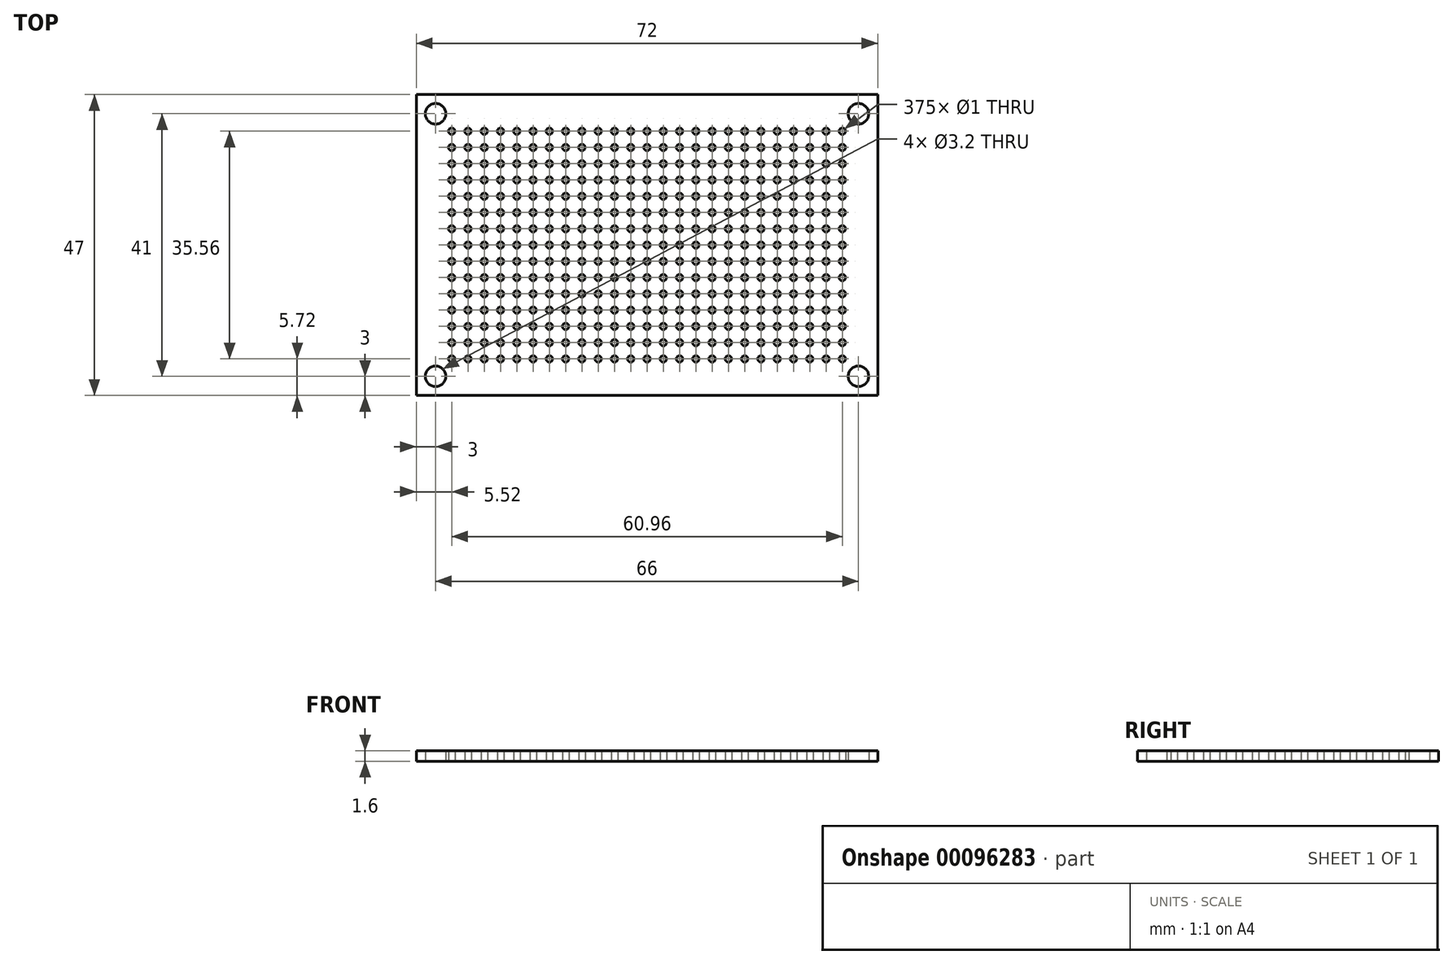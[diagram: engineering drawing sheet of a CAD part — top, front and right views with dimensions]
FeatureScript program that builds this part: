
annotation { "Feature Type Name" : "Feature", "Feature Type Description" : "" }
export const myFeature = defineFeature(function(context is Context, id is Id, definition is map)
    precondition{}
    {
        {
            var Q0;
            Q0=qCreatedBy(makeId("Top.planeOp"),FACE);
            var sketch = newSketch(context, id + "F0", { "sketchPlane" : qUnion([Q0])});
            skCircle(sketch, "E0", {"center": v(-33.1, -21.77) * mm, "radius": 1.6 * mm});
            skCircle(sketch, "E1", {"center": v(32.9, -21.77) * mm, "radius": 1.6 * mm});
            skCircle(sketch, "E2", {"center": v(32.9, 19.23) * mm, "radius": 1.6 * mm});
            skCircle(sketch, "E3", {"center": v(-33.1, 19.23) * mm, "radius": 1.6 * mm});
            skCircle(sketch, "E4", {"center": v(-30.57, -19.05) * mm, "radius": 0.5 * mm});
            skCircle(sketch, "E5.1.0.0", {"center": v(-28.03, -19.05) * mm, "radius": 0.5 * mm});
            skCircle(sketch, "E5.2.0.0", {"center": v(-25.5, -19.05) * mm, "radius": 0.5 * mm});
            skCircle(sketch, "E5.3.0.0", {"center": v(-22.95, -19.05) * mm, "radius": 0.5 * mm});
            skCircle(sketch, "E5.4.0.0", {"center": v(-20.41, -19.05) * mm, "radius": 0.5 * mm});
            skCircle(sketch, "E5.5.0.0", {"center": v(-17.87, -19.05) * mm, "radius": 0.5 * mm});
            skCircle(sketch, "E5.6.0.0", {"center": v(-15.33, -19.05) * mm, "radius": 0.5 * mm});
            skCircle(sketch, "E5.7.0.0", {"center": v(-12.8, -19.05) * mm, "radius": 0.5 * mm});
            skCircle(sketch, "E5.8.0.0", {"center": v(-10.25, -19.05) * mm, "radius": 0.5 * mm});
            skCircle(sketch, "E5.9.0.0", {"center": v(-7.71, -19.05) * mm, "radius": 0.5 * mm});
            skCircle(sketch, "E5.10.0.0", {"center": v(-5.17, -19.05) * mm, "radius": 0.5 * mm});
            skCircle(sketch, "E5.11.0.0", {"center": v(-2.63, -19.05) * mm, "radius": 0.5 * mm});
            skCircle(sketch, "E5.12.0.0", {"center": v(-0.1, -19.05) * mm, "radius": 0.5 * mm});
            skCircle(sketch, "E5.13.0.0", {"center": v(2.45, -19.05) * mm, "radius": 0.5 * mm});
            skCircle(sketch, "E5.14.0.0", {"center": v(4.99, -19.05) * mm, "radius": 0.5 * mm});
            skCircle(sketch, "E5.15.0.0", {"center": v(7.53, -19.05) * mm, "radius": 0.5 * mm});
            skCircle(sketch, "E5.16.0.0", {"center": v(10.07, -19.05) * mm, "radius": 0.5 * mm});
            skCircle(sketch, "E5.17.0.0", {"center": v(12.6, -19.05) * mm, "radius": 0.5 * mm});
            skCircle(sketch, "E5.18.0.0", {"center": v(15.15, -19.05) * mm, "radius": 0.5 * mm});
            skCircle(sketch, "E5.19.0.0", {"center": v(17.69, -19.05) * mm, "radius": 0.5 * mm});
            skCircle(sketch, "E5.20.0.0", {"center": v(20.23, -19.05) * mm, "radius": 0.5 * mm});
            skCircle(sketch, "E5.21.0.0", {"center": v(22.77, -19.05) * mm, "radius": 0.5 * mm});
            skCircle(sketch, "E5.22.0.0", {"center": v(25.3, -19.05) * mm, "radius": 0.5 * mm});
            skCircle(sketch, "E5.23.0.0", {"center": v(27.85, -19.05) * mm, "radius": 0.5 * mm});
            skCircle(sketch, "E5.24.0.0", {"center": v(30.39, -19.05) * mm, "radius": 0.5 * mm});
            skLineSegment(sketch, "E5.direction1", {"start": v(-30.57, -19.05) * mm, "end": v(-28.03, -19.05) * mm, "construction": true});
            skLineSegment(sketch, "E6", {"start": v(-33.1, -21.77) * mm, "end": v(-33.1, -19.23) * mm});
            skCircle(sketch, "E7.1.0.0", {"center": v(-30.57, -16.51) * mm, "radius": 0.5 * mm});
            skCircle(sketch, "E7.2.0.0", {"center": v(-30.57, -13.97) * mm, "radius": 0.5 * mm});
            skLineSegment(sketch, "E7.direction1", {"start": v(-30.57, -19.05) * mm, "end": v(-30.57, -16.51) * mm, "construction": true});
            skCircle(sketch, "E8.0.3.0", {"center": v(-30.57, -11.43) * mm, "radius": 0.5 * mm});
            skCircle(sketch, "E8.0.4.0", {"center": v(-30.57, -8.9) * mm, "radius": 0.5 * mm});
            skCircle(sketch, "E8.0.5.0", {"center": v(-30.57, -6.35) * mm, "radius": 0.5 * mm});
            skCircle(sketch, "E8.0.6.0", {"center": v(-30.57, -3.81) * mm, "radius": 0.5 * mm});
            skCircle(sketch, "E8.0.7.0", {"center": v(-30.57, -1.27) * mm, "radius": 0.5 * mm});
            skCircle(sketch, "E8.0.8.0", {"center": v(-30.57, 1.27) * mm, "radius": 0.5 * mm});
            skCircle(sketch, "E8.0.9.0", {"center": v(-30.57, 3.8) * mm, "radius": 0.5 * mm});
            skCircle(sketch, "E8.0.10.0", {"center": v(-30.57, 6.35) * mm, "radius": 0.5 * mm});
            skCircle(sketch, "E8.0.11.0", {"center": v(-30.57, 8.89) * mm, "radius": 0.5 * mm});
            skCircle(sketch, "E8.0.12.0", {"center": v(-30.57, 11.43) * mm, "radius": 0.5 * mm});
            skCircle(sketch, "E8.0.13.0", {"center": v(-30.57, 13.97) * mm, "radius": 0.5 * mm});
            skCircle(sketch, "E8.0.14.0", {"center": v(-30.57, 16.5) * mm, "radius": 0.5 * mm});
            skCircle(sketch, "E9.1.0.0", {"center": v(25.3, -16.51) * mm, "radius": 0.5 * mm});
            skCircle(sketch, "E9.1.0.1", {"center": v(30.39, -16.51) * mm, "radius": 0.5 * mm});
            skCircle(sketch, "E9.1.0.2", {"center": v(20.23, -16.51) * mm, "radius": 0.5 * mm});
            skCircle(sketch, "E9.1.0.3", {"center": v(22.77, -16.51) * mm, "radius": 0.5 * mm});
            skCircle(sketch, "E9.1.0.4", {"center": v(-7.71, -16.51) * mm, "radius": 0.5 * mm});
            skCircle(sketch, "E9.1.0.5", {"center": v(-15.33, -16.51) * mm, "radius": 0.5 * mm});
            skCircle(sketch, "E9.1.0.6", {"center": v(-5.17, -16.51) * mm, "radius": 0.5 * mm});
            skCircle(sketch, "E9.1.0.7", {"center": v(27.85, -16.51) * mm, "radius": 0.5 * mm});
            skCircle(sketch, "E9.1.0.8", {"center": v(12.6, -16.51) * mm, "radius": 0.5 * mm});
            skCircle(sketch, "E9.1.0.9", {"center": v(4.99, -16.51) * mm, "radius": 0.5 * mm});
            skCircle(sketch, "E9.1.0.10", {"center": v(-10.25, -16.51) * mm, "radius": 0.5 * mm});
            skCircle(sketch, "E9.1.0.11", {"center": v(-0.1, -16.51) * mm, "radius": 0.5 * mm});
            skCircle(sketch, "E9.1.0.12", {"center": v(10.07, -16.51) * mm, "radius": 0.5 * mm});
            skCircle(sketch, "E9.1.0.13", {"center": v(7.53, -16.51) * mm, "radius": 0.5 * mm});
            skCircle(sketch, "E9.1.0.14", {"center": v(17.69, -16.51) * mm, "radius": 0.5 * mm});
            skCircle(sketch, "E9.1.0.15", {"center": v(-2.63, -16.51) * mm, "radius": 0.5 * mm});
            skCircle(sketch, "E9.1.0.16", {"center": v(15.15, -16.51) * mm, "radius": 0.5 * mm});
            skCircle(sketch, "E9.1.0.17", {"center": v(-12.8, -16.51) * mm, "radius": 0.5 * mm});
            skCircle(sketch, "E9.1.0.18", {"center": v(2.45, -16.51) * mm, "radius": 0.5 * mm});
            skCircle(sketch, "E9.1.0.19", {"center": v(-22.95, -16.51) * mm, "radius": 0.5 * mm});
            skCircle(sketch, "E9.1.0.20", {"center": v(-20.41, -16.51) * mm, "radius": 0.5 * mm});
            skCircle(sketch, "E9.1.0.21", {"center": v(-28.03, -16.51) * mm, "radius": 0.5 * mm});
            skCircle(sketch, "E9.1.0.22", {"center": v(-25.5, -16.51) * mm, "radius": 0.5 * mm});
            skCircle(sketch, "E9.1.0.23", {"center": v(-17.87, -16.51) * mm, "radius": 0.5 * mm});
            skCircle(sketch, "E9.2.0.0", {"center": v(25.3, -13.97) * mm, "radius": 0.5 * mm});
            skCircle(sketch, "E9.2.0.1", {"center": v(30.39, -13.97) * mm, "radius": 0.5 * mm});
            skCircle(sketch, "E9.2.0.2", {"center": v(20.23, -13.97) * mm, "radius": 0.5 * mm});
            skCircle(sketch, "E9.2.0.3", {"center": v(22.77, -13.97) * mm, "radius": 0.5 * mm});
            skCircle(sketch, "E9.2.0.4", {"center": v(-7.71, -13.97) * mm, "radius": 0.5 * mm});
            skCircle(sketch, "E9.2.0.5", {"center": v(-15.33, -13.97) * mm, "radius": 0.5 * mm});
            skCircle(sketch, "E9.2.0.6", {"center": v(-5.17, -13.97) * mm, "radius": 0.5 * mm});
            skCircle(sketch, "E9.2.0.7", {"center": v(27.85, -13.97) * mm, "radius": 0.5 * mm});
            skCircle(sketch, "E9.2.0.8", {"center": v(12.6, -13.97) * mm, "radius": 0.5 * mm});
            skCircle(sketch, "E9.2.0.9", {"center": v(4.99, -13.97) * mm, "radius": 0.5 * mm});
            skCircle(sketch, "E9.2.0.10", {"center": v(-10.25, -13.97) * mm, "radius": 0.5 * mm});
            skCircle(sketch, "E9.2.0.11", {"center": v(-0.1, -13.97) * mm, "radius": 0.5 * mm});
            skCircle(sketch, "E9.2.0.12", {"center": v(10.07, -13.97) * mm, "radius": 0.5 * mm});
            skCircle(sketch, "E9.2.0.13", {"center": v(7.53, -13.97) * mm, "radius": 0.5 * mm});
            skCircle(sketch, "E9.2.0.14", {"center": v(17.69, -13.97) * mm, "radius": 0.5 * mm});
            skCircle(sketch, "E9.2.0.15", {"center": v(-2.63, -13.97) * mm, "radius": 0.5 * mm});
            skCircle(sketch, "E9.2.0.16", {"center": v(15.15, -13.97) * mm, "radius": 0.5 * mm});
            skCircle(sketch, "E9.2.0.17", {"center": v(-12.8, -13.97) * mm, "radius": 0.5 * mm});
            skCircle(sketch, "E9.2.0.18", {"center": v(2.45, -13.97) * mm, "radius": 0.5 * mm});
            skCircle(sketch, "E9.2.0.19", {"center": v(-22.95, -13.97) * mm, "radius": 0.5 * mm});
            skCircle(sketch, "E9.2.0.20", {"center": v(-20.41, -13.97) * mm, "radius": 0.5 * mm});
            skCircle(sketch, "E9.2.0.21", {"center": v(-28.03, -13.97) * mm, "radius": 0.5 * mm});
            skCircle(sketch, "E9.2.0.22", {"center": v(-25.5, -13.97) * mm, "radius": 0.5 * mm});
            skCircle(sketch, "E9.2.0.23", {"center": v(-17.87, -13.97) * mm, "radius": 0.5 * mm});
            skCircle(sketch, "E9.3.0.0", {"center": v(25.3, -11.43) * mm, "radius": 0.5 * mm});
            skCircle(sketch, "E9.3.0.1", {"center": v(30.39, -11.43) * mm, "radius": 0.5 * mm});
            skCircle(sketch, "E9.3.0.2", {"center": v(20.23, -11.43) * mm, "radius": 0.5 * mm});
            skCircle(sketch, "E9.3.0.3", {"center": v(22.77, -11.43) * mm, "radius": 0.5 * mm});
            skCircle(sketch, "E9.3.0.4", {"center": v(-7.71, -11.43) * mm, "radius": 0.5 * mm});
            skCircle(sketch, "E9.3.0.5", {"center": v(-15.33, -11.43) * mm, "radius": 0.5 * mm});
            skCircle(sketch, "E9.3.0.6", {"center": v(-5.17, -11.43) * mm, "radius": 0.5 * mm});
            skCircle(sketch, "E9.3.0.7", {"center": v(27.85, -11.43) * mm, "radius": 0.5 * mm});
            skCircle(sketch, "E9.3.0.8", {"center": v(12.6, -11.43) * mm, "radius": 0.5 * mm});
            skCircle(sketch, "E9.3.0.9", {"center": v(4.99, -11.43) * mm, "radius": 0.5 * mm});
            skCircle(sketch, "E9.3.0.10", {"center": v(-10.25, -11.43) * mm, "radius": 0.5 * mm});
            skCircle(sketch, "E9.3.0.11", {"center": v(-0.1, -11.43) * mm, "radius": 0.5 * mm});
            skCircle(sketch, "E9.3.0.12", {"center": v(10.07, -11.43) * mm, "radius": 0.5 * mm});
            skCircle(sketch, "E9.3.0.13", {"center": v(7.53, -11.43) * mm, "radius": 0.5 * mm});
            skCircle(sketch, "E9.3.0.14", {"center": v(17.69, -11.43) * mm, "radius": 0.5 * mm});
            skCircle(sketch, "E9.3.0.15", {"center": v(-2.63, -11.43) * mm, "radius": 0.5 * mm});
            skCircle(sketch, "E9.3.0.16", {"center": v(15.15, -11.43) * mm, "radius": 0.5 * mm});
            skCircle(sketch, "E9.3.0.17", {"center": v(-12.8, -11.43) * mm, "radius": 0.5 * mm});
            skCircle(sketch, "E9.3.0.18", {"center": v(2.45, -11.43) * mm, "radius": 0.5 * mm});
            skCircle(sketch, "E9.3.0.19", {"center": v(-22.95, -11.43) * mm, "radius": 0.5 * mm});
            skCircle(sketch, "E9.3.0.20", {"center": v(-20.41, -11.43) * mm, "radius": 0.5 * mm});
            skCircle(sketch, "E9.3.0.21", {"center": v(-28.03, -11.43) * mm, "radius": 0.5 * mm});
            skCircle(sketch, "E9.3.0.22", {"center": v(-25.5, -11.43) * mm, "radius": 0.5 * mm});
            skCircle(sketch, "E9.3.0.23", {"center": v(-17.87, -11.43) * mm, "radius": 0.5 * mm});
            skCircle(sketch, "E9.4.0.0", {"center": v(25.3, -8.9) * mm, "radius": 0.5 * mm});
            skCircle(sketch, "E9.4.0.1", {"center": v(30.39, -8.9) * mm, "radius": 0.5 * mm});
            skCircle(sketch, "E9.4.0.2", {"center": v(20.23, -8.9) * mm, "radius": 0.5 * mm});
            skCircle(sketch, "E9.4.0.3", {"center": v(22.77, -8.9) * mm, "radius": 0.5 * mm});
            skCircle(sketch, "E9.4.0.4", {"center": v(-7.71, -8.9) * mm, "radius": 0.5 * mm});
            skCircle(sketch, "E9.4.0.5", {"center": v(-15.33, -8.9) * mm, "radius": 0.5 * mm});
            skCircle(sketch, "E9.4.0.6", {"center": v(-5.17, -8.9) * mm, "radius": 0.5 * mm});
            skCircle(sketch, "E9.4.0.7", {"center": v(27.85, -8.9) * mm, "radius": 0.5 * mm});
            skCircle(sketch, "E9.4.0.8", {"center": v(12.6, -8.9) * mm, "radius": 0.5 * mm});
            skCircle(sketch, "E9.4.0.9", {"center": v(4.99, -8.9) * mm, "radius": 0.5 * mm});
            skCircle(sketch, "E9.4.0.10", {"center": v(-10.25, -8.9) * mm, "radius": 0.5 * mm});
            skCircle(sketch, "E9.4.0.11", {"center": v(-0.1, -8.9) * mm, "radius": 0.5 * mm});
            skCircle(sketch, "E9.4.0.12", {"center": v(10.07, -8.9) * mm, "radius": 0.5 * mm});
            skCircle(sketch, "E9.4.0.13", {"center": v(7.53, -8.9) * mm, "radius": 0.5 * mm});
            skCircle(sketch, "E9.4.0.14", {"center": v(17.69, -8.9) * mm, "radius": 0.5 * mm});
            skCircle(sketch, "E9.4.0.15", {"center": v(-2.63, -8.9) * mm, "radius": 0.5 * mm});
            skCircle(sketch, "E9.4.0.16", {"center": v(15.15, -8.9) * mm, "radius": 0.5 * mm});
            skCircle(sketch, "E9.4.0.17", {"center": v(-12.8, -8.9) * mm, "radius": 0.5 * mm});
            skCircle(sketch, "E9.4.0.18", {"center": v(2.45, -8.9) * mm, "radius": 0.5 * mm});
            skCircle(sketch, "E9.4.0.19", {"center": v(-22.95, -8.9) * mm, "radius": 0.5 * mm});
            skCircle(sketch, "E9.4.0.20", {"center": v(-20.41, -8.9) * mm, "radius": 0.5 * mm});
            skCircle(sketch, "E9.4.0.21", {"center": v(-28.03, -8.9) * mm, "radius": 0.5 * mm});
            skCircle(sketch, "E9.4.0.22", {"center": v(-25.5, -8.9) * mm, "radius": 0.5 * mm});
            skCircle(sketch, "E9.4.0.23", {"center": v(-17.87, -8.9) * mm, "radius": 0.5 * mm});
            skCircle(sketch, "E9.5.0.0", {"center": v(25.3, -6.35) * mm, "radius": 0.5 * mm});
            skCircle(sketch, "E9.5.0.1", {"center": v(30.39, -6.35) * mm, "radius": 0.5 * mm});
            skCircle(sketch, "E9.5.0.2", {"center": v(20.23, -6.35) * mm, "radius": 0.5 * mm});
            skCircle(sketch, "E9.5.0.3", {"center": v(22.77, -6.35) * mm, "radius": 0.5 * mm});
            skCircle(sketch, "E9.5.0.4", {"center": v(-7.71, -6.35) * mm, "radius": 0.5 * mm});
            skCircle(sketch, "E9.5.0.5", {"center": v(-15.33, -6.35) * mm, "radius": 0.5 * mm});
            skCircle(sketch, "E9.5.0.6", {"center": v(-5.17, -6.35) * mm, "radius": 0.5 * mm});
            skCircle(sketch, "E9.5.0.7", {"center": v(27.85, -6.35) * mm, "radius": 0.5 * mm});
            skCircle(sketch, "E9.5.0.8", {"center": v(12.6, -6.35) * mm, "radius": 0.5 * mm});
            skCircle(sketch, "E9.5.0.9", {"center": v(4.99, -6.35) * mm, "radius": 0.5 * mm});
            skCircle(sketch, "E9.5.0.10", {"center": v(-10.25, -6.35) * mm, "radius": 0.5 * mm});
            skCircle(sketch, "E9.5.0.11", {"center": v(-0.1, -6.35) * mm, "radius": 0.5 * mm});
            skCircle(sketch, "E9.5.0.12", {"center": v(10.07, -6.35) * mm, "radius": 0.5 * mm});
            skCircle(sketch, "E9.5.0.13", {"center": v(7.53, -6.35) * mm, "radius": 0.5 * mm});
            skCircle(sketch, "E9.5.0.14", {"center": v(17.69, -6.35) * mm, "radius": 0.5 * mm});
            skCircle(sketch, "E9.5.0.15", {"center": v(-2.63, -6.35) * mm, "radius": 0.5 * mm});
            skCircle(sketch, "E9.5.0.16", {"center": v(15.15, -6.35) * mm, "radius": 0.5 * mm});
            skCircle(sketch, "E9.5.0.17", {"center": v(-12.8, -6.35) * mm, "radius": 0.5 * mm});
            skCircle(sketch, "E9.5.0.18", {"center": v(2.45, -6.35) * mm, "radius": 0.5 * mm});
            skCircle(sketch, "E9.5.0.19", {"center": v(-22.95, -6.35) * mm, "radius": 0.5 * mm});
            skCircle(sketch, "E9.5.0.20", {"center": v(-20.41, -6.35) * mm, "radius": 0.5 * mm});
            skCircle(sketch, "E9.5.0.21", {"center": v(-28.03, -6.35) * mm, "radius": 0.5 * mm});
            skCircle(sketch, "E9.5.0.22", {"center": v(-25.5, -6.35) * mm, "radius": 0.5 * mm});
            skCircle(sketch, "E9.5.0.23", {"center": v(-17.87, -6.35) * mm, "radius": 0.5 * mm});
            skCircle(sketch, "E9.6.0.0", {"center": v(25.3, -3.81) * mm, "radius": 0.5 * mm});
            skCircle(sketch, "E9.6.0.1", {"center": v(30.39, -3.81) * mm, "radius": 0.5 * mm});
            skCircle(sketch, "E9.6.0.2", {"center": v(20.23, -3.81) * mm, "radius": 0.5 * mm});
            skCircle(sketch, "E9.6.0.3", {"center": v(22.77, -3.81) * mm, "radius": 0.5 * mm});
            skCircle(sketch, "E9.6.0.4", {"center": v(-7.71, -3.81) * mm, "radius": 0.5 * mm});
            skCircle(sketch, "E9.6.0.5", {"center": v(-15.33, -3.81) * mm, "radius": 0.5 * mm});
            skCircle(sketch, "E9.6.0.6", {"center": v(-5.17, -3.81) * mm, "radius": 0.5 * mm});
            skCircle(sketch, "E9.6.0.7", {"center": v(27.85, -3.81) * mm, "radius": 0.5 * mm});
            skCircle(sketch, "E9.6.0.8", {"center": v(12.6, -3.81) * mm, "radius": 0.5 * mm});
            skCircle(sketch, "E9.6.0.9", {"center": v(4.99, -3.81) * mm, "radius": 0.5 * mm});
            skCircle(sketch, "E9.6.0.10", {"center": v(-10.25, -3.81) * mm, "radius": 0.5 * mm});
            skCircle(sketch, "E9.6.0.11", {"center": v(-0.1, -3.81) * mm, "radius": 0.5 * mm});
            skCircle(sketch, "E9.6.0.12", {"center": v(10.07, -3.81) * mm, "radius": 0.5 * mm});
            skCircle(sketch, "E9.6.0.13", {"center": v(7.53, -3.81) * mm, "radius": 0.5 * mm});
            skCircle(sketch, "E9.6.0.14", {"center": v(17.69, -3.81) * mm, "radius": 0.5 * mm});
            skCircle(sketch, "E9.6.0.15", {"center": v(-2.63, -3.81) * mm, "radius": 0.5 * mm});
            skCircle(sketch, "E9.6.0.16", {"center": v(15.15, -3.81) * mm, "radius": 0.5 * mm});
            skCircle(sketch, "E9.6.0.17", {"center": v(-12.8, -3.81) * mm, "radius": 0.5 * mm});
            skCircle(sketch, "E9.6.0.18", {"center": v(2.45, -3.81) * mm, "radius": 0.5 * mm});
            skCircle(sketch, "E9.6.0.19", {"center": v(-22.95, -3.81) * mm, "radius": 0.5 * mm});
            skCircle(sketch, "E9.6.0.20", {"center": v(-20.41, -3.81) * mm, "radius": 0.5 * mm});
            skCircle(sketch, "E9.6.0.21", {"center": v(-28.03, -3.81) * mm, "radius": 0.5 * mm});
            skCircle(sketch, "E9.6.0.22", {"center": v(-25.5, -3.81) * mm, "radius": 0.5 * mm});
            skCircle(sketch, "E9.6.0.23", {"center": v(-17.87, -3.81) * mm, "radius": 0.5 * mm});
            skCircle(sketch, "E9.7.0.0", {"center": v(25.3, -1.27) * mm, "radius": 0.5 * mm});
            skCircle(sketch, "E9.7.0.1", {"center": v(30.39, -1.27) * mm, "radius": 0.5 * mm});
            skCircle(sketch, "E9.7.0.2", {"center": v(20.23, -1.27) * mm, "radius": 0.5 * mm});
            skCircle(sketch, "E9.7.0.3", {"center": v(22.77, -1.27) * mm, "radius": 0.5 * mm});
            skCircle(sketch, "E9.7.0.4", {"center": v(-7.71, -1.27) * mm, "radius": 0.5 * mm});
            skCircle(sketch, "E9.7.0.5", {"center": v(-15.33, -1.27) * mm, "radius": 0.5 * mm});
            skCircle(sketch, "E9.7.0.6", {"center": v(-5.17, -1.27) * mm, "radius": 0.5 * mm});
            skCircle(sketch, "E9.7.0.7", {"center": v(27.85, -1.27) * mm, "radius": 0.5 * mm});
            skCircle(sketch, "E9.7.0.8", {"center": v(12.6, -1.27) * mm, "radius": 0.5 * mm});
            skCircle(sketch, "E9.7.0.9", {"center": v(4.99, -1.27) * mm, "radius": 0.5 * mm});
            skCircle(sketch, "E9.7.0.10", {"center": v(-10.25, -1.27) * mm, "radius": 0.5 * mm});
            skCircle(sketch, "E9.7.0.11", {"center": v(-0.1, -1.27) * mm, "radius": 0.5 * mm});
            skCircle(sketch, "E9.7.0.12", {"center": v(10.07, -1.27) * mm, "radius": 0.5 * mm});
            skCircle(sketch, "E9.7.0.13", {"center": v(7.53, -1.27) * mm, "radius": 0.5 * mm});
            skCircle(sketch, "E9.7.0.14", {"center": v(17.69, -1.27) * mm, "radius": 0.5 * mm});
            skCircle(sketch, "E9.7.0.15", {"center": v(-2.63, -1.27) * mm, "radius": 0.5 * mm});
            skCircle(sketch, "E9.7.0.16", {"center": v(15.15, -1.27) * mm, "radius": 0.5 * mm});
            skCircle(sketch, "E9.7.0.17", {"center": v(-12.8, -1.27) * mm, "radius": 0.5 * mm});
            skCircle(sketch, "E9.7.0.18", {"center": v(2.45, -1.27) * mm, "radius": 0.5 * mm});
            skCircle(sketch, "E9.7.0.19", {"center": v(-22.95, -1.27) * mm, "radius": 0.5 * mm});
            skCircle(sketch, "E9.7.0.20", {"center": v(-20.41, -1.27) * mm, "radius": 0.5 * mm});
            skCircle(sketch, "E9.7.0.21", {"center": v(-28.03, -1.27) * mm, "radius": 0.5 * mm});
            skCircle(sketch, "E9.7.0.22", {"center": v(-25.5, -1.27) * mm, "radius": 0.5 * mm});
            skCircle(sketch, "E9.7.0.23", {"center": v(-17.87, -1.27) * mm, "radius": 0.5 * mm});
            skCircle(sketch, "E9.8.0.0", {"center": v(25.3, 1.27) * mm, "radius": 0.5 * mm});
            skCircle(sketch, "E9.8.0.1", {"center": v(30.39, 1.27) * mm, "radius": 0.5 * mm});
            skCircle(sketch, "E9.8.0.2", {"center": v(20.23, 1.27) * mm, "radius": 0.5 * mm});
            skCircle(sketch, "E9.8.0.3", {"center": v(22.77, 1.27) * mm, "radius": 0.5 * mm});
            skCircle(sketch, "E9.8.0.4", {"center": v(-7.71, 1.27) * mm, "radius": 0.5 * mm});
            skCircle(sketch, "E9.8.0.5", {"center": v(-15.33, 1.27) * mm, "radius": 0.5 * mm});
            skCircle(sketch, "E9.8.0.6", {"center": v(-5.17, 1.27) * mm, "radius": 0.5 * mm});
            skCircle(sketch, "E9.8.0.7", {"center": v(27.85, 1.27) * mm, "radius": 0.5 * mm});
            skCircle(sketch, "E9.8.0.8", {"center": v(12.6, 1.27) * mm, "radius": 0.5 * mm});
            skCircle(sketch, "E9.8.0.9", {"center": v(4.99, 1.27) * mm, "radius": 0.5 * mm});
            skCircle(sketch, "E9.8.0.10", {"center": v(-10.25, 1.27) * mm, "radius": 0.5 * mm});
            skCircle(sketch, "E9.8.0.11", {"center": v(-0.1, 1.27) * mm, "radius": 0.5 * mm});
            skCircle(sketch, "E9.8.0.12", {"center": v(10.07, 1.27) * mm, "radius": 0.5 * mm});
            skCircle(sketch, "E9.8.0.13", {"center": v(7.53, 1.27) * mm, "radius": 0.5 * mm});
            skCircle(sketch, "E9.8.0.14", {"center": v(17.69, 1.27) * mm, "radius": 0.5 * mm});
            skCircle(sketch, "E9.8.0.15", {"center": v(-2.63, 1.27) * mm, "radius": 0.5 * mm});
            skCircle(sketch, "E9.8.0.16", {"center": v(15.15, 1.27) * mm, "radius": 0.5 * mm});
            skCircle(sketch, "E9.8.0.17", {"center": v(-12.8, 1.27) * mm, "radius": 0.5 * mm});
            skCircle(sketch, "E9.8.0.18", {"center": v(2.45, 1.27) * mm, "radius": 0.5 * mm});
            skCircle(sketch, "E9.8.0.19", {"center": v(-22.95, 1.27) * mm, "radius": 0.5 * mm});
            skCircle(sketch, "E9.8.0.20", {"center": v(-20.41, 1.27) * mm, "radius": 0.5 * mm});
            skCircle(sketch, "E9.8.0.21", {"center": v(-28.03, 1.27) * mm, "radius": 0.5 * mm});
            skCircle(sketch, "E9.8.0.22", {"center": v(-25.5, 1.27) * mm, "radius": 0.5 * mm});
            skCircle(sketch, "E9.8.0.23", {"center": v(-17.87, 1.27) * mm, "radius": 0.5 * mm});
            skCircle(sketch, "E9.9.0.0", {"center": v(25.3, 3.8) * mm, "radius": 0.5 * mm});
            skCircle(sketch, "E9.9.0.1", {"center": v(30.39, 3.8) * mm, "radius": 0.5 * mm});
            skCircle(sketch, "E9.9.0.2", {"center": v(20.23, 3.8) * mm, "radius": 0.5 * mm});
            skCircle(sketch, "E9.9.0.3", {"center": v(22.77, 3.8) * mm, "radius": 0.5 * mm});
            skCircle(sketch, "E9.9.0.4", {"center": v(-7.71, 3.8) * mm, "radius": 0.5 * mm});
            skCircle(sketch, "E9.9.0.5", {"center": v(-15.33, 3.8) * mm, "radius": 0.5 * mm});
            skCircle(sketch, "E9.9.0.6", {"center": v(-5.17, 3.8) * mm, "radius": 0.5 * mm});
            skCircle(sketch, "E9.9.0.7", {"center": v(27.85, 3.8) * mm, "radius": 0.5 * mm});
            skCircle(sketch, "E9.9.0.8", {"center": v(12.6, 3.8) * mm, "radius": 0.5 * mm});
            skCircle(sketch, "E9.9.0.9", {"center": v(4.99, 3.8) * mm, "radius": 0.5 * mm});
            skCircle(sketch, "E9.9.0.10", {"center": v(-10.25, 3.8) * mm, "radius": 0.5 * mm});
            skCircle(sketch, "E9.9.0.11", {"center": v(-0.1, 3.8) * mm, "radius": 0.5 * mm});
            skCircle(sketch, "E9.9.0.12", {"center": v(10.07, 3.8) * mm, "radius": 0.5 * mm});
            skCircle(sketch, "E9.9.0.13", {"center": v(7.53, 3.8) * mm, "radius": 0.5 * mm});
            skCircle(sketch, "E9.9.0.14", {"center": v(17.69, 3.8) * mm, "radius": 0.5 * mm});
            skCircle(sketch, "E9.9.0.15", {"center": v(-2.63, 3.8) * mm, "radius": 0.5 * mm});
            skCircle(sketch, "E9.9.0.16", {"center": v(15.15, 3.8) * mm, "radius": 0.5 * mm});
            skCircle(sketch, "E9.9.0.17", {"center": v(-12.8, 3.8) * mm, "radius": 0.5 * mm});
            skCircle(sketch, "E9.9.0.18", {"center": v(2.45, 3.8) * mm, "radius": 0.5 * mm});
            skCircle(sketch, "E9.9.0.19", {"center": v(-22.95, 3.8) * mm, "radius": 0.5 * mm});
            skCircle(sketch, "E9.9.0.20", {"center": v(-20.41, 3.8) * mm, "radius": 0.5 * mm});
            skCircle(sketch, "E9.9.0.21", {"center": v(-28.03, 3.8) * mm, "radius": 0.5 * mm});
            skCircle(sketch, "E9.9.0.22", {"center": v(-25.5, 3.8) * mm, "radius": 0.5 * mm});
            skCircle(sketch, "E9.9.0.23", {"center": v(-17.87, 3.8) * mm, "radius": 0.5 * mm});
            skCircle(sketch, "E9.10.0.0", {"center": v(25.3, 6.35) * mm, "radius": 0.5 * mm});
            skCircle(sketch, "E9.10.0.1", {"center": v(30.39, 6.35) * mm, "radius": 0.5 * mm});
            skCircle(sketch, "E9.10.0.2", {"center": v(20.23, 6.35) * mm, "radius": 0.5 * mm});
            skCircle(sketch, "E9.10.0.3", {"center": v(22.77, 6.35) * mm, "radius": 0.5 * mm});
            skCircle(sketch, "E9.10.0.4", {"center": v(-7.71, 6.35) * mm, "radius": 0.5 * mm});
            skCircle(sketch, "E9.10.0.5", {"center": v(-15.33, 6.35) * mm, "radius": 0.5 * mm});
            skCircle(sketch, "E9.10.0.6", {"center": v(-5.17, 6.35) * mm, "radius": 0.5 * mm});
            skCircle(sketch, "E9.10.0.7", {"center": v(27.85, 6.35) * mm, "radius": 0.5 * mm});
            skCircle(sketch, "E9.10.0.8", {"center": v(12.6, 6.35) * mm, "radius": 0.5 * mm});
            skCircle(sketch, "E9.10.0.9", {"center": v(4.99, 6.35) * mm, "radius": 0.5 * mm});
            skCircle(sketch, "E9.10.0.10", {"center": v(-10.25, 6.35) * mm, "radius": 0.5 * mm});
            skCircle(sketch, "E9.10.0.11", {"center": v(-0.1, 6.35) * mm, "radius": 0.5 * mm});
            skCircle(sketch, "E9.10.0.12", {"center": v(10.07, 6.35) * mm, "radius": 0.5 * mm});
            skCircle(sketch, "E9.10.0.13", {"center": v(7.53, 6.35) * mm, "radius": 0.5 * mm});
            skCircle(sketch, "E9.10.0.14", {"center": v(17.69, 6.35) * mm, "radius": 0.5 * mm});
            skCircle(sketch, "E9.10.0.15", {"center": v(-2.63, 6.35) * mm, "radius": 0.5 * mm});
            skCircle(sketch, "E9.10.0.16", {"center": v(15.15, 6.35) * mm, "radius": 0.5 * mm});
            skCircle(sketch, "E9.10.0.17", {"center": v(-12.8, 6.35) * mm, "radius": 0.5 * mm});
            skCircle(sketch, "E9.10.0.18", {"center": v(2.45, 6.35) * mm, "radius": 0.5 * mm});
            skCircle(sketch, "E9.10.0.19", {"center": v(-22.95, 6.35) * mm, "radius": 0.5 * mm});
            skCircle(sketch, "E9.10.0.20", {"center": v(-20.41, 6.35) * mm, "radius": 0.5 * mm});
            skCircle(sketch, "E9.10.0.21", {"center": v(-28.03, 6.35) * mm, "radius": 0.5 * mm});
            skCircle(sketch, "E9.10.0.22", {"center": v(-25.5, 6.35) * mm, "radius": 0.5 * mm});
            skCircle(sketch, "E9.10.0.23", {"center": v(-17.87, 6.35) * mm, "radius": 0.5 * mm});
            skCircle(sketch, "E9.11.0.0", {"center": v(25.3, 8.89) * mm, "radius": 0.5 * mm});
            skCircle(sketch, "E9.11.0.1", {"center": v(30.39, 8.89) * mm, "radius": 0.5 * mm});
            skCircle(sketch, "E9.11.0.2", {"center": v(20.23, 8.89) * mm, "radius": 0.5 * mm});
            skCircle(sketch, "E9.11.0.3", {"center": v(22.77, 8.89) * mm, "radius": 0.5 * mm});
            skCircle(sketch, "E9.11.0.4", {"center": v(-7.71, 8.89) * mm, "radius": 0.5 * mm});
            skCircle(sketch, "E9.11.0.5", {"center": v(-15.33, 8.89) * mm, "radius": 0.5 * mm});
            skCircle(sketch, "E9.11.0.6", {"center": v(-5.17, 8.89) * mm, "radius": 0.5 * mm});
            skCircle(sketch, "E9.11.0.7", {"center": v(27.85, 8.89) * mm, "radius": 0.5 * mm});
            skCircle(sketch, "E9.11.0.8", {"center": v(12.6, 8.89) * mm, "radius": 0.5 * mm});
            skCircle(sketch, "E9.11.0.9", {"center": v(4.99, 8.89) * mm, "radius": 0.5 * mm});
            skCircle(sketch, "E9.11.0.10", {"center": v(-10.25, 8.89) * mm, "radius": 0.5 * mm});
            skCircle(sketch, "E9.11.0.11", {"center": v(-0.1, 8.89) * mm, "radius": 0.5 * mm});
            skCircle(sketch, "E9.11.0.12", {"center": v(10.07, 8.89) * mm, "radius": 0.5 * mm});
            skCircle(sketch, "E9.11.0.13", {"center": v(7.53, 8.89) * mm, "radius": 0.5 * mm});
            skCircle(sketch, "E9.11.0.14", {"center": v(17.69, 8.89) * mm, "radius": 0.5 * mm});
            skCircle(sketch, "E9.11.0.15", {"center": v(-2.63, 8.89) * mm, "radius": 0.5 * mm});
            skCircle(sketch, "E9.11.0.16", {"center": v(15.15, 8.89) * mm, "radius": 0.5 * mm});
            skCircle(sketch, "E9.11.0.17", {"center": v(-12.8, 8.89) * mm, "radius": 0.5 * mm});
            skCircle(sketch, "E9.11.0.18", {"center": v(2.45, 8.89) * mm, "radius": 0.5 * mm});
            skCircle(sketch, "E9.11.0.19", {"center": v(-22.95, 8.89) * mm, "radius": 0.5 * mm});
            skCircle(sketch, "E9.11.0.20", {"center": v(-20.41, 8.89) * mm, "radius": 0.5 * mm});
            skCircle(sketch, "E9.11.0.21", {"center": v(-28.03, 8.89) * mm, "radius": 0.5 * mm});
            skCircle(sketch, "E9.11.0.22", {"center": v(-25.5, 8.89) * mm, "radius": 0.5 * mm});
            skCircle(sketch, "E9.11.0.23", {"center": v(-17.87, 8.89) * mm, "radius": 0.5 * mm});
            skCircle(sketch, "E9.12.0.0", {"center": v(25.3, 11.43) * mm, "radius": 0.5 * mm});
            skCircle(sketch, "E9.12.0.1", {"center": v(30.39, 11.43) * mm, "radius": 0.5 * mm});
            skCircle(sketch, "E9.12.0.2", {"center": v(20.23, 11.43) * mm, "radius": 0.5 * mm});
            skCircle(sketch, "E9.12.0.3", {"center": v(22.77, 11.43) * mm, "radius": 0.5 * mm});
            skCircle(sketch, "E9.12.0.4", {"center": v(-7.71, 11.43) * mm, "radius": 0.5 * mm});
            skCircle(sketch, "E9.12.0.5", {"center": v(-15.33, 11.43) * mm, "radius": 0.5 * mm});
            skCircle(sketch, "E9.12.0.6", {"center": v(-5.17, 11.43) * mm, "radius": 0.5 * mm});
            skCircle(sketch, "E9.12.0.7", {"center": v(27.85, 11.43) * mm, "radius": 0.5 * mm});
            skCircle(sketch, "E9.12.0.8", {"center": v(12.6, 11.43) * mm, "radius": 0.5 * mm});
            skCircle(sketch, "E9.12.0.9", {"center": v(4.99, 11.43) * mm, "radius": 0.5 * mm});
            skCircle(sketch, "E9.12.0.10", {"center": v(-10.25, 11.43) * mm, "radius": 0.5 * mm});
            skCircle(sketch, "E9.12.0.11", {"center": v(-0.1, 11.43) * mm, "radius": 0.5 * mm});
            skCircle(sketch, "E9.12.0.12", {"center": v(10.07, 11.43) * mm, "radius": 0.5 * mm});
            skCircle(sketch, "E9.12.0.13", {"center": v(7.53, 11.43) * mm, "radius": 0.5 * mm});
            skCircle(sketch, "E9.12.0.14", {"center": v(17.69, 11.43) * mm, "radius": 0.5 * mm});
            skCircle(sketch, "E9.12.0.15", {"center": v(-2.63, 11.43) * mm, "radius": 0.5 * mm});
            skCircle(sketch, "E9.12.0.16", {"center": v(15.15, 11.43) * mm, "radius": 0.5 * mm});
            skCircle(sketch, "E9.12.0.17", {"center": v(-12.8, 11.43) * mm, "radius": 0.5 * mm});
            skCircle(sketch, "E9.12.0.18", {"center": v(2.45, 11.43) * mm, "radius": 0.5 * mm});
            skCircle(sketch, "E9.12.0.19", {"center": v(-22.95, 11.43) * mm, "radius": 0.5 * mm});
            skCircle(sketch, "E9.12.0.20", {"center": v(-20.41, 11.43) * mm, "radius": 0.5 * mm});
            skCircle(sketch, "E9.12.0.21", {"center": v(-28.03, 11.43) * mm, "radius": 0.5 * mm});
            skCircle(sketch, "E9.12.0.22", {"center": v(-25.5, 11.43) * mm, "radius": 0.5 * mm});
            skCircle(sketch, "E9.12.0.23", {"center": v(-17.87, 11.43) * mm, "radius": 0.5 * mm});
            skCircle(sketch, "E9.13.0.0", {"center": v(25.3, 13.97) * mm, "radius": 0.5 * mm});
            skCircle(sketch, "E9.13.0.1", {"center": v(30.39, 13.97) * mm, "radius": 0.5 * mm});
            skCircle(sketch, "E9.13.0.2", {"center": v(20.23, 13.97) * mm, "radius": 0.5 * mm});
            skCircle(sketch, "E9.13.0.3", {"center": v(22.77, 13.97) * mm, "radius": 0.5 * mm});
            skCircle(sketch, "E9.13.0.4", {"center": v(-7.71, 13.97) * mm, "radius": 0.5 * mm});
            skCircle(sketch, "E9.13.0.5", {"center": v(-15.33, 13.97) * mm, "radius": 0.5 * mm});
            skCircle(sketch, "E9.13.0.6", {"center": v(-5.17, 13.97) * mm, "radius": 0.5 * mm});
            skCircle(sketch, "E9.13.0.7", {"center": v(27.85, 13.97) * mm, "radius": 0.5 * mm});
            skCircle(sketch, "E9.13.0.8", {"center": v(12.6, 13.97) * mm, "radius": 0.5 * mm});
            skCircle(sketch, "E9.13.0.9", {"center": v(4.99, 13.97) * mm, "radius": 0.5 * mm});
            skCircle(sketch, "E9.13.0.10", {"center": v(-10.25, 13.97) * mm, "radius": 0.5 * mm});
            skCircle(sketch, "E9.13.0.11", {"center": v(-0.1, 13.97) * mm, "radius": 0.5 * mm});
            skCircle(sketch, "E9.13.0.12", {"center": v(10.07, 13.97) * mm, "radius": 0.5 * mm});
            skCircle(sketch, "E9.13.0.13", {"center": v(7.53, 13.97) * mm, "radius": 0.5 * mm});
            skCircle(sketch, "E9.13.0.14", {"center": v(17.69, 13.97) * mm, "radius": 0.5 * mm});
            skCircle(sketch, "E9.13.0.15", {"center": v(-2.63, 13.97) * mm, "radius": 0.5 * mm});
            skCircle(sketch, "E9.13.0.16", {"center": v(15.15, 13.97) * mm, "radius": 0.5 * mm});
            skCircle(sketch, "E9.13.0.17", {"center": v(-12.8, 13.97) * mm, "radius": 0.5 * mm});
            skCircle(sketch, "E9.13.0.18", {"center": v(2.45, 13.97) * mm, "radius": 0.5 * mm});
            skCircle(sketch, "E9.13.0.19", {"center": v(-22.95, 13.97) * mm, "radius": 0.5 * mm});
            skCircle(sketch, "E9.13.0.20", {"center": v(-20.41, 13.97) * mm, "radius": 0.5 * mm});
            skCircle(sketch, "E9.13.0.21", {"center": v(-28.03, 13.97) * mm, "radius": 0.5 * mm});
            skCircle(sketch, "E9.13.0.22", {"center": v(-25.5, 13.97) * mm, "radius": 0.5 * mm});
            skCircle(sketch, "E9.13.0.23", {"center": v(-17.87, 13.97) * mm, "radius": 0.5 * mm});
            skCircle(sketch, "E9.14.0.0", {"center": v(25.3, 16.5) * mm, "radius": 0.5 * mm});
            skCircle(sketch, "E9.14.0.1", {"center": v(30.39, 16.5) * mm, "radius": 0.5 * mm});
            skCircle(sketch, "E9.14.0.2", {"center": v(20.23, 16.5) * mm, "radius": 0.5 * mm});
            skCircle(sketch, "E9.14.0.3", {"center": v(22.77, 16.5) * mm, "radius": 0.5 * mm});
            skCircle(sketch, "E9.14.0.4", {"center": v(-7.71, 16.5) * mm, "radius": 0.5 * mm});
            skCircle(sketch, "E9.14.0.5", {"center": v(-15.33, 16.5) * mm, "radius": 0.5 * mm});
            skCircle(sketch, "E9.14.0.6", {"center": v(-5.17, 16.5) * mm, "radius": 0.5 * mm});
            skCircle(sketch, "E9.14.0.7", {"center": v(27.85, 16.5) * mm, "radius": 0.5 * mm});
            skCircle(sketch, "E9.14.0.8", {"center": v(12.6, 16.5) * mm, "radius": 0.5 * mm});
            skCircle(sketch, "E9.14.0.9", {"center": v(4.99, 16.5) * mm, "radius": 0.5 * mm});
            skCircle(sketch, "E9.14.0.10", {"center": v(-10.25, 16.5) * mm, "radius": 0.5 * mm});
            skCircle(sketch, "E9.14.0.11", {"center": v(-0.1, 16.5) * mm, "radius": 0.5 * mm});
            skCircle(sketch, "E9.14.0.12", {"center": v(10.07, 16.5) * mm, "radius": 0.5 * mm});
            skCircle(sketch, "E9.14.0.13", {"center": v(7.53, 16.5) * mm, "radius": 0.5 * mm});
            skCircle(sketch, "E9.14.0.14", {"center": v(17.69, 16.5) * mm, "radius": 0.5 * mm});
            skCircle(sketch, "E9.14.0.15", {"center": v(-2.63, 16.5) * mm, "radius": 0.5 * mm});
            skCircle(sketch, "E9.14.0.16", {"center": v(15.15, 16.5) * mm, "radius": 0.5 * mm});
            skCircle(sketch, "E9.14.0.17", {"center": v(-12.8, 16.5) * mm, "radius": 0.5 * mm});
            skCircle(sketch, "E9.14.0.18", {"center": v(2.45, 16.5) * mm, "radius": 0.5 * mm});
            skCircle(sketch, "E9.14.0.19", {"center": v(-22.95, 16.5) * mm, "radius": 0.5 * mm});
            skCircle(sketch, "E9.14.0.20", {"center": v(-20.41, 16.5) * mm, "radius": 0.5 * mm});
            skCircle(sketch, "E9.14.0.21", {"center": v(-28.03, 16.5) * mm, "radius": 0.5 * mm});
            skCircle(sketch, "E9.14.0.22", {"center": v(-25.5, 16.5) * mm, "radius": 0.5 * mm});
            skCircle(sketch, "E9.14.0.23", {"center": v(-17.87, 16.5) * mm, "radius": 0.5 * mm});
            skLineSegment(sketch, "E9.direction1", {"start": v(-28.03, -19.05) * mm, "end": v(-28.03, -16.51) * mm, "construction": true});
            skSolve(sketch);
        }
        {
            var Q0;
            Q0=qCreatedBy(makeId("Top.planeOp"),FACE);
            var sketch = newSketch(context, id + "F1", { "sketchPlane" : qUnion([Q0])});
            skLineSegment(sketch, "E10.bottom", {"start": v(35.9, -24.77) * mm, "end": v(-36.1, -24.77) * mm});
            skLineSegment(sketch, "E10.top", {"start": v(35.9, 22.23) * mm, "end": v(-36.1, 22.23) * mm});
            skLineSegment(sketch, "E10.left", {"start": v(35.9, -24.77) * mm, "end": v(35.9, 22.23) * mm});
            skLineSegment(sketch, "E10.right", {"start": v(-36.1, -24.77) * mm, "end": v(-36.1, 22.23) * mm});
            skSolve(sketch);
        }
        {
            var Q0;
            Q0=qSketchRegion(id+"F0",true);
            extrude(context, id + "F2", {"entities" : qUnion([Q0]), "depth" : 3 * mm});
        }
        {
            var Q0;
            Q0=makeQuery(id+"F2.opExtrude","SWEPT_BODY",BODY,{"disambiguationData":[OSD([sQuery(id+"F0.wireOp",EDGE,"E0")])]});
            var Q1;
            Q1=makeQuery(id+"F2.opExtrude","SWEPT_BODY",BODY,{"disambiguationData":[OSD([sQuery(id+"F0.wireOp",EDGE,"E1")])]});
            var Q2;
            Q2=makeQuery(id+"F2.opExtrude","SWEPT_BODY",BODY,{"disambiguationData":[OSD([sQuery(id+"F0.wireOp",EDGE,"E2")])]});
            var Q3;
            Q3=makeQuery(id+"F2.opExtrude","SWEPT_BODY",BODY,{"disambiguationData":[OSD([sQuery(id+"F0.wireOp",EDGE,"E3")])]});
            var Q4;
            Q4=makeQuery(id+"F2.opExtrude","SWEPT_BODY",BODY,{"disambiguationData":[OSD([sQuery(id+"F0.wireOp",EDGE,"E4")])]});
            var Q5;
            Q5=makeQuery(id+"F2.opExtrude","SWEPT_BODY",BODY,{"disambiguationData":[OSD([sQuery(id+"F0.wireOp",EDGE,"E5.1.0.0")])]});
            var Q6;
            Q6=makeQuery(id+"F2.opExtrude","SWEPT_BODY",BODY,{"disambiguationData":[OSD([sQuery(id+"F0.wireOp",EDGE,"E5.2.0.0")])]});
            var Q7;
            Q7=makeQuery(id+"F2.opExtrude","SWEPT_BODY",BODY,{"disambiguationData":[OSD([sQuery(id+"F0.wireOp",EDGE,"E5.3.0.0")])]});
            var Q8;
            Q8=makeQuery(id+"F2.opExtrude","SWEPT_BODY",BODY,{"disambiguationData":[OSD([sQuery(id+"F0.wireOp",EDGE,"E5.4.0.0")])]});
            var Q9;
            Q9=makeQuery(id+"F2.opExtrude","SWEPT_BODY",BODY,{"disambiguationData":[OSD([sQuery(id+"F0.wireOp",EDGE,"E5.5.0.0")])]});
            var Q10;
            Q10=makeQuery(id+"F2.opExtrude","SWEPT_BODY",BODY,{"disambiguationData":[OSD([sQuery(id+"F0.wireOp",EDGE,"E5.6.0.0")])]});
            var Q11;
            Q11=makeQuery(id+"F2.opExtrude","SWEPT_BODY",BODY,{"disambiguationData":[OSD([sQuery(id+"F0.wireOp",EDGE,"E5.7.0.0")])]});
            var Q12;
            Q12=makeQuery(id+"F2.opExtrude","SWEPT_BODY",BODY,{"disambiguationData":[OSD([sQuery(id+"F0.wireOp",EDGE,"E5.8.0.0")])]});
            var Q13;
            Q13=makeQuery(id+"F2.opExtrude","SWEPT_BODY",BODY,{"disambiguationData":[OSD([sQuery(id+"F0.wireOp",EDGE,"E5.9.0.0")])]});
            var Q14;
            Q14=makeQuery(id+"F2.opExtrude","SWEPT_BODY",BODY,{"disambiguationData":[OSD([sQuery(id+"F0.wireOp",EDGE,"E5.10.0.0")])]});
            var Q15;
            Q15=makeQuery(id+"F2.opExtrude","SWEPT_BODY",BODY,{"disambiguationData":[OSD([sQuery(id+"F0.wireOp",EDGE,"E5.11.0.0")])]});
            var Q16;
            Q16=makeQuery(id+"F2.opExtrude","SWEPT_BODY",BODY,{"disambiguationData":[OSD([sQuery(id+"F0.wireOp",EDGE,"E5.12.0.0")])]});
            var Q17;
            Q17=makeQuery(id+"F2.opExtrude","SWEPT_BODY",BODY,{"disambiguationData":[OSD([sQuery(id+"F0.wireOp",EDGE,"E5.13.0.0")])]});
            var Q18;
            Q18=makeQuery(id+"F2.opExtrude","SWEPT_BODY",BODY,{"disambiguationData":[OSD([sQuery(id+"F0.wireOp",EDGE,"E5.14.0.0")])]});
            var Q19;
            Q19=makeQuery(id+"F2.opExtrude","SWEPT_BODY",BODY,{"disambiguationData":[OSD([sQuery(id+"F0.wireOp",EDGE,"E5.15.0.0")])]});
            var Q20;
            Q20=makeQuery(id+"F2.opExtrude","SWEPT_BODY",BODY,{"disambiguationData":[OSD([sQuery(id+"F0.wireOp",EDGE,"E5.16.0.0")])]});
            var Q21;
            Q21=makeQuery(id+"F2.opExtrude","SWEPT_BODY",BODY,{"disambiguationData":[OSD([sQuery(id+"F0.wireOp",EDGE,"E5.17.0.0")])]});
            var Q22;
            Q22=makeQuery(id+"F2.opExtrude","SWEPT_BODY",BODY,{"disambiguationData":[OSD([sQuery(id+"F0.wireOp",EDGE,"E5.18.0.0")])]});
            var Q23;
            Q23=makeQuery(id+"F2.opExtrude","SWEPT_BODY",BODY,{"disambiguationData":[OSD([sQuery(id+"F0.wireOp",EDGE,"E5.19.0.0")])]});
            var Q24;
            Q24=makeQuery(id+"F2.opExtrude","SWEPT_BODY",BODY,{"disambiguationData":[OSD([sQuery(id+"F0.wireOp",EDGE,"E5.20.0.0")])]});
            var Q25;
            Q25=makeQuery(id+"F2.opExtrude","SWEPT_BODY",BODY,{"disambiguationData":[OSD([sQuery(id+"F0.wireOp",EDGE,"E5.21.0.0")])]});
            var Q26;
            Q26=makeQuery(id+"F2.opExtrude","SWEPT_BODY",BODY,{"disambiguationData":[OSD([sQuery(id+"F0.wireOp",EDGE,"E5.22.0.0")])]});
            var Q27;
            Q27=makeQuery(id+"F2.opExtrude","SWEPT_BODY",BODY,{"disambiguationData":[OSD([sQuery(id+"F0.wireOp",EDGE,"E5.23.0.0")])]});
            var Q28;
            Q28=makeQuery(id+"F2.opExtrude","SWEPT_BODY",BODY,{"disambiguationData":[OSD([sQuery(id+"F0.wireOp",EDGE,"E5.24.0.0")])]});
            var Q29;
            Q29=makeQuery(id+"F2.opExtrude","SWEPT_BODY",BODY,{"disambiguationData":[OSD([sQuery(id+"F0.wireOp",EDGE,"E7.1.0.0")])]});
            var Q30;
            Q30=makeQuery(id+"F2.opExtrude","SWEPT_BODY",BODY,{"disambiguationData":[OSD([sQuery(id+"F0.wireOp",EDGE,"E7.2.0.0")])]});
            var Q31;
            Q31=makeQuery(id+"F2.opExtrude","SWEPT_BODY",BODY,{"disambiguationData":[OSD([sQuery(id+"F0.wireOp",EDGE,"E8.0.3.0")])]});
            var Q32;
            Q32=makeQuery(id+"F2.opExtrude","SWEPT_BODY",BODY,{"disambiguationData":[OSD([sQuery(id+"F0.wireOp",EDGE,"E8.0.4.0")])]});
            var Q33;
            Q33=makeQuery(id+"F2.opExtrude","SWEPT_BODY",BODY,{"disambiguationData":[OSD([sQuery(id+"F0.wireOp",EDGE,"E8.0.5.0")])]});
            var Q34;
            Q34=makeQuery(id+"F2.opExtrude","SWEPT_BODY",BODY,{"disambiguationData":[OSD([sQuery(id+"F0.wireOp",EDGE,"E8.0.6.0")])]});
            var Q35;
            Q35=makeQuery(id+"F2.opExtrude","SWEPT_BODY",BODY,{"disambiguationData":[OSD([sQuery(id+"F0.wireOp",EDGE,"E8.0.7.0")])]});
            var Q36;
            Q36=makeQuery(id+"F2.opExtrude","SWEPT_BODY",BODY,{"disambiguationData":[OSD([sQuery(id+"F0.wireOp",EDGE,"E8.0.8.0")])]});
            var Q37;
            Q37=makeQuery(id+"F2.opExtrude","SWEPT_BODY",BODY,{"disambiguationData":[OSD([sQuery(id+"F0.wireOp",EDGE,"E8.0.9.0")])]});
            var Q38;
            Q38=makeQuery(id+"F2.opExtrude","SWEPT_BODY",BODY,{"disambiguationData":[OSD([sQuery(id+"F0.wireOp",EDGE,"E8.0.10.0")])]});
            var Q39;
            Q39=makeQuery(id+"F2.opExtrude","SWEPT_BODY",BODY,{"disambiguationData":[OSD([sQuery(id+"F0.wireOp",EDGE,"E8.0.11.0")])]});
            var Q40;
            Q40=makeQuery(id+"F2.opExtrude","SWEPT_BODY",BODY,{"disambiguationData":[OSD([sQuery(id+"F0.wireOp",EDGE,"E8.0.12.0")])]});
            var Q41;
            Q41=makeQuery(id+"F2.opExtrude","SWEPT_BODY",BODY,{"disambiguationData":[OSD([sQuery(id+"F0.wireOp",EDGE,"E8.0.13.0")])]});
            var Q42;
            Q42=makeQuery(id+"F2.opExtrude","SWEPT_BODY",BODY,{"disambiguationData":[OSD([sQuery(id+"F0.wireOp",EDGE,"E8.0.14.0")])]});
            var Q43;
            Q43=makeQuery(id+"F2.opExtrude","SWEPT_BODY",BODY,{"disambiguationData":[OSD([sQuery(id+"F0.wireOp",EDGE,"E9.1.0.0")])]});
            var Q44;
            Q44=makeQuery(id+"F2.opExtrude","SWEPT_BODY",BODY,{"disambiguationData":[OSD([sQuery(id+"F0.wireOp",EDGE,"E9.1.0.1")])]});
            var Q45;
            Q45=makeQuery(id+"F2.opExtrude","SWEPT_BODY",BODY,{"disambiguationData":[OSD([sQuery(id+"F0.wireOp",EDGE,"E9.1.0.2")])]});
            var Q46;
            Q46=makeQuery(id+"F2.opExtrude","SWEPT_BODY",BODY,{"disambiguationData":[OSD([sQuery(id+"F0.wireOp",EDGE,"E9.1.0.3")])]});
            var Q47;
            Q47=makeQuery(id+"F2.opExtrude","SWEPT_BODY",BODY,{"disambiguationData":[OSD([sQuery(id+"F0.wireOp",EDGE,"E9.1.0.4")])]});
            var Q48;
            Q48=makeQuery(id+"F2.opExtrude","SWEPT_BODY",BODY,{"disambiguationData":[OSD([sQuery(id+"F0.wireOp",EDGE,"E9.1.0.5")])]});
            var Q49;
            Q49=makeQuery(id+"F2.opExtrude","SWEPT_BODY",BODY,{"disambiguationData":[OSD([sQuery(id+"F0.wireOp",EDGE,"E9.1.0.6")])]});
            var Q50;
            Q50=makeQuery(id+"F2.opExtrude","SWEPT_BODY",BODY,{"disambiguationData":[OSD([sQuery(id+"F0.wireOp",EDGE,"E9.1.0.7")])]});
            var Q51;
            Q51=makeQuery(id+"F2.opExtrude","SWEPT_BODY",BODY,{"disambiguationData":[OSD([sQuery(id+"F0.wireOp",EDGE,"E9.1.0.8")])]});
            var Q52;
            Q52=makeQuery(id+"F2.opExtrude","SWEPT_BODY",BODY,{"disambiguationData":[OSD([sQuery(id+"F0.wireOp",EDGE,"E9.1.0.9")])]});
            var Q53;
            Q53=makeQuery(id+"F2.opExtrude","SWEPT_BODY",BODY,{"disambiguationData":[OSD([sQuery(id+"F0.wireOp",EDGE,"E9.1.0.10")])]});
            var Q54;
            Q54=makeQuery(id+"F2.opExtrude","SWEPT_BODY",BODY,{"disambiguationData":[OSD([sQuery(id+"F0.wireOp",EDGE,"E9.1.0.11")])]});
            var Q55;
            Q55=makeQuery(id+"F2.opExtrude","SWEPT_BODY",BODY,{"disambiguationData":[OSD([sQuery(id+"F0.wireOp",EDGE,"E9.1.0.12")])]});
            var Q56;
            Q56=makeQuery(id+"F2.opExtrude","SWEPT_BODY",BODY,{"disambiguationData":[OSD([sQuery(id+"F0.wireOp",EDGE,"E9.1.0.13")])]});
            var Q57;
            Q57=makeQuery(id+"F2.opExtrude","SWEPT_BODY",BODY,{"disambiguationData":[OSD([sQuery(id+"F0.wireOp",EDGE,"E9.1.0.14")])]});
            var Q58;
            Q58=makeQuery(id+"F2.opExtrude","SWEPT_BODY",BODY,{"disambiguationData":[OSD([sQuery(id+"F0.wireOp",EDGE,"E9.1.0.15")])]});
            var Q59;
            Q59=makeQuery(id+"F2.opExtrude","SWEPT_BODY",BODY,{"disambiguationData":[OSD([sQuery(id+"F0.wireOp",EDGE,"E9.1.0.16")])]});
            var Q60;
            Q60=makeQuery(id+"F2.opExtrude","SWEPT_BODY",BODY,{"disambiguationData":[OSD([sQuery(id+"F0.wireOp",EDGE,"E9.1.0.17")])]});
            var Q61;
            Q61=makeQuery(id+"F2.opExtrude","SWEPT_BODY",BODY,{"disambiguationData":[OSD([sQuery(id+"F0.wireOp",EDGE,"E9.1.0.18")])]});
            var Q62;
            Q62=makeQuery(id+"F2.opExtrude","SWEPT_BODY",BODY,{"disambiguationData":[OSD([sQuery(id+"F0.wireOp",EDGE,"E9.1.0.19")])]});
            var Q63;
            Q63=makeQuery(id+"F2.opExtrude","SWEPT_BODY",BODY,{"disambiguationData":[OSD([sQuery(id+"F0.wireOp",EDGE,"E9.1.0.20")])]});
            var Q64;
            Q64=makeQuery(id+"F2.opExtrude","SWEPT_BODY",BODY,{"disambiguationData":[OSD([sQuery(id+"F0.wireOp",EDGE,"E9.1.0.21")])]});
            var Q65;
            Q65=makeQuery(id+"F2.opExtrude","SWEPT_BODY",BODY,{"disambiguationData":[OSD([sQuery(id+"F0.wireOp",EDGE,"E9.1.0.22")])]});
            var Q66;
            Q66=makeQuery(id+"F2.opExtrude","SWEPT_BODY",BODY,{"disambiguationData":[OSD([sQuery(id+"F0.wireOp",EDGE,"E9.1.0.23")])]});
            var Q67;
            Q67=makeQuery(id+"F2.opExtrude","SWEPT_BODY",BODY,{"disambiguationData":[OSD([sQuery(id+"F0.wireOp",EDGE,"E9.2.0.0")])]});
            var Q68;
            Q68=makeQuery(id+"F2.opExtrude","SWEPT_BODY",BODY,{"disambiguationData":[OSD([sQuery(id+"F0.wireOp",EDGE,"E9.2.0.1")])]});
            var Q69;
            Q69=makeQuery(id+"F2.opExtrude","SWEPT_BODY",BODY,{"disambiguationData":[OSD([sQuery(id+"F0.wireOp",EDGE,"E9.2.0.2")])]});
            var Q70;
            Q70=makeQuery(id+"F2.opExtrude","SWEPT_BODY",BODY,{"disambiguationData":[OSD([sQuery(id+"F0.wireOp",EDGE,"E9.2.0.3")])]});
            var Q71;
            Q71=makeQuery(id+"F2.opExtrude","SWEPT_BODY",BODY,{"disambiguationData":[OSD([sQuery(id+"F0.wireOp",EDGE,"E9.2.0.4")])]});
            var Q72;
            Q72=makeQuery(id+"F2.opExtrude","SWEPT_BODY",BODY,{"disambiguationData":[OSD([sQuery(id+"F0.wireOp",EDGE,"E9.2.0.5")])]});
            var Q73;
            Q73=makeQuery(id+"F2.opExtrude","SWEPT_BODY",BODY,{"disambiguationData":[OSD([sQuery(id+"F0.wireOp",EDGE,"E9.2.0.6")])]});
            var Q74;
            Q74=makeQuery(id+"F2.opExtrude","SWEPT_BODY",BODY,{"disambiguationData":[OSD([sQuery(id+"F0.wireOp",EDGE,"E9.2.0.7")])]});
            var Q75;
            Q75=makeQuery(id+"F2.opExtrude","SWEPT_BODY",BODY,{"disambiguationData":[OSD([sQuery(id+"F0.wireOp",EDGE,"E9.2.0.8")])]});
            var Q76;
            Q76=makeQuery(id+"F2.opExtrude","SWEPT_BODY",BODY,{"disambiguationData":[OSD([sQuery(id+"F0.wireOp",EDGE,"E9.2.0.9")])]});
            var Q77;
            Q77=makeQuery(id+"F2.opExtrude","SWEPT_BODY",BODY,{"disambiguationData":[OSD([sQuery(id+"F0.wireOp",EDGE,"E9.2.0.10")])]});
            var Q78;
            Q78=makeQuery(id+"F2.opExtrude","SWEPT_BODY",BODY,{"disambiguationData":[OSD([sQuery(id+"F0.wireOp",EDGE,"E9.2.0.11")])]});
            var Q79;
            Q79=makeQuery(id+"F2.opExtrude","SWEPT_BODY",BODY,{"disambiguationData":[OSD([sQuery(id+"F0.wireOp",EDGE,"E9.2.0.12")])]});
            var Q80;
            Q80=makeQuery(id+"F2.opExtrude","SWEPT_BODY",BODY,{"disambiguationData":[OSD([sQuery(id+"F0.wireOp",EDGE,"E9.2.0.13")])]});
            var Q81;
            Q81=makeQuery(id+"F2.opExtrude","SWEPT_BODY",BODY,{"disambiguationData":[OSD([sQuery(id+"F0.wireOp",EDGE,"E9.2.0.14")])]});
            var Q82;
            Q82=makeQuery(id+"F2.opExtrude","SWEPT_BODY",BODY,{"disambiguationData":[OSD([sQuery(id+"F0.wireOp",EDGE,"E9.2.0.15")])]});
            var Q83;
            Q83=makeQuery(id+"F2.opExtrude","SWEPT_BODY",BODY,{"disambiguationData":[OSD([sQuery(id+"F0.wireOp",EDGE,"E9.2.0.16")])]});
            var Q84;
            Q84=makeQuery(id+"F2.opExtrude","SWEPT_BODY",BODY,{"disambiguationData":[OSD([sQuery(id+"F0.wireOp",EDGE,"E9.2.0.17")])]});
            var Q85;
            Q85=makeQuery(id+"F2.opExtrude","SWEPT_BODY",BODY,{"disambiguationData":[OSD([sQuery(id+"F0.wireOp",EDGE,"E9.2.0.18")])]});
            var Q86;
            Q86=makeQuery(id+"F2.opExtrude","SWEPT_BODY",BODY,{"disambiguationData":[OSD([sQuery(id+"F0.wireOp",EDGE,"E9.2.0.19")])]});
            var Q87;
            Q87=makeQuery(id+"F2.opExtrude","SWEPT_BODY",BODY,{"disambiguationData":[OSD([sQuery(id+"F0.wireOp",EDGE,"E9.2.0.20")])]});
            var Q88;
            Q88=makeQuery(id+"F2.opExtrude","SWEPT_BODY",BODY,{"disambiguationData":[OSD([sQuery(id+"F0.wireOp",EDGE,"E9.2.0.21")])]});
            var Q89;
            Q89=makeQuery(id+"F2.opExtrude","SWEPT_BODY",BODY,{"disambiguationData":[OSD([sQuery(id+"F0.wireOp",EDGE,"E9.2.0.22")])]});
            var Q90;
            Q90=makeQuery(id+"F2.opExtrude","SWEPT_BODY",BODY,{"disambiguationData":[OSD([sQuery(id+"F0.wireOp",EDGE,"E9.2.0.23")])]});
            var Q91;
            Q91=makeQuery(id+"F2.opExtrude","SWEPT_BODY",BODY,{"disambiguationData":[OSD([sQuery(id+"F0.wireOp",EDGE,"E9.3.0.0")])]});
            var Q92;
            Q92=makeQuery(id+"F2.opExtrude","SWEPT_BODY",BODY,{"disambiguationData":[OSD([sQuery(id+"F0.wireOp",EDGE,"E9.3.0.1")])]});
            var Q93;
            Q93=makeQuery(id+"F2.opExtrude","SWEPT_BODY",BODY,{"disambiguationData":[OSD([sQuery(id+"F0.wireOp",EDGE,"E9.3.0.2")])]});
            var Q94;
            Q94=makeQuery(id+"F2.opExtrude","SWEPT_BODY",BODY,{"disambiguationData":[OSD([sQuery(id+"F0.wireOp",EDGE,"E9.3.0.3")])]});
            var Q95;
            Q95=makeQuery(id+"F2.opExtrude","SWEPT_BODY",BODY,{"disambiguationData":[OSD([sQuery(id+"F0.wireOp",EDGE,"E9.3.0.4")])]});
            var Q96;
            Q96=makeQuery(id+"F2.opExtrude","SWEPT_BODY",BODY,{"disambiguationData":[OSD([sQuery(id+"F0.wireOp",EDGE,"E9.3.0.5")])]});
            var Q97;
            Q97=makeQuery(id+"F2.opExtrude","SWEPT_BODY",BODY,{"disambiguationData":[OSD([sQuery(id+"F0.wireOp",EDGE,"E9.3.0.6")])]});
            var Q98;
            Q98=makeQuery(id+"F2.opExtrude","SWEPT_BODY",BODY,{"disambiguationData":[OSD([sQuery(id+"F0.wireOp",EDGE,"E9.3.0.7")])]});
            var Q99;
            Q99=makeQuery(id+"F2.opExtrude","SWEPT_BODY",BODY,{"disambiguationData":[OSD([sQuery(id+"F0.wireOp",EDGE,"E9.3.0.8")])]});
            var Q100;
            Q100=makeQuery(id+"F2.opExtrude","SWEPT_BODY",BODY,{"disambiguationData":[OSD([sQuery(id+"F0.wireOp",EDGE,"E9.3.0.9")])]});
            var Q101;
            Q101=makeQuery(id+"F2.opExtrude","SWEPT_BODY",BODY,{"disambiguationData":[OSD([sQuery(id+"F0.wireOp",EDGE,"E9.3.0.10")])]});
            var Q102;
            Q102=makeQuery(id+"F2.opExtrude","SWEPT_BODY",BODY,{"disambiguationData":[OSD([sQuery(id+"F0.wireOp",EDGE,"E9.3.0.11")])]});
            var Q103;
            Q103=makeQuery(id+"F2.opExtrude","SWEPT_BODY",BODY,{"disambiguationData":[OSD([sQuery(id+"F0.wireOp",EDGE,"E9.3.0.12")])]});
            var Q104;
            Q104=makeQuery(id+"F2.opExtrude","SWEPT_BODY",BODY,{"disambiguationData":[OSD([sQuery(id+"F0.wireOp",EDGE,"E9.3.0.13")])]});
            var Q105;
            Q105=makeQuery(id+"F2.opExtrude","SWEPT_BODY",BODY,{"disambiguationData":[OSD([sQuery(id+"F0.wireOp",EDGE,"E9.3.0.14")])]});
            var Q106;
            Q106=makeQuery(id+"F2.opExtrude","SWEPT_BODY",BODY,{"disambiguationData":[OSD([sQuery(id+"F0.wireOp",EDGE,"E9.3.0.15")])]});
            var Q107;
            Q107=makeQuery(id+"F2.opExtrude","SWEPT_BODY",BODY,{"disambiguationData":[OSD([sQuery(id+"F0.wireOp",EDGE,"E9.3.0.16")])]});
            var Q108;
            Q108=makeQuery(id+"F2.opExtrude","SWEPT_BODY",BODY,{"disambiguationData":[OSD([sQuery(id+"F0.wireOp",EDGE,"E9.3.0.17")])]});
            var Q109;
            Q109=makeQuery(id+"F2.opExtrude","SWEPT_BODY",BODY,{"disambiguationData":[OSD([sQuery(id+"F0.wireOp",EDGE,"E9.3.0.18")])]});
            var Q110;
            Q110=makeQuery(id+"F2.opExtrude","SWEPT_BODY",BODY,{"disambiguationData":[OSD([sQuery(id+"F0.wireOp",EDGE,"E9.3.0.19")])]});
            var Q111;
            Q111=makeQuery(id+"F2.opExtrude","SWEPT_BODY",BODY,{"disambiguationData":[OSD([sQuery(id+"F0.wireOp",EDGE,"E9.3.0.20")])]});
            var Q112;
            Q112=makeQuery(id+"F2.opExtrude","SWEPT_BODY",BODY,{"disambiguationData":[OSD([sQuery(id+"F0.wireOp",EDGE,"E9.3.0.21")])]});
            var Q113;
            Q113=makeQuery(id+"F2.opExtrude","SWEPT_BODY",BODY,{"disambiguationData":[OSD([sQuery(id+"F0.wireOp",EDGE,"E9.3.0.22")])]});
            var Q114;
            Q114=makeQuery(id+"F2.opExtrude","SWEPT_BODY",BODY,{"disambiguationData":[OSD([sQuery(id+"F0.wireOp",EDGE,"E9.3.0.23")])]});
            var Q115;
            Q115=makeQuery(id+"F2.opExtrude","SWEPT_BODY",BODY,{"disambiguationData":[OSD([sQuery(id+"F0.wireOp",EDGE,"E9.4.0.0")])]});
            var Q116;
            Q116=makeQuery(id+"F2.opExtrude","SWEPT_BODY",BODY,{"disambiguationData":[OSD([sQuery(id+"F0.wireOp",EDGE,"E9.4.0.1")])]});
            var Q117;
            Q117=makeQuery(id+"F2.opExtrude","SWEPT_BODY",BODY,{"disambiguationData":[OSD([sQuery(id+"F0.wireOp",EDGE,"E9.4.0.2")])]});
            var Q118;
            Q118=makeQuery(id+"F2.opExtrude","SWEPT_BODY",BODY,{"disambiguationData":[OSD([sQuery(id+"F0.wireOp",EDGE,"E9.4.0.3")])]});
            var Q119;
            Q119=makeQuery(id+"F2.opExtrude","SWEPT_BODY",BODY,{"disambiguationData":[OSD([sQuery(id+"F0.wireOp",EDGE,"E9.4.0.4")])]});
            var Q120;
            Q120=makeQuery(id+"F2.opExtrude","SWEPT_BODY",BODY,{"disambiguationData":[OSD([sQuery(id+"F0.wireOp",EDGE,"E9.4.0.5")])]});
            var Q121;
            Q121=makeQuery(id+"F2.opExtrude","SWEPT_BODY",BODY,{"disambiguationData":[OSD([sQuery(id+"F0.wireOp",EDGE,"E9.4.0.6")])]});
            var Q122;
            Q122=makeQuery(id+"F2.opExtrude","SWEPT_BODY",BODY,{"disambiguationData":[OSD([sQuery(id+"F0.wireOp",EDGE,"E9.4.0.7")])]});
            var Q123;
            Q123=makeQuery(id+"F2.opExtrude","SWEPT_BODY",BODY,{"disambiguationData":[OSD([sQuery(id+"F0.wireOp",EDGE,"E9.4.0.8")])]});
            var Q124;
            Q124=makeQuery(id+"F2.opExtrude","SWEPT_BODY",BODY,{"disambiguationData":[OSD([sQuery(id+"F0.wireOp",EDGE,"E9.4.0.9")])]});
            var Q125;
            Q125=makeQuery(id+"F2.opExtrude","SWEPT_BODY",BODY,{"disambiguationData":[OSD([sQuery(id+"F0.wireOp",EDGE,"E9.4.0.10")])]});
            var Q126;
            Q126=makeQuery(id+"F2.opExtrude","SWEPT_BODY",BODY,{"disambiguationData":[OSD([sQuery(id+"F0.wireOp",EDGE,"E9.4.0.11")])]});
            var Q127;
            Q127=makeQuery(id+"F2.opExtrude","SWEPT_BODY",BODY,{"disambiguationData":[OSD([sQuery(id+"F0.wireOp",EDGE,"E9.4.0.12")])]});
            var Q128;
            Q128=makeQuery(id+"F2.opExtrude","SWEPT_BODY",BODY,{"disambiguationData":[OSD([sQuery(id+"F0.wireOp",EDGE,"E9.4.0.13")])]});
            var Q129;
            Q129=makeQuery(id+"F2.opExtrude","SWEPT_BODY",BODY,{"disambiguationData":[OSD([sQuery(id+"F0.wireOp",EDGE,"E9.4.0.14")])]});
            var Q130;
            Q130=makeQuery(id+"F2.opExtrude","SWEPT_BODY",BODY,{"disambiguationData":[OSD([sQuery(id+"F0.wireOp",EDGE,"E9.4.0.15")])]});
            var Q131;
            Q131=makeQuery(id+"F2.opExtrude","SWEPT_BODY",BODY,{"disambiguationData":[OSD([sQuery(id+"F0.wireOp",EDGE,"E9.4.0.16")])]});
            var Q132;
            Q132=makeQuery(id+"F2.opExtrude","SWEPT_BODY",BODY,{"disambiguationData":[OSD([sQuery(id+"F0.wireOp",EDGE,"E9.4.0.17")])]});
            var Q133;
            Q133=makeQuery(id+"F2.opExtrude","SWEPT_BODY",BODY,{"disambiguationData":[OSD([sQuery(id+"F0.wireOp",EDGE,"E9.4.0.18")])]});
            var Q134;
            Q134=makeQuery(id+"F2.opExtrude","SWEPT_BODY",BODY,{"disambiguationData":[OSD([sQuery(id+"F0.wireOp",EDGE,"E9.4.0.19")])]});
            var Q135;
            Q135=makeQuery(id+"F2.opExtrude","SWEPT_BODY",BODY,{"disambiguationData":[OSD([sQuery(id+"F0.wireOp",EDGE,"E9.4.0.20")])]});
            var Q136;
            Q136=makeQuery(id+"F2.opExtrude","SWEPT_BODY",BODY,{"disambiguationData":[OSD([sQuery(id+"F0.wireOp",EDGE,"E9.4.0.21")])]});
            var Q137;
            Q137=makeQuery(id+"F2.opExtrude","SWEPT_BODY",BODY,{"disambiguationData":[OSD([sQuery(id+"F0.wireOp",EDGE,"E9.4.0.22")])]});
            var Q138;
            Q138=makeQuery(id+"F2.opExtrude","SWEPT_BODY",BODY,{"disambiguationData":[OSD([sQuery(id+"F0.wireOp",EDGE,"E9.4.0.23")])]});
            var Q139;
            Q139=makeQuery(id+"F2.opExtrude","SWEPT_BODY",BODY,{"disambiguationData":[OSD([sQuery(id+"F0.wireOp",EDGE,"E9.5.0.0")])]});
            var Q140;
            Q140=makeQuery(id+"F2.opExtrude","SWEPT_BODY",BODY,{"disambiguationData":[OSD([sQuery(id+"F0.wireOp",EDGE,"E9.5.0.1")])]});
            var Q141;
            Q141=makeQuery(id+"F2.opExtrude","SWEPT_BODY",BODY,{"disambiguationData":[OSD([sQuery(id+"F0.wireOp",EDGE,"E9.5.0.2")])]});
            var Q142;
            Q142=makeQuery(id+"F2.opExtrude","SWEPT_BODY",BODY,{"disambiguationData":[OSD([sQuery(id+"F0.wireOp",EDGE,"E9.5.0.3")])]});
            var Q143;
            Q143=makeQuery(id+"F2.opExtrude","SWEPT_BODY",BODY,{"disambiguationData":[OSD([sQuery(id+"F0.wireOp",EDGE,"E9.5.0.4")])]});
            var Q144;
            Q144=makeQuery(id+"F2.opExtrude","SWEPT_BODY",BODY,{"disambiguationData":[OSD([sQuery(id+"F0.wireOp",EDGE,"E9.5.0.5")])]});
            var Q145;
            Q145=makeQuery(id+"F2.opExtrude","SWEPT_BODY",BODY,{"disambiguationData":[OSD([sQuery(id+"F0.wireOp",EDGE,"E9.5.0.6")])]});
            var Q146;
            Q146=makeQuery(id+"F2.opExtrude","SWEPT_BODY",BODY,{"disambiguationData":[OSD([sQuery(id+"F0.wireOp",EDGE,"E9.5.0.7")])]});
            var Q147;
            Q147=makeQuery(id+"F2.opExtrude","SWEPT_BODY",BODY,{"disambiguationData":[OSD([sQuery(id+"F0.wireOp",EDGE,"E9.5.0.8")])]});
            var Q148;
            Q148=makeQuery(id+"F2.opExtrude","SWEPT_BODY",BODY,{"disambiguationData":[OSD([sQuery(id+"F0.wireOp",EDGE,"E9.5.0.9")])]});
            var Q149;
            Q149=makeQuery(id+"F2.opExtrude","SWEPT_BODY",BODY,{"disambiguationData":[OSD([sQuery(id+"F0.wireOp",EDGE,"E9.5.0.10")])]});
            var Q150;
            Q150=makeQuery(id+"F2.opExtrude","SWEPT_BODY",BODY,{"disambiguationData":[OSD([sQuery(id+"F0.wireOp",EDGE,"E9.5.0.11")])]});
            var Q151;
            Q151=makeQuery(id+"F2.opExtrude","SWEPT_BODY",BODY,{"disambiguationData":[OSD([sQuery(id+"F0.wireOp",EDGE,"E9.5.0.12")])]});
            var Q152;
            Q152=makeQuery(id+"F2.opExtrude","SWEPT_BODY",BODY,{"disambiguationData":[OSD([sQuery(id+"F0.wireOp",EDGE,"E9.5.0.13")])]});
            var Q153;
            Q153=makeQuery(id+"F2.opExtrude","SWEPT_BODY",BODY,{"disambiguationData":[OSD([sQuery(id+"F0.wireOp",EDGE,"E9.5.0.14")])]});
            var Q154;
            Q154=makeQuery(id+"F2.opExtrude","SWEPT_BODY",BODY,{"disambiguationData":[OSD([sQuery(id+"F0.wireOp",EDGE,"E9.5.0.15")])]});
            var Q155;
            Q155=makeQuery(id+"F2.opExtrude","SWEPT_BODY",BODY,{"disambiguationData":[OSD([sQuery(id+"F0.wireOp",EDGE,"E9.5.0.16")])]});
            var Q156;
            Q156=makeQuery(id+"F2.opExtrude","SWEPT_BODY",BODY,{"disambiguationData":[OSD([sQuery(id+"F0.wireOp",EDGE,"E9.5.0.17")])]});
            var Q157;
            Q157=makeQuery(id+"F2.opExtrude","SWEPT_BODY",BODY,{"disambiguationData":[OSD([sQuery(id+"F0.wireOp",EDGE,"E9.5.0.18")])]});
            var Q158;
            Q158=makeQuery(id+"F2.opExtrude","SWEPT_BODY",BODY,{"disambiguationData":[OSD([sQuery(id+"F0.wireOp",EDGE,"E9.5.0.19")])]});
            var Q159;
            Q159=makeQuery(id+"F2.opExtrude","SWEPT_BODY",BODY,{"disambiguationData":[OSD([sQuery(id+"F0.wireOp",EDGE,"E9.5.0.20")])]});
            var Q160;
            Q160=makeQuery(id+"F2.opExtrude","SWEPT_BODY",BODY,{"disambiguationData":[OSD([sQuery(id+"F0.wireOp",EDGE,"E9.5.0.21")])]});
            var Q161;
            Q161=makeQuery(id+"F2.opExtrude","SWEPT_BODY",BODY,{"disambiguationData":[OSD([sQuery(id+"F0.wireOp",EDGE,"E9.5.0.22")])]});
            var Q162;
            Q162=makeQuery(id+"F2.opExtrude","SWEPT_BODY",BODY,{"disambiguationData":[OSD([sQuery(id+"F0.wireOp",EDGE,"E9.5.0.23")])]});
            var Q163;
            Q163=makeQuery(id+"F2.opExtrude","SWEPT_BODY",BODY,{"disambiguationData":[OSD([sQuery(id+"F0.wireOp",EDGE,"E9.6.0.0")])]});
            var Q164;
            Q164=makeQuery(id+"F2.opExtrude","SWEPT_BODY",BODY,{"disambiguationData":[OSD([sQuery(id+"F0.wireOp",EDGE,"E9.6.0.1")])]});
            var Q165;
            Q165=makeQuery(id+"F2.opExtrude","SWEPT_BODY",BODY,{"disambiguationData":[OSD([sQuery(id+"F0.wireOp",EDGE,"E9.6.0.2")])]});
            var Q166;
            Q166=makeQuery(id+"F2.opExtrude","SWEPT_BODY",BODY,{"disambiguationData":[OSD([sQuery(id+"F0.wireOp",EDGE,"E9.6.0.3")])]});
            var Q167;
            Q167=makeQuery(id+"F2.opExtrude","SWEPT_BODY",BODY,{"disambiguationData":[OSD([sQuery(id+"F0.wireOp",EDGE,"E9.6.0.4")])]});
            var Q168;
            Q168=makeQuery(id+"F2.opExtrude","SWEPT_BODY",BODY,{"disambiguationData":[OSD([sQuery(id+"F0.wireOp",EDGE,"E9.6.0.5")])]});
            var Q169;
            Q169=makeQuery(id+"F2.opExtrude","SWEPT_BODY",BODY,{"disambiguationData":[OSD([sQuery(id+"F0.wireOp",EDGE,"E9.6.0.6")])]});
            var Q170;
            Q170=makeQuery(id+"F2.opExtrude","SWEPT_BODY",BODY,{"disambiguationData":[OSD([sQuery(id+"F0.wireOp",EDGE,"E9.6.0.7")])]});
            var Q171;
            Q171=makeQuery(id+"F2.opExtrude","SWEPT_BODY",BODY,{"disambiguationData":[OSD([sQuery(id+"F0.wireOp",EDGE,"E9.6.0.8")])]});
            var Q172;
            Q172=makeQuery(id+"F2.opExtrude","SWEPT_BODY",BODY,{"disambiguationData":[OSD([sQuery(id+"F0.wireOp",EDGE,"E9.6.0.9")])]});
            var Q173;
            Q173=makeQuery(id+"F2.opExtrude","SWEPT_BODY",BODY,{"disambiguationData":[OSD([sQuery(id+"F0.wireOp",EDGE,"E9.6.0.10")])]});
            var Q174;
            Q174=makeQuery(id+"F2.opExtrude","SWEPT_BODY",BODY,{"disambiguationData":[OSD([sQuery(id+"F0.wireOp",EDGE,"E9.6.0.11")])]});
            var Q175;
            Q175=makeQuery(id+"F2.opExtrude","SWEPT_BODY",BODY,{"disambiguationData":[OSD([sQuery(id+"F0.wireOp",EDGE,"E9.6.0.12")])]});
            var Q176;
            Q176=makeQuery(id+"F2.opExtrude","SWEPT_BODY",BODY,{"disambiguationData":[OSD([sQuery(id+"F0.wireOp",EDGE,"E9.6.0.13")])]});
            var Q177;
            Q177=makeQuery(id+"F2.opExtrude","SWEPT_BODY",BODY,{"disambiguationData":[OSD([sQuery(id+"F0.wireOp",EDGE,"E9.6.0.14")])]});
            var Q178;
            Q178=makeQuery(id+"F2.opExtrude","SWEPT_BODY",BODY,{"disambiguationData":[OSD([sQuery(id+"F0.wireOp",EDGE,"E9.6.0.15")])]});
            var Q179;
            Q179=makeQuery(id+"F2.opExtrude","SWEPT_BODY",BODY,{"disambiguationData":[OSD([sQuery(id+"F0.wireOp",EDGE,"E9.6.0.16")])]});
            var Q180;
            Q180=makeQuery(id+"F2.opExtrude","SWEPT_BODY",BODY,{"disambiguationData":[OSD([sQuery(id+"F0.wireOp",EDGE,"E9.6.0.17")])]});
            var Q181;
            Q181=makeQuery(id+"F2.opExtrude","SWEPT_BODY",BODY,{"disambiguationData":[OSD([sQuery(id+"F0.wireOp",EDGE,"E9.6.0.18")])]});
            var Q182;
            Q182=makeQuery(id+"F2.opExtrude","SWEPT_BODY",BODY,{"disambiguationData":[OSD([sQuery(id+"F0.wireOp",EDGE,"E9.6.0.19")])]});
            var Q183;
            Q183=makeQuery(id+"F2.opExtrude","SWEPT_BODY",BODY,{"disambiguationData":[OSD([sQuery(id+"F0.wireOp",EDGE,"E9.6.0.20")])]});
            var Q184;
            Q184=makeQuery(id+"F2.opExtrude","SWEPT_BODY",BODY,{"disambiguationData":[OSD([sQuery(id+"F0.wireOp",EDGE,"E9.6.0.21")])]});
            var Q185;
            Q185=makeQuery(id+"F2.opExtrude","SWEPT_BODY",BODY,{"disambiguationData":[OSD([sQuery(id+"F0.wireOp",EDGE,"E9.6.0.22")])]});
            var Q186;
            Q186=makeQuery(id+"F2.opExtrude","SWEPT_BODY",BODY,{"disambiguationData":[OSD([sQuery(id+"F0.wireOp",EDGE,"E9.6.0.23")])]});
            var Q187;
            Q187=makeQuery(id+"F2.opExtrude","SWEPT_BODY",BODY,{"disambiguationData":[OSD([sQuery(id+"F0.wireOp",EDGE,"E9.7.0.0")])]});
            var Q188;
            Q188=makeQuery(id+"F2.opExtrude","SWEPT_BODY",BODY,{"disambiguationData":[OSD([sQuery(id+"F0.wireOp",EDGE,"E9.7.0.1")])]});
            var Q189;
            Q189=makeQuery(id+"F2.opExtrude","SWEPT_BODY",BODY,{"disambiguationData":[OSD([sQuery(id+"F0.wireOp",EDGE,"E9.7.0.2")])]});
            var Q190;
            Q190=makeQuery(id+"F2.opExtrude","SWEPT_BODY",BODY,{"disambiguationData":[OSD([sQuery(id+"F0.wireOp",EDGE,"E9.7.0.3")])]});
            var Q191;
            Q191=makeQuery(id+"F2.opExtrude","SWEPT_BODY",BODY,{"disambiguationData":[OSD([sQuery(id+"F0.wireOp",EDGE,"E9.7.0.4")])]});
            var Q192;
            Q192=makeQuery(id+"F2.opExtrude","SWEPT_BODY",BODY,{"disambiguationData":[OSD([sQuery(id+"F0.wireOp",EDGE,"E9.7.0.5")])]});
            var Q193;
            Q193=makeQuery(id+"F2.opExtrude","SWEPT_BODY",BODY,{"disambiguationData":[OSD([sQuery(id+"F0.wireOp",EDGE,"E9.7.0.6")])]});
            var Q194;
            Q194=makeQuery(id+"F2.opExtrude","SWEPT_BODY",BODY,{"disambiguationData":[OSD([sQuery(id+"F0.wireOp",EDGE,"E9.7.0.7")])]});
            var Q195;
            Q195=makeQuery(id+"F2.opExtrude","SWEPT_BODY",BODY,{"disambiguationData":[OSD([sQuery(id+"F0.wireOp",EDGE,"E9.7.0.8")])]});
            var Q196;
            Q196=makeQuery(id+"F2.opExtrude","SWEPT_BODY",BODY,{"disambiguationData":[OSD([sQuery(id+"F0.wireOp",EDGE,"E9.7.0.9")])]});
            var Q197;
            Q197=makeQuery(id+"F2.opExtrude","SWEPT_BODY",BODY,{"disambiguationData":[OSD([sQuery(id+"F0.wireOp",EDGE,"E9.7.0.10")])]});
            var Q198;
            Q198=makeQuery(id+"F2.opExtrude","SWEPT_BODY",BODY,{"disambiguationData":[OSD([sQuery(id+"F0.wireOp",EDGE,"E9.7.0.11")])]});
            var Q199;
            Q199=makeQuery(id+"F2.opExtrude","SWEPT_BODY",BODY,{"disambiguationData":[OSD([sQuery(id+"F0.wireOp",EDGE,"E9.7.0.12")])]});
            var Q200;
            Q200=makeQuery(id+"F2.opExtrude","SWEPT_BODY",BODY,{"disambiguationData":[OSD([sQuery(id+"F0.wireOp",EDGE,"E9.7.0.13")])]});
            var Q201;
            Q201=makeQuery(id+"F2.opExtrude","SWEPT_BODY",BODY,{"disambiguationData":[OSD([sQuery(id+"F0.wireOp",EDGE,"E9.7.0.14")])]});
            var Q202;
            Q202=makeQuery(id+"F2.opExtrude","SWEPT_BODY",BODY,{"disambiguationData":[OSD([sQuery(id+"F0.wireOp",EDGE,"E9.7.0.15")])]});
            var Q203;
            Q203=makeQuery(id+"F2.opExtrude","SWEPT_BODY",BODY,{"disambiguationData":[OSD([sQuery(id+"F0.wireOp",EDGE,"E9.7.0.16")])]});
            var Q204;
            Q204=makeQuery(id+"F2.opExtrude","SWEPT_BODY",BODY,{"disambiguationData":[OSD([sQuery(id+"F0.wireOp",EDGE,"E9.7.0.17")])]});
            var Q205;
            Q205=makeQuery(id+"F2.opExtrude","SWEPT_BODY",BODY,{"disambiguationData":[OSD([sQuery(id+"F0.wireOp",EDGE,"E9.7.0.18")])]});
            var Q206;
            Q206=makeQuery(id+"F2.opExtrude","SWEPT_BODY",BODY,{"disambiguationData":[OSD([sQuery(id+"F0.wireOp",EDGE,"E9.7.0.19")])]});
            var Q207;
            Q207=makeQuery(id+"F2.opExtrude","SWEPT_BODY",BODY,{"disambiguationData":[OSD([sQuery(id+"F0.wireOp",EDGE,"E9.7.0.20")])]});
            var Q208;
            Q208=makeQuery(id+"F2.opExtrude","SWEPT_BODY",BODY,{"disambiguationData":[OSD([sQuery(id+"F0.wireOp",EDGE,"E9.7.0.21")])]});
            var Q209;
            Q209=makeQuery(id+"F2.opExtrude","SWEPT_BODY",BODY,{"disambiguationData":[OSD([sQuery(id+"F0.wireOp",EDGE,"E9.7.0.22")])]});
            var Q210;
            Q210=makeQuery(id+"F2.opExtrude","SWEPT_BODY",BODY,{"disambiguationData":[OSD([sQuery(id+"F0.wireOp",EDGE,"E9.7.0.23")])]});
            var Q211;
            Q211=makeQuery(id+"F2.opExtrude","SWEPT_BODY",BODY,{"disambiguationData":[OSD([sQuery(id+"F0.wireOp",EDGE,"E9.8.0.0")])]});
            var Q212;
            Q212=makeQuery(id+"F2.opExtrude","SWEPT_BODY",BODY,{"disambiguationData":[OSD([sQuery(id+"F0.wireOp",EDGE,"E9.8.0.1")])]});
            var Q213;
            Q213=makeQuery(id+"F2.opExtrude","SWEPT_BODY",BODY,{"disambiguationData":[OSD([sQuery(id+"F0.wireOp",EDGE,"E9.8.0.2")])]});
            var Q214;
            Q214=makeQuery(id+"F2.opExtrude","SWEPT_BODY",BODY,{"disambiguationData":[OSD([sQuery(id+"F0.wireOp",EDGE,"E9.8.0.3")])]});
            var Q215;
            Q215=makeQuery(id+"F2.opExtrude","SWEPT_BODY",BODY,{"disambiguationData":[OSD([sQuery(id+"F0.wireOp",EDGE,"E9.8.0.4")])]});
            var Q216;
            Q216=makeQuery(id+"F2.opExtrude","SWEPT_BODY",BODY,{"disambiguationData":[OSD([sQuery(id+"F0.wireOp",EDGE,"E9.8.0.5")])]});
            var Q217;
            Q217=makeQuery(id+"F2.opExtrude","SWEPT_BODY",BODY,{"disambiguationData":[OSD([sQuery(id+"F0.wireOp",EDGE,"E9.8.0.6")])]});
            var Q218;
            Q218=makeQuery(id+"F2.opExtrude","SWEPT_BODY",BODY,{"disambiguationData":[OSD([sQuery(id+"F0.wireOp",EDGE,"E9.8.0.7")])]});
            var Q219;
            Q219=makeQuery(id+"F2.opExtrude","SWEPT_BODY",BODY,{"disambiguationData":[OSD([sQuery(id+"F0.wireOp",EDGE,"E9.8.0.8")])]});
            var Q220;
            Q220=makeQuery(id+"F2.opExtrude","SWEPT_BODY",BODY,{"disambiguationData":[OSD([sQuery(id+"F0.wireOp",EDGE,"E9.8.0.9")])]});
            var Q221;
            Q221=makeQuery(id+"F2.opExtrude","SWEPT_BODY",BODY,{"disambiguationData":[OSD([sQuery(id+"F0.wireOp",EDGE,"E9.8.0.10")])]});
            var Q222;
            Q222=makeQuery(id+"F2.opExtrude","SWEPT_BODY",BODY,{"disambiguationData":[OSD([sQuery(id+"F0.wireOp",EDGE,"E9.8.0.11")])]});
            var Q223;
            Q223=makeQuery(id+"F2.opExtrude","SWEPT_BODY",BODY,{"disambiguationData":[OSD([sQuery(id+"F0.wireOp",EDGE,"E9.8.0.12")])]});
            var Q224;
            Q224=makeQuery(id+"F2.opExtrude","SWEPT_BODY",BODY,{"disambiguationData":[OSD([sQuery(id+"F0.wireOp",EDGE,"E9.8.0.13")])]});
            var Q225;
            Q225=makeQuery(id+"F2.opExtrude","SWEPT_BODY",BODY,{"disambiguationData":[OSD([sQuery(id+"F0.wireOp",EDGE,"E9.8.0.14")])]});
            var Q226;
            Q226=makeQuery(id+"F2.opExtrude","SWEPT_BODY",BODY,{"disambiguationData":[OSD([sQuery(id+"F0.wireOp",EDGE,"E9.8.0.15")])]});
            var Q227;
            Q227=makeQuery(id+"F2.opExtrude","SWEPT_BODY",BODY,{"disambiguationData":[OSD([sQuery(id+"F0.wireOp",EDGE,"E9.8.0.16")])]});
            var Q228;
            Q228=makeQuery(id+"F2.opExtrude","SWEPT_BODY",BODY,{"disambiguationData":[OSD([sQuery(id+"F0.wireOp",EDGE,"E9.8.0.17")])]});
            var Q229;
            Q229=makeQuery(id+"F2.opExtrude","SWEPT_BODY",BODY,{"disambiguationData":[OSD([sQuery(id+"F0.wireOp",EDGE,"E9.8.0.18")])]});
            var Q230;
            Q230=makeQuery(id+"F2.opExtrude","SWEPT_BODY",BODY,{"disambiguationData":[OSD([sQuery(id+"F0.wireOp",EDGE,"E9.8.0.19")])]});
            var Q231;
            Q231=makeQuery(id+"F2.opExtrude","SWEPT_BODY",BODY,{"disambiguationData":[OSD([sQuery(id+"F0.wireOp",EDGE,"E9.8.0.20")])]});
            var Q232;
            Q232=makeQuery(id+"F2.opExtrude","SWEPT_BODY",BODY,{"disambiguationData":[OSD([sQuery(id+"F0.wireOp",EDGE,"E9.8.0.21")])]});
            var Q233;
            Q233=makeQuery(id+"F2.opExtrude","SWEPT_BODY",BODY,{"disambiguationData":[OSD([sQuery(id+"F0.wireOp",EDGE,"E9.8.0.22")])]});
            var Q234;
            Q234=makeQuery(id+"F2.opExtrude","SWEPT_BODY",BODY,{"disambiguationData":[OSD([sQuery(id+"F0.wireOp",EDGE,"E9.8.0.23")])]});
            var Q235;
            Q235=makeQuery(id+"F2.opExtrude","SWEPT_BODY",BODY,{"disambiguationData":[OSD([sQuery(id+"F0.wireOp",EDGE,"E9.9.0.0")])]});
            var Q236;
            Q236=makeQuery(id+"F2.opExtrude","SWEPT_BODY",BODY,{"disambiguationData":[OSD([sQuery(id+"F0.wireOp",EDGE,"E9.9.0.1")])]});
            var Q237;
            Q237=makeQuery(id+"F2.opExtrude","SWEPT_BODY",BODY,{"disambiguationData":[OSD([sQuery(id+"F0.wireOp",EDGE,"E9.9.0.2")])]});
            var Q238;
            Q238=makeQuery(id+"F2.opExtrude","SWEPT_BODY",BODY,{"disambiguationData":[OSD([sQuery(id+"F0.wireOp",EDGE,"E9.9.0.3")])]});
            var Q239;
            Q239=makeQuery(id+"F2.opExtrude","SWEPT_BODY",BODY,{"disambiguationData":[OSD([sQuery(id+"F0.wireOp",EDGE,"E9.9.0.4")])]});
            var Q240;
            Q240=makeQuery(id+"F2.opExtrude","SWEPT_BODY",BODY,{"disambiguationData":[OSD([sQuery(id+"F0.wireOp",EDGE,"E9.9.0.5")])]});
            var Q241;
            Q241=makeQuery(id+"F2.opExtrude","SWEPT_BODY",BODY,{"disambiguationData":[OSD([sQuery(id+"F0.wireOp",EDGE,"E9.9.0.6")])]});
            var Q242;
            Q242=makeQuery(id+"F2.opExtrude","SWEPT_BODY",BODY,{"disambiguationData":[OSD([sQuery(id+"F0.wireOp",EDGE,"E9.9.0.7")])]});
            var Q243;
            Q243=makeQuery(id+"F2.opExtrude","SWEPT_BODY",BODY,{"disambiguationData":[OSD([sQuery(id+"F0.wireOp",EDGE,"E9.9.0.8")])]});
            var Q244;
            Q244=makeQuery(id+"F2.opExtrude","SWEPT_BODY",BODY,{"disambiguationData":[OSD([sQuery(id+"F0.wireOp",EDGE,"E9.9.0.9")])]});
            var Q245;
            Q245=makeQuery(id+"F2.opExtrude","SWEPT_BODY",BODY,{"disambiguationData":[OSD([sQuery(id+"F0.wireOp",EDGE,"E9.9.0.10")])]});
            var Q246;
            Q246=makeQuery(id+"F2.opExtrude","SWEPT_BODY",BODY,{"disambiguationData":[OSD([sQuery(id+"F0.wireOp",EDGE,"E9.9.0.11")])]});
            var Q247;
            Q247=makeQuery(id+"F2.opExtrude","SWEPT_BODY",BODY,{"disambiguationData":[OSD([sQuery(id+"F0.wireOp",EDGE,"E9.9.0.12")])]});
            var Q248;
            Q248=makeQuery(id+"F2.opExtrude","SWEPT_BODY",BODY,{"disambiguationData":[OSD([sQuery(id+"F0.wireOp",EDGE,"E9.9.0.13")])]});
            var Q249;
            Q249=makeQuery(id+"F2.opExtrude","SWEPT_BODY",BODY,{"disambiguationData":[OSD([sQuery(id+"F0.wireOp",EDGE,"E9.9.0.14")])]});
            var Q250;
            Q250=makeQuery(id+"F2.opExtrude","SWEPT_BODY",BODY,{"disambiguationData":[OSD([sQuery(id+"F0.wireOp",EDGE,"E9.9.0.15")])]});
            var Q251;
            Q251=makeQuery(id+"F2.opExtrude","SWEPT_BODY",BODY,{"disambiguationData":[OSD([sQuery(id+"F0.wireOp",EDGE,"E9.9.0.16")])]});
            var Q252;
            Q252=makeQuery(id+"F2.opExtrude","SWEPT_BODY",BODY,{"disambiguationData":[OSD([sQuery(id+"F0.wireOp",EDGE,"E9.9.0.17")])]});
            var Q253;
            Q253=makeQuery(id+"F2.opExtrude","SWEPT_BODY",BODY,{"disambiguationData":[OSD([sQuery(id+"F0.wireOp",EDGE,"E9.9.0.18")])]});
            var Q254;
            Q254=makeQuery(id+"F2.opExtrude","SWEPT_BODY",BODY,{"disambiguationData":[OSD([sQuery(id+"F0.wireOp",EDGE,"E9.9.0.19")])]});
            var Q255;
            Q255=makeQuery(id+"F2.opExtrude","SWEPT_BODY",BODY,{"disambiguationData":[OSD([sQuery(id+"F0.wireOp",EDGE,"E9.9.0.20")])]});
            var Q256;
            Q256=makeQuery(id+"F2.opExtrude","SWEPT_BODY",BODY,{"disambiguationData":[OSD([sQuery(id+"F0.wireOp",EDGE,"E9.9.0.21")])]});
            var Q257;
            Q257=makeQuery(id+"F2.opExtrude","SWEPT_BODY",BODY,{"disambiguationData":[OSD([sQuery(id+"F0.wireOp",EDGE,"E9.9.0.22")])]});
            var Q258;
            Q258=makeQuery(id+"F2.opExtrude","SWEPT_BODY",BODY,{"disambiguationData":[OSD([sQuery(id+"F0.wireOp",EDGE,"E9.9.0.23")])]});
            var Q259;
            Q259=makeQuery(id+"F2.opExtrude","SWEPT_BODY",BODY,{"disambiguationData":[OSD([sQuery(id+"F0.wireOp",EDGE,"E9.10.0.0")])]});
            var Q260;
            Q260=makeQuery(id+"F2.opExtrude","SWEPT_BODY",BODY,{"disambiguationData":[OSD([sQuery(id+"F0.wireOp",EDGE,"E9.10.0.1")])]});
            var Q261;
            Q261=makeQuery(id+"F2.opExtrude","SWEPT_BODY",BODY,{"disambiguationData":[OSD([sQuery(id+"F0.wireOp",EDGE,"E9.10.0.2")])]});
            var Q262;
            Q262=makeQuery(id+"F2.opExtrude","SWEPT_BODY",BODY,{"disambiguationData":[OSD([sQuery(id+"F0.wireOp",EDGE,"E9.10.0.3")])]});
            var Q263;
            Q263=makeQuery(id+"F2.opExtrude","SWEPT_BODY",BODY,{"disambiguationData":[OSD([sQuery(id+"F0.wireOp",EDGE,"E9.10.0.4")])]});
            var Q264;
            Q264=makeQuery(id+"F2.opExtrude","SWEPT_BODY",BODY,{"disambiguationData":[OSD([sQuery(id+"F0.wireOp",EDGE,"E9.10.0.5")])]});
            var Q265;
            Q265=makeQuery(id+"F2.opExtrude","SWEPT_BODY",BODY,{"disambiguationData":[OSD([sQuery(id+"F0.wireOp",EDGE,"E9.10.0.6")])]});
            var Q266;
            Q266=makeQuery(id+"F2.opExtrude","SWEPT_BODY",BODY,{"disambiguationData":[OSD([sQuery(id+"F0.wireOp",EDGE,"E9.10.0.7")])]});
            var Q267;
            Q267=makeQuery(id+"F2.opExtrude","SWEPT_BODY",BODY,{"disambiguationData":[OSD([sQuery(id+"F0.wireOp",EDGE,"E9.10.0.8")])]});
            var Q268;
            Q268=makeQuery(id+"F2.opExtrude","SWEPT_BODY",BODY,{"disambiguationData":[OSD([sQuery(id+"F0.wireOp",EDGE,"E9.10.0.9")])]});
            var Q269;
            Q269=makeQuery(id+"F2.opExtrude","SWEPT_BODY",BODY,{"disambiguationData":[OSD([sQuery(id+"F0.wireOp",EDGE,"E9.10.0.10")])]});
            var Q270;
            Q270=makeQuery(id+"F2.opExtrude","SWEPT_BODY",BODY,{"disambiguationData":[OSD([sQuery(id+"F0.wireOp",EDGE,"E9.10.0.11")])]});
            var Q271;
            Q271=makeQuery(id+"F2.opExtrude","SWEPT_BODY",BODY,{"disambiguationData":[OSD([sQuery(id+"F0.wireOp",EDGE,"E9.10.0.12")])]});
            var Q272;
            Q272=makeQuery(id+"F2.opExtrude","SWEPT_BODY",BODY,{"disambiguationData":[OSD([sQuery(id+"F0.wireOp",EDGE,"E9.10.0.13")])]});
            var Q273;
            Q273=makeQuery(id+"F2.opExtrude","SWEPT_BODY",BODY,{"disambiguationData":[OSD([sQuery(id+"F0.wireOp",EDGE,"E9.10.0.14")])]});
            var Q274;
            Q274=makeQuery(id+"F2.opExtrude","SWEPT_BODY",BODY,{"disambiguationData":[OSD([sQuery(id+"F0.wireOp",EDGE,"E9.10.0.15")])]});
            var Q275;
            Q275=makeQuery(id+"F2.opExtrude","SWEPT_BODY",BODY,{"disambiguationData":[OSD([sQuery(id+"F0.wireOp",EDGE,"E9.10.0.16")])]});
            var Q276;
            Q276=makeQuery(id+"F2.opExtrude","SWEPT_BODY",BODY,{"disambiguationData":[OSD([sQuery(id+"F0.wireOp",EDGE,"E9.10.0.17")])]});
            var Q277;
            Q277=makeQuery(id+"F2.opExtrude","SWEPT_BODY",BODY,{"disambiguationData":[OSD([sQuery(id+"F0.wireOp",EDGE,"E9.10.0.18")])]});
            var Q278;
            Q278=makeQuery(id+"F2.opExtrude","SWEPT_BODY",BODY,{"disambiguationData":[OSD([sQuery(id+"F0.wireOp",EDGE,"E9.10.0.19")])]});
            var Q279;
            Q279=makeQuery(id+"F2.opExtrude","SWEPT_BODY",BODY,{"disambiguationData":[OSD([sQuery(id+"F0.wireOp",EDGE,"E9.10.0.20")])]});
            var Q280;
            Q280=makeQuery(id+"F2.opExtrude","SWEPT_BODY",BODY,{"disambiguationData":[OSD([sQuery(id+"F0.wireOp",EDGE,"E9.10.0.21")])]});
            var Q281;
            Q281=makeQuery(id+"F2.opExtrude","SWEPT_BODY",BODY,{"disambiguationData":[OSD([sQuery(id+"F0.wireOp",EDGE,"E9.10.0.22")])]});
            var Q282;
            Q282=makeQuery(id+"F2.opExtrude","SWEPT_BODY",BODY,{"disambiguationData":[OSD([sQuery(id+"F0.wireOp",EDGE,"E9.10.0.23")])]});
            var Q283;
            Q283=makeQuery(id+"F2.opExtrude","SWEPT_BODY",BODY,{"disambiguationData":[OSD([sQuery(id+"F0.wireOp",EDGE,"E9.11.0.0")])]});
            var Q284;
            Q284=makeQuery(id+"F2.opExtrude","SWEPT_BODY",BODY,{"disambiguationData":[OSD([sQuery(id+"F0.wireOp",EDGE,"E9.11.0.1")])]});
            var Q285;
            Q285=makeQuery(id+"F2.opExtrude","SWEPT_BODY",BODY,{"disambiguationData":[OSD([sQuery(id+"F0.wireOp",EDGE,"E9.11.0.2")])]});
            var Q286;
            Q286=makeQuery(id+"F2.opExtrude","SWEPT_BODY",BODY,{"disambiguationData":[OSD([sQuery(id+"F0.wireOp",EDGE,"E9.11.0.3")])]});
            var Q287;
            Q287=makeQuery(id+"F2.opExtrude","SWEPT_BODY",BODY,{"disambiguationData":[OSD([sQuery(id+"F0.wireOp",EDGE,"E9.11.0.4")])]});
            var Q288;
            Q288=makeQuery(id+"F2.opExtrude","SWEPT_BODY",BODY,{"disambiguationData":[OSD([sQuery(id+"F0.wireOp",EDGE,"E9.11.0.5")])]});
            var Q289;
            Q289=makeQuery(id+"F2.opExtrude","SWEPT_BODY",BODY,{"disambiguationData":[OSD([sQuery(id+"F0.wireOp",EDGE,"E9.11.0.6")])]});
            var Q290;
            Q290=makeQuery(id+"F2.opExtrude","SWEPT_BODY",BODY,{"disambiguationData":[OSD([sQuery(id+"F0.wireOp",EDGE,"E9.11.0.7")])]});
            var Q291;
            Q291=makeQuery(id+"F2.opExtrude","SWEPT_BODY",BODY,{"disambiguationData":[OSD([sQuery(id+"F0.wireOp",EDGE,"E9.11.0.8")])]});
            var Q292;
            Q292=makeQuery(id+"F2.opExtrude","SWEPT_BODY",BODY,{"disambiguationData":[OSD([sQuery(id+"F0.wireOp",EDGE,"E9.11.0.9")])]});
            var Q293;
            Q293=makeQuery(id+"F2.opExtrude","SWEPT_BODY",BODY,{"disambiguationData":[OSD([sQuery(id+"F0.wireOp",EDGE,"E9.11.0.10")])]});
            var Q294;
            Q294=makeQuery(id+"F2.opExtrude","SWEPT_BODY",BODY,{"disambiguationData":[OSD([sQuery(id+"F0.wireOp",EDGE,"E9.11.0.11")])]});
            var Q295;
            Q295=makeQuery(id+"F2.opExtrude","SWEPT_BODY",BODY,{"disambiguationData":[OSD([sQuery(id+"F0.wireOp",EDGE,"E9.11.0.12")])]});
            var Q296;
            Q296=makeQuery(id+"F2.opExtrude","SWEPT_BODY",BODY,{"disambiguationData":[OSD([sQuery(id+"F0.wireOp",EDGE,"E9.11.0.13")])]});
            var Q297;
            Q297=makeQuery(id+"F2.opExtrude","SWEPT_BODY",BODY,{"disambiguationData":[OSD([sQuery(id+"F0.wireOp",EDGE,"E9.11.0.14")])]});
            var Q298;
            Q298=makeQuery(id+"F2.opExtrude","SWEPT_BODY",BODY,{"disambiguationData":[OSD([sQuery(id+"F0.wireOp",EDGE,"E9.11.0.15")])]});
            var Q299;
            Q299=makeQuery(id+"F2.opExtrude","SWEPT_BODY",BODY,{"disambiguationData":[OSD([sQuery(id+"F0.wireOp",EDGE,"E9.11.0.16")])]});
            var Q300;
            Q300=makeQuery(id+"F2.opExtrude","SWEPT_BODY",BODY,{"disambiguationData":[OSD([sQuery(id+"F0.wireOp",EDGE,"E9.11.0.17")])]});
            var Q301;
            Q301=makeQuery(id+"F2.opExtrude","SWEPT_BODY",BODY,{"disambiguationData":[OSD([sQuery(id+"F0.wireOp",EDGE,"E9.11.0.18")])]});
            var Q302;
            Q302=makeQuery(id+"F2.opExtrude","SWEPT_BODY",BODY,{"disambiguationData":[OSD([sQuery(id+"F0.wireOp",EDGE,"E9.11.0.19")])]});
            var Q303;
            Q303=makeQuery(id+"F2.opExtrude","SWEPT_BODY",BODY,{"disambiguationData":[OSD([sQuery(id+"F0.wireOp",EDGE,"E9.11.0.20")])]});
            var Q304;
            Q304=makeQuery(id+"F2.opExtrude","SWEPT_BODY",BODY,{"disambiguationData":[OSD([sQuery(id+"F0.wireOp",EDGE,"E9.11.0.21")])]});
            var Q305;
            Q305=makeQuery(id+"F2.opExtrude","SWEPT_BODY",BODY,{"disambiguationData":[OSD([sQuery(id+"F0.wireOp",EDGE,"E9.11.0.22")])]});
            var Q306;
            Q306=makeQuery(id+"F2.opExtrude","SWEPT_BODY",BODY,{"disambiguationData":[OSD([sQuery(id+"F0.wireOp",EDGE,"E9.11.0.23")])]});
            var Q307;
            Q307=makeQuery(id+"F2.opExtrude","SWEPT_BODY",BODY,{"disambiguationData":[OSD([sQuery(id+"F0.wireOp",EDGE,"E9.12.0.0")])]});
            var Q308;
            Q308=makeQuery(id+"F2.opExtrude","SWEPT_BODY",BODY,{"disambiguationData":[OSD([sQuery(id+"F0.wireOp",EDGE,"E9.12.0.1")])]});
            var Q309;
            Q309=makeQuery(id+"F2.opExtrude","SWEPT_BODY",BODY,{"disambiguationData":[OSD([sQuery(id+"F0.wireOp",EDGE,"E9.12.0.2")])]});
            var Q310;
            Q310=makeQuery(id+"F2.opExtrude","SWEPT_BODY",BODY,{"disambiguationData":[OSD([sQuery(id+"F0.wireOp",EDGE,"E9.12.0.3")])]});
            var Q311;
            Q311=makeQuery(id+"F2.opExtrude","SWEPT_BODY",BODY,{"disambiguationData":[OSD([sQuery(id+"F0.wireOp",EDGE,"E9.12.0.4")])]});
            var Q312;
            Q312=makeQuery(id+"F2.opExtrude","SWEPT_BODY",BODY,{"disambiguationData":[OSD([sQuery(id+"F0.wireOp",EDGE,"E9.12.0.5")])]});
            var Q313;
            Q313=makeQuery(id+"F2.opExtrude","SWEPT_BODY",BODY,{"disambiguationData":[OSD([sQuery(id+"F0.wireOp",EDGE,"E9.12.0.6")])]});
            var Q314;
            Q314=makeQuery(id+"F2.opExtrude","SWEPT_BODY",BODY,{"disambiguationData":[OSD([sQuery(id+"F0.wireOp",EDGE,"E9.12.0.7")])]});
            var Q315;
            Q315=makeQuery(id+"F2.opExtrude","SWEPT_BODY",BODY,{"disambiguationData":[OSD([sQuery(id+"F0.wireOp",EDGE,"E9.12.0.8")])]});
            var Q316;
            Q316=makeQuery(id+"F2.opExtrude","SWEPT_BODY",BODY,{"disambiguationData":[OSD([sQuery(id+"F0.wireOp",EDGE,"E9.12.0.9")])]});
            var Q317;
            Q317=makeQuery(id+"F2.opExtrude","SWEPT_BODY",BODY,{"disambiguationData":[OSD([sQuery(id+"F0.wireOp",EDGE,"E9.12.0.10")])]});
            var Q318;
            Q318=makeQuery(id+"F2.opExtrude","SWEPT_BODY",BODY,{"disambiguationData":[OSD([sQuery(id+"F0.wireOp",EDGE,"E9.12.0.11")])]});
            var Q319;
            Q319=makeQuery(id+"F2.opExtrude","SWEPT_BODY",BODY,{"disambiguationData":[OSD([sQuery(id+"F0.wireOp",EDGE,"E9.12.0.12")])]});
            var Q320;
            Q320=makeQuery(id+"F2.opExtrude","SWEPT_BODY",BODY,{"disambiguationData":[OSD([sQuery(id+"F0.wireOp",EDGE,"E9.12.0.13")])]});
            var Q321;
            Q321=makeQuery(id+"F2.opExtrude","SWEPT_BODY",BODY,{"disambiguationData":[OSD([sQuery(id+"F0.wireOp",EDGE,"E9.12.0.14")])]});
            var Q322;
            Q322=makeQuery(id+"F2.opExtrude","SWEPT_BODY",BODY,{"disambiguationData":[OSD([sQuery(id+"F0.wireOp",EDGE,"E9.12.0.15")])]});
            var Q323;
            Q323=makeQuery(id+"F2.opExtrude","SWEPT_BODY",BODY,{"disambiguationData":[OSD([sQuery(id+"F0.wireOp",EDGE,"E9.12.0.16")])]});
            var Q324;
            Q324=makeQuery(id+"F2.opExtrude","SWEPT_BODY",BODY,{"disambiguationData":[OSD([sQuery(id+"F0.wireOp",EDGE,"E9.12.0.17")])]});
            var Q325;
            Q325=makeQuery(id+"F2.opExtrude","SWEPT_BODY",BODY,{"disambiguationData":[OSD([sQuery(id+"F0.wireOp",EDGE,"E9.12.0.18")])]});
            var Q326;
            Q326=makeQuery(id+"F2.opExtrude","SWEPT_BODY",BODY,{"disambiguationData":[OSD([sQuery(id+"F0.wireOp",EDGE,"E9.12.0.19")])]});
            var Q327;
            Q327=makeQuery(id+"F2.opExtrude","SWEPT_BODY",BODY,{"disambiguationData":[OSD([sQuery(id+"F0.wireOp",EDGE,"E9.12.0.20")])]});
            var Q328;
            Q328=makeQuery(id+"F2.opExtrude","SWEPT_BODY",BODY,{"disambiguationData":[OSD([sQuery(id+"F0.wireOp",EDGE,"E9.12.0.21")])]});
            var Q329;
            Q329=makeQuery(id+"F2.opExtrude","SWEPT_BODY",BODY,{"disambiguationData":[OSD([sQuery(id+"F0.wireOp",EDGE,"E9.12.0.22")])]});
            var Q330;
            Q330=makeQuery(id+"F2.opExtrude","SWEPT_BODY",BODY,{"disambiguationData":[OSD([sQuery(id+"F0.wireOp",EDGE,"E9.12.0.23")])]});
            var Q331;
            Q331=makeQuery(id+"F2.opExtrude","SWEPT_BODY",BODY,{"disambiguationData":[OSD([sQuery(id+"F0.wireOp",EDGE,"E9.13.0.0")])]});
            var Q332;
            Q332=makeQuery(id+"F2.opExtrude","SWEPT_BODY",BODY,{"disambiguationData":[OSD([sQuery(id+"F0.wireOp",EDGE,"E9.13.0.1")])]});
            var Q333;
            Q333=makeQuery(id+"F2.opExtrude","SWEPT_BODY",BODY,{"disambiguationData":[OSD([sQuery(id+"F0.wireOp",EDGE,"E9.13.0.2")])]});
            var Q334;
            Q334=makeQuery(id+"F2.opExtrude","SWEPT_BODY",BODY,{"disambiguationData":[OSD([sQuery(id+"F0.wireOp",EDGE,"E9.13.0.3")])]});
            var Q335;
            Q335=makeQuery(id+"F2.opExtrude","SWEPT_BODY",BODY,{"disambiguationData":[OSD([sQuery(id+"F0.wireOp",EDGE,"E9.13.0.4")])]});
            var Q336;
            Q336=makeQuery(id+"F2.opExtrude","SWEPT_BODY",BODY,{"disambiguationData":[OSD([sQuery(id+"F0.wireOp",EDGE,"E9.13.0.5")])]});
            var Q337;
            Q337=makeQuery(id+"F2.opExtrude","SWEPT_BODY",BODY,{"disambiguationData":[OSD([sQuery(id+"F0.wireOp",EDGE,"E9.13.0.6")])]});
            var Q338;
            Q338=makeQuery(id+"F2.opExtrude","SWEPT_BODY",BODY,{"disambiguationData":[OSD([sQuery(id+"F0.wireOp",EDGE,"E9.13.0.7")])]});
            var Q339;
            Q339=makeQuery(id+"F2.opExtrude","SWEPT_BODY",BODY,{"disambiguationData":[OSD([sQuery(id+"F0.wireOp",EDGE,"E9.13.0.8")])]});
            var Q340;
            Q340=makeQuery(id+"F2.opExtrude","SWEPT_BODY",BODY,{"disambiguationData":[OSD([sQuery(id+"F0.wireOp",EDGE,"E9.13.0.9")])]});
            var Q341;
            Q341=makeQuery(id+"F2.opExtrude","SWEPT_BODY",BODY,{"disambiguationData":[OSD([sQuery(id+"F0.wireOp",EDGE,"E9.13.0.10")])]});
            var Q342;
            Q342=makeQuery(id+"F2.opExtrude","SWEPT_BODY",BODY,{"disambiguationData":[OSD([sQuery(id+"F0.wireOp",EDGE,"E9.13.0.11")])]});
            var Q343;
            Q343=makeQuery(id+"F2.opExtrude","SWEPT_BODY",BODY,{"disambiguationData":[OSD([sQuery(id+"F0.wireOp",EDGE,"E9.13.0.12")])]});
            var Q344;
            Q344=makeQuery(id+"F2.opExtrude","SWEPT_BODY",BODY,{"disambiguationData":[OSD([sQuery(id+"F0.wireOp",EDGE,"E9.13.0.13")])]});
            var Q345;
            Q345=makeQuery(id+"F2.opExtrude","SWEPT_BODY",BODY,{"disambiguationData":[OSD([sQuery(id+"F0.wireOp",EDGE,"E9.13.0.14")])]});
            var Q346;
            Q346=makeQuery(id+"F2.opExtrude","SWEPT_BODY",BODY,{"disambiguationData":[OSD([sQuery(id+"F0.wireOp",EDGE,"E9.13.0.15")])]});
            var Q347;
            Q347=makeQuery(id+"F2.opExtrude","SWEPT_BODY",BODY,{"disambiguationData":[OSD([sQuery(id+"F0.wireOp",EDGE,"E9.13.0.16")])]});
            var Q348;
            Q348=makeQuery(id+"F2.opExtrude","SWEPT_BODY",BODY,{"disambiguationData":[OSD([sQuery(id+"F0.wireOp",EDGE,"E9.13.0.17")])]});
            var Q349;
            Q349=makeQuery(id+"F2.opExtrude","SWEPT_BODY",BODY,{"disambiguationData":[OSD([sQuery(id+"F0.wireOp",EDGE,"E9.13.0.18")])]});
            var Q350;
            Q350=makeQuery(id+"F2.opExtrude","SWEPT_BODY",BODY,{"disambiguationData":[OSD([sQuery(id+"F0.wireOp",EDGE,"E9.13.0.19")])]});
            var Q351;
            Q351=makeQuery(id+"F2.opExtrude","SWEPT_BODY",BODY,{"disambiguationData":[OSD([sQuery(id+"F0.wireOp",EDGE,"E9.13.0.20")])]});
            var Q352;
            Q352=makeQuery(id+"F2.opExtrude","SWEPT_BODY",BODY,{"disambiguationData":[OSD([sQuery(id+"F0.wireOp",EDGE,"E9.13.0.21")])]});
            var Q353;
            Q353=makeQuery(id+"F2.opExtrude","SWEPT_BODY",BODY,{"disambiguationData":[OSD([sQuery(id+"F0.wireOp",EDGE,"E9.13.0.22")])]});
            var Q354;
            Q354=makeQuery(id+"F2.opExtrude","SWEPT_BODY",BODY,{"disambiguationData":[OSD([sQuery(id+"F0.wireOp",EDGE,"E9.13.0.23")])]});
            var Q355;
            Q355=makeQuery(id+"F2.opExtrude","SWEPT_BODY",BODY,{"disambiguationData":[OSD([sQuery(id+"F0.wireOp",EDGE,"E9.14.0.0")])]});
            var Q356;
            Q356=makeQuery(id+"F2.opExtrude","SWEPT_BODY",BODY,{"disambiguationData":[OSD([sQuery(id+"F0.wireOp",EDGE,"E9.14.0.1")])]});
            var Q357;
            Q357=makeQuery(id+"F2.opExtrude","SWEPT_BODY",BODY,{"disambiguationData":[OSD([sQuery(id+"F0.wireOp",EDGE,"E9.14.0.2")])]});
            var Q358;
            Q358=makeQuery(id+"F2.opExtrude","SWEPT_BODY",BODY,{"disambiguationData":[OSD([sQuery(id+"F0.wireOp",EDGE,"E9.14.0.3")])]});
            var Q359;
            Q359=makeQuery(id+"F2.opExtrude","SWEPT_BODY",BODY,{"disambiguationData":[OSD([sQuery(id+"F0.wireOp",EDGE,"E9.14.0.4")])]});
            var Q360;
            Q360=makeQuery(id+"F2.opExtrude","SWEPT_BODY",BODY,{"disambiguationData":[OSD([sQuery(id+"F0.wireOp",EDGE,"E9.14.0.5")])]});
            var Q361;
            Q361=makeQuery(id+"F2.opExtrude","SWEPT_BODY",BODY,{"disambiguationData":[OSD([sQuery(id+"F0.wireOp",EDGE,"E9.14.0.6")])]});
            var Q362;
            Q362=makeQuery(id+"F2.opExtrude","SWEPT_BODY",BODY,{"disambiguationData":[OSD([sQuery(id+"F0.wireOp",EDGE,"E9.14.0.7")])]});
            var Q363;
            Q363=makeQuery(id+"F2.opExtrude","SWEPT_BODY",BODY,{"disambiguationData":[OSD([sQuery(id+"F0.wireOp",EDGE,"E9.14.0.8")])]});
            var Q364;
            Q364=makeQuery(id+"F2.opExtrude","SWEPT_BODY",BODY,{"disambiguationData":[OSD([sQuery(id+"F0.wireOp",EDGE,"E9.14.0.9")])]});
            var Q365;
            Q365=makeQuery(id+"F2.opExtrude","SWEPT_BODY",BODY,{"disambiguationData":[OSD([sQuery(id+"F0.wireOp",EDGE,"E9.14.0.10")])]});
            var Q366;
            Q366=makeQuery(id+"F2.opExtrude","SWEPT_BODY",BODY,{"disambiguationData":[OSD([sQuery(id+"F0.wireOp",EDGE,"E9.14.0.11")])]});
            var Q367;
            Q367=makeQuery(id+"F2.opExtrude","SWEPT_BODY",BODY,{"disambiguationData":[OSD([sQuery(id+"F0.wireOp",EDGE,"E9.14.0.12")])]});
            var Q368;
            Q368=makeQuery(id+"F2.opExtrude","SWEPT_BODY",BODY,{"disambiguationData":[OSD([sQuery(id+"F0.wireOp",EDGE,"E9.14.0.13")])]});
            var Q369;
            Q369=makeQuery(id+"F2.opExtrude","SWEPT_BODY",BODY,{"disambiguationData":[OSD([sQuery(id+"F0.wireOp",EDGE,"E9.14.0.14")])]});
            var Q370;
            Q370=makeQuery(id+"F2.opExtrude","SWEPT_BODY",BODY,{"disambiguationData":[OSD([sQuery(id+"F0.wireOp",EDGE,"E9.14.0.15")])]});
            var Q371;
            Q371=makeQuery(id+"F2.opExtrude","SWEPT_BODY",BODY,{"disambiguationData":[OSD([sQuery(id+"F0.wireOp",EDGE,"E9.14.0.16")])]});
            var Q372;
            Q372=makeQuery(id+"F2.opExtrude","SWEPT_BODY",BODY,{"disambiguationData":[OSD([sQuery(id+"F0.wireOp",EDGE,"E9.14.0.17")])]});
            var Q373;
            Q373=makeQuery(id+"F2.opExtrude","SWEPT_BODY",BODY,{"disambiguationData":[OSD([sQuery(id+"F0.wireOp",EDGE,"E9.14.0.18")])]});
            var Q374;
            Q374=makeQuery(id+"F2.opExtrude","SWEPT_BODY",BODY,{"disambiguationData":[OSD([sQuery(id+"F0.wireOp",EDGE,"E9.14.0.19")])]});
            var Q375;
            Q375=makeQuery(id+"F2.opExtrude","SWEPT_BODY",BODY,{"disambiguationData":[OSD([sQuery(id+"F0.wireOp",EDGE,"E9.14.0.20")])]});
            var Q376;
            Q376=makeQuery(id+"F2.opExtrude","SWEPT_BODY",BODY,{"disambiguationData":[OSD([sQuery(id+"F0.wireOp",EDGE,"E9.14.0.21")])]});
            var Q377;
            Q377=makeQuery(id+"F2.opExtrude","SWEPT_BODY",BODY,{"disambiguationData":[OSD([sQuery(id+"F0.wireOp",EDGE,"E9.14.0.22")])]});
            var Q378;
            Q378=makeQuery(id+"F2.opExtrude","SWEPT_BODY",BODY,{"disambiguationData":[OSD([sQuery(id+"F0.wireOp",EDGE,"E9.14.0.23")])]});
            transform(context, id + "F3", {"entities" : qUnion([Q0, Q1, Q2, Q3, Q4, Q5, Q6, Q7, Q8, Q9, Q10, Q11, Q12, Q13, Q14, Q15, Q16, Q17, Q18, Q19, Q20, Q21, Q22, Q23, Q24, Q25, Q26, Q27, Q28, Q29, Q30, Q31, Q32, Q33, Q34, Q35, Q36, Q37, Q38, Q39, Q40, Q41, Q42, Q43, Q44, Q45, Q46, Q47, Q48, Q49, Q50, Q51, Q52, Q53, Q54, Q55, Q56, Q57, Q58, Q59, Q60, Q61, Q62, Q63, Q64, Q65, Q66, Q67, Q68, Q69, Q70, Q71, Q72, Q73, Q74, Q75, Q76, Q77, Q78, Q79, Q80, Q81, Q82, Q83, Q84, Q85, Q86, Q87, Q88, Q89, Q90, Q91, Q92, Q93, Q94, Q95, Q96, Q97, Q98, Q99, Q100, Q101, Q102, Q103, Q104, Q105, Q106, Q107, Q108, Q109, Q110, Q111, Q112, Q113, Q114, Q115, Q116, Q117, Q118, Q119, Q120, Q121, Q122, Q123, Q124, Q125, Q126, Q127, Q128, Q129, Q130, Q131, Q132, Q133, Q134, Q135, Q136, Q137, Q138, Q139, Q140, Q141, Q142, Q143, Q144, Q145, Q146, Q147, Q148, Q149, Q150, Q151, Q152, Q153, Q154, Q155, Q156, Q157, Q158, Q159, Q160, Q161, Q162, Q163, Q164, Q165, Q166, Q167, Q168, Q169, Q170, Q171, Q172, Q173, Q174, Q175, Q176, Q177, Q178, Q179, Q180, Q181, Q182, Q183, Q184, Q185, Q186, Q187, Q188, Q189, Q190, Q191, Q192, Q193, Q194, Q195, Q196, Q197, Q198, Q199, Q200, Q201, Q202, Q203, Q204, Q205, Q206, Q207, Q208, Q209, Q210, Q211, Q212, Q213, Q214, Q215, Q216, Q217, Q218, Q219, Q220, Q221, Q222, Q223, Q224, Q225, Q226, Q227, Q228, Q229, Q230, Q231, Q232, Q233, Q234, Q235, Q236, Q237, Q238, Q239, Q240, Q241, Q242, Q243, Q244, Q245, Q246, Q247, Q248, Q249, Q250, Q251, Q252, Q253, Q254, Q255, Q256, Q257, Q258, Q259, Q260, Q261, Q262, Q263, Q264, Q265, Q266, Q267, Q268, Q269, Q270, Q271, Q272, Q273, Q274, Q275, Q276, Q277, Q278, Q279, Q280, Q281, Q282, Q283, Q284, Q285, Q286, Q287, Q288, Q289, Q290, Q291, Q292, Q293, Q294, Q295, Q296, Q297, Q298, Q299, Q300, Q301, Q302, Q303, Q304, Q305, Q306, Q307, Q308, Q309, Q310, Q311, Q312, Q313, Q314, Q315, Q316, Q317, Q318, Q319, Q320, Q321, Q322, Q323, Q324, Q325, Q326, Q327, Q328, Q329, Q330, Q331, Q332, Q333, Q334, Q335, Q336, Q337, Q338, Q339, Q340, Q341, Q342, Q343, Q344, Q345, Q346, Q347, Q348, Q349, Q350, Q351, Q352, Q353, Q354, Q355, Q356, Q357, Q358, Q359, Q360, Q361, Q362, Q363, Q364, Q365, Q366, Q367, Q368, Q369, Q370, Q371, Q372, Q373, Q374, Q375, Q376, Q377, Q378]), "transformType" : TransformType.TRANSLATION_3D, "dx" : 0 * mm, "dy" : 0 * mm, "dz" : -1 * mm, "makeCopy" : false});
        }
        {
            var Q0;
            Q0=qSketchRegion(id+"F1",true);
            extrude(context, id + "F4", {"entities" : qUnion([Q0]), "depth" : 1.6 * mm});
        }
        {
            var Q0;
            Q0=makeQuery(id+"F2.opExtrude","SWEPT_BODY",BODY,{"disambiguationData":[OSD([sQuery(id+"F0.wireOp",EDGE,"E0")])]});
            var Q1;
            Q1=makeQuery(id+"F2.opExtrude","SWEPT_BODY",BODY,{"disambiguationData":[OSD([sQuery(id+"F0.wireOp",EDGE,"E1")])]});
            var Q2;
            Q2=makeQuery(id+"F2.opExtrude","SWEPT_BODY",BODY,{"disambiguationData":[OSD([sQuery(id+"F0.wireOp",EDGE,"E2")])]});
            var Q3;
            Q3=makeQuery(id+"F2.opExtrude","SWEPT_BODY",BODY,{"disambiguationData":[OSD([sQuery(id+"F0.wireOp",EDGE,"E3")])]});
            var Q4;
            Q4=makeQuery(id+"F2.opExtrude","SWEPT_BODY",BODY,{"disambiguationData":[OSD([sQuery(id+"F0.wireOp",EDGE,"E4")])]});
            var Q5;
            Q5=makeQuery(id+"F2.opExtrude","SWEPT_BODY",BODY,{"disambiguationData":[OSD([sQuery(id+"F0.wireOp",EDGE,"E5.1.0.0")])]});
            var Q6;
            Q6=makeQuery(id+"F2.opExtrude","SWEPT_BODY",BODY,{"disambiguationData":[OSD([sQuery(id+"F0.wireOp",EDGE,"E5.2.0.0")])]});
            var Q7;
            Q7=makeQuery(id+"F2.opExtrude","SWEPT_BODY",BODY,{"disambiguationData":[OSD([sQuery(id+"F0.wireOp",EDGE,"E5.3.0.0")])]});
            var Q8;
            Q8=makeQuery(id+"F2.opExtrude","SWEPT_BODY",BODY,{"disambiguationData":[OSD([sQuery(id+"F0.wireOp",EDGE,"E5.4.0.0")])]});
            var Q9;
            Q9=makeQuery(id+"F2.opExtrude","SWEPT_BODY",BODY,{"disambiguationData":[OSD([sQuery(id+"F0.wireOp",EDGE,"E5.5.0.0")])]});
            var Q10;
            Q10=makeQuery(id+"F2.opExtrude","SWEPT_BODY",BODY,{"disambiguationData":[OSD([sQuery(id+"F0.wireOp",EDGE,"E5.6.0.0")])]});
            var Q11;
            Q11=makeQuery(id+"F2.opExtrude","SWEPT_BODY",BODY,{"disambiguationData":[OSD([sQuery(id+"F0.wireOp",EDGE,"E5.7.0.0")])]});
            var Q12;
            Q12=makeQuery(id+"F2.opExtrude","SWEPT_BODY",BODY,{"disambiguationData":[OSD([sQuery(id+"F0.wireOp",EDGE,"E5.8.0.0")])]});
            var Q13;
            Q13=makeQuery(id+"F2.opExtrude","SWEPT_BODY",BODY,{"disambiguationData":[OSD([sQuery(id+"F0.wireOp",EDGE,"E5.9.0.0")])]});
            var Q14;
            Q14=makeQuery(id+"F2.opExtrude","SWEPT_BODY",BODY,{"disambiguationData":[OSD([sQuery(id+"F0.wireOp",EDGE,"E5.10.0.0")])]});
            var Q15;
            Q15=makeQuery(id+"F2.opExtrude","SWEPT_BODY",BODY,{"disambiguationData":[OSD([sQuery(id+"F0.wireOp",EDGE,"E5.11.0.0")])]});
            var Q16;
            Q16=makeQuery(id+"F2.opExtrude","SWEPT_BODY",BODY,{"disambiguationData":[OSD([sQuery(id+"F0.wireOp",EDGE,"E5.12.0.0")])]});
            var Q17;
            Q17=makeQuery(id+"F2.opExtrude","SWEPT_BODY",BODY,{"disambiguationData":[OSD([sQuery(id+"F0.wireOp",EDGE,"E5.13.0.0")])]});
            var Q18;
            Q18=makeQuery(id+"F2.opExtrude","SWEPT_BODY",BODY,{"disambiguationData":[OSD([sQuery(id+"F0.wireOp",EDGE,"E5.14.0.0")])]});
            var Q19;
            Q19=makeQuery(id+"F2.opExtrude","SWEPT_BODY",BODY,{"disambiguationData":[OSD([sQuery(id+"F0.wireOp",EDGE,"E5.15.0.0")])]});
            var Q20;
            Q20=makeQuery(id+"F2.opExtrude","SWEPT_BODY",BODY,{"disambiguationData":[OSD([sQuery(id+"F0.wireOp",EDGE,"E5.16.0.0")])]});
            var Q21;
            Q21=makeQuery(id+"F2.opExtrude","SWEPT_BODY",BODY,{"disambiguationData":[OSD([sQuery(id+"F0.wireOp",EDGE,"E5.17.0.0")])]});
            var Q22;
            Q22=makeQuery(id+"F2.opExtrude","SWEPT_BODY",BODY,{"disambiguationData":[OSD([sQuery(id+"F0.wireOp",EDGE,"E5.18.0.0")])]});
            var Q23;
            Q23=makeQuery(id+"F2.opExtrude","SWEPT_BODY",BODY,{"disambiguationData":[OSD([sQuery(id+"F0.wireOp",EDGE,"E5.19.0.0")])]});
            var Q24;
            Q24=makeQuery(id+"F2.opExtrude","SWEPT_BODY",BODY,{"disambiguationData":[OSD([sQuery(id+"F0.wireOp",EDGE,"E5.20.0.0")])]});
            var Q25;
            Q25=makeQuery(id+"F2.opExtrude","SWEPT_BODY",BODY,{"disambiguationData":[OSD([sQuery(id+"F0.wireOp",EDGE,"E5.21.0.0")])]});
            var Q26;
            Q26=makeQuery(id+"F2.opExtrude","SWEPT_BODY",BODY,{"disambiguationData":[OSD([sQuery(id+"F0.wireOp",EDGE,"E5.22.0.0")])]});
            var Q27;
            Q27=makeQuery(id+"F2.opExtrude","SWEPT_BODY",BODY,{"disambiguationData":[OSD([sQuery(id+"F0.wireOp",EDGE,"E5.23.0.0")])]});
            var Q28;
            Q28=makeQuery(id+"F2.opExtrude","SWEPT_BODY",BODY,{"disambiguationData":[OSD([sQuery(id+"F0.wireOp",EDGE,"E5.24.0.0")])]});
            var Q29;
            Q29=makeQuery(id+"F2.opExtrude","SWEPT_BODY",BODY,{"disambiguationData":[OSD([sQuery(id+"F0.wireOp",EDGE,"E7.1.0.0")])]});
            var Q30;
            Q30=makeQuery(id+"F2.opExtrude","SWEPT_BODY",BODY,{"disambiguationData":[OSD([sQuery(id+"F0.wireOp",EDGE,"E7.2.0.0")])]});
            var Q31;
            Q31=makeQuery(id+"F2.opExtrude","SWEPT_BODY",BODY,{"disambiguationData":[OSD([sQuery(id+"F0.wireOp",EDGE,"E8.0.3.0")])]});
            var Q32;
            Q32=makeQuery(id+"F2.opExtrude","SWEPT_BODY",BODY,{"disambiguationData":[OSD([sQuery(id+"F0.wireOp",EDGE,"E8.0.4.0")])]});
            var Q33;
            Q33=makeQuery(id+"F2.opExtrude","SWEPT_BODY",BODY,{"disambiguationData":[OSD([sQuery(id+"F0.wireOp",EDGE,"E8.0.5.0")])]});
            var Q34;
            Q34=makeQuery(id+"F2.opExtrude","SWEPT_BODY",BODY,{"disambiguationData":[OSD([sQuery(id+"F0.wireOp",EDGE,"E8.0.6.0")])]});
            var Q35;
            Q35=makeQuery(id+"F2.opExtrude","SWEPT_BODY",BODY,{"disambiguationData":[OSD([sQuery(id+"F0.wireOp",EDGE,"E8.0.7.0")])]});
            var Q36;
            Q36=makeQuery(id+"F2.opExtrude","SWEPT_BODY",BODY,{"disambiguationData":[OSD([sQuery(id+"F0.wireOp",EDGE,"E8.0.8.0")])]});
            var Q37;
            Q37=makeQuery(id+"F2.opExtrude","SWEPT_BODY",BODY,{"disambiguationData":[OSD([sQuery(id+"F0.wireOp",EDGE,"E8.0.9.0")])]});
            var Q38;
            Q38=makeQuery(id+"F2.opExtrude","SWEPT_BODY",BODY,{"disambiguationData":[OSD([sQuery(id+"F0.wireOp",EDGE,"E8.0.10.0")])]});
            var Q39;
            Q39=makeQuery(id+"F2.opExtrude","SWEPT_BODY",BODY,{"disambiguationData":[OSD([sQuery(id+"F0.wireOp",EDGE,"E8.0.11.0")])]});
            var Q40;
            Q40=makeQuery(id+"F2.opExtrude","SWEPT_BODY",BODY,{"disambiguationData":[OSD([sQuery(id+"F0.wireOp",EDGE,"E8.0.12.0")])]});
            var Q41;
            Q41=makeQuery(id+"F2.opExtrude","SWEPT_BODY",BODY,{"disambiguationData":[OSD([sQuery(id+"F0.wireOp",EDGE,"E8.0.13.0")])]});
            var Q42;
            Q42=makeQuery(id+"F2.opExtrude","SWEPT_BODY",BODY,{"disambiguationData":[OSD([sQuery(id+"F0.wireOp",EDGE,"E8.0.14.0")])]});
            var Q43;
            Q43=makeQuery(id+"F2.opExtrude","SWEPT_BODY",BODY,{"disambiguationData":[OSD([sQuery(id+"F0.wireOp",EDGE,"E9.1.0.0")])]});
            var Q44;
            Q44=makeQuery(id+"F2.opExtrude","SWEPT_BODY",BODY,{"disambiguationData":[OSD([sQuery(id+"F0.wireOp",EDGE,"E9.1.0.1")])]});
            var Q45;
            Q45=makeQuery(id+"F2.opExtrude","SWEPT_BODY",BODY,{"disambiguationData":[OSD([sQuery(id+"F0.wireOp",EDGE,"E9.1.0.2")])]});
            var Q46;
            Q46=makeQuery(id+"F2.opExtrude","SWEPT_BODY",BODY,{"disambiguationData":[OSD([sQuery(id+"F0.wireOp",EDGE,"E9.1.0.3")])]});
            var Q47;
            Q47=makeQuery(id+"F2.opExtrude","SWEPT_BODY",BODY,{"disambiguationData":[OSD([sQuery(id+"F0.wireOp",EDGE,"E9.1.0.4")])]});
            var Q48;
            Q48=makeQuery(id+"F2.opExtrude","SWEPT_BODY",BODY,{"disambiguationData":[OSD([sQuery(id+"F0.wireOp",EDGE,"E9.1.0.5")])]});
            var Q49;
            Q49=makeQuery(id+"F2.opExtrude","SWEPT_BODY",BODY,{"disambiguationData":[OSD([sQuery(id+"F0.wireOp",EDGE,"E9.1.0.6")])]});
            var Q50;
            Q50=makeQuery(id+"F2.opExtrude","SWEPT_BODY",BODY,{"disambiguationData":[OSD([sQuery(id+"F0.wireOp",EDGE,"E9.1.0.7")])]});
            var Q51;
            Q51=makeQuery(id+"F2.opExtrude","SWEPT_BODY",BODY,{"disambiguationData":[OSD([sQuery(id+"F0.wireOp",EDGE,"E9.1.0.8")])]});
            var Q52;
            Q52=makeQuery(id+"F2.opExtrude","SWEPT_BODY",BODY,{"disambiguationData":[OSD([sQuery(id+"F0.wireOp",EDGE,"E9.1.0.9")])]});
            var Q53;
            Q53=makeQuery(id+"F2.opExtrude","SWEPT_BODY",BODY,{"disambiguationData":[OSD([sQuery(id+"F0.wireOp",EDGE,"E9.1.0.10")])]});
            var Q54;
            Q54=makeQuery(id+"F2.opExtrude","SWEPT_BODY",BODY,{"disambiguationData":[OSD([sQuery(id+"F0.wireOp",EDGE,"E9.1.0.11")])]});
            var Q55;
            Q55=makeQuery(id+"F2.opExtrude","SWEPT_BODY",BODY,{"disambiguationData":[OSD([sQuery(id+"F0.wireOp",EDGE,"E9.1.0.12")])]});
            var Q56;
            Q56=makeQuery(id+"F2.opExtrude","SWEPT_BODY",BODY,{"disambiguationData":[OSD([sQuery(id+"F0.wireOp",EDGE,"E9.1.0.13")])]});
            var Q57;
            Q57=makeQuery(id+"F2.opExtrude","SWEPT_BODY",BODY,{"disambiguationData":[OSD([sQuery(id+"F0.wireOp",EDGE,"E9.1.0.14")])]});
            var Q58;
            Q58=makeQuery(id+"F2.opExtrude","SWEPT_BODY",BODY,{"disambiguationData":[OSD([sQuery(id+"F0.wireOp",EDGE,"E9.1.0.15")])]});
            var Q59;
            Q59=makeQuery(id+"F2.opExtrude","SWEPT_BODY",BODY,{"disambiguationData":[OSD([sQuery(id+"F0.wireOp",EDGE,"E9.1.0.16")])]});
            var Q60;
            Q60=makeQuery(id+"F2.opExtrude","SWEPT_BODY",BODY,{"disambiguationData":[OSD([sQuery(id+"F0.wireOp",EDGE,"E9.1.0.17")])]});
            var Q61;
            Q61=makeQuery(id+"F2.opExtrude","SWEPT_BODY",BODY,{"disambiguationData":[OSD([sQuery(id+"F0.wireOp",EDGE,"E9.1.0.18")])]});
            var Q62;
            Q62=makeQuery(id+"F2.opExtrude","SWEPT_BODY",BODY,{"disambiguationData":[OSD([sQuery(id+"F0.wireOp",EDGE,"E9.1.0.19")])]});
            var Q63;
            Q63=makeQuery(id+"F2.opExtrude","SWEPT_BODY",BODY,{"disambiguationData":[OSD([sQuery(id+"F0.wireOp",EDGE,"E9.1.0.20")])]});
            var Q64;
            Q64=makeQuery(id+"F2.opExtrude","SWEPT_BODY",BODY,{"disambiguationData":[OSD([sQuery(id+"F0.wireOp",EDGE,"E9.1.0.21")])]});
            var Q65;
            Q65=makeQuery(id+"F2.opExtrude","SWEPT_BODY",BODY,{"disambiguationData":[OSD([sQuery(id+"F0.wireOp",EDGE,"E9.1.0.22")])]});
            var Q66;
            Q66=makeQuery(id+"F2.opExtrude","SWEPT_BODY",BODY,{"disambiguationData":[OSD([sQuery(id+"F0.wireOp",EDGE,"E9.1.0.23")])]});
            var Q67;
            Q67=makeQuery(id+"F2.opExtrude","SWEPT_BODY",BODY,{"disambiguationData":[OSD([sQuery(id+"F0.wireOp",EDGE,"E9.2.0.0")])]});
            var Q68;
            Q68=makeQuery(id+"F2.opExtrude","SWEPT_BODY",BODY,{"disambiguationData":[OSD([sQuery(id+"F0.wireOp",EDGE,"E9.2.0.1")])]});
            var Q69;
            Q69=makeQuery(id+"F2.opExtrude","SWEPT_BODY",BODY,{"disambiguationData":[OSD([sQuery(id+"F0.wireOp",EDGE,"E9.2.0.2")])]});
            var Q70;
            Q70=makeQuery(id+"F2.opExtrude","SWEPT_BODY",BODY,{"disambiguationData":[OSD([sQuery(id+"F0.wireOp",EDGE,"E9.2.0.3")])]});
            var Q71;
            Q71=makeQuery(id+"F2.opExtrude","SWEPT_BODY",BODY,{"disambiguationData":[OSD([sQuery(id+"F0.wireOp",EDGE,"E9.2.0.4")])]});
            var Q72;
            Q72=makeQuery(id+"F2.opExtrude","SWEPT_BODY",BODY,{"disambiguationData":[OSD([sQuery(id+"F0.wireOp",EDGE,"E9.2.0.5")])]});
            var Q73;
            Q73=makeQuery(id+"F2.opExtrude","SWEPT_BODY",BODY,{"disambiguationData":[OSD([sQuery(id+"F0.wireOp",EDGE,"E9.2.0.6")])]});
            var Q74;
            Q74=makeQuery(id+"F2.opExtrude","SWEPT_BODY",BODY,{"disambiguationData":[OSD([sQuery(id+"F0.wireOp",EDGE,"E9.2.0.7")])]});
            var Q75;
            Q75=makeQuery(id+"F2.opExtrude","SWEPT_BODY",BODY,{"disambiguationData":[OSD([sQuery(id+"F0.wireOp",EDGE,"E9.2.0.8")])]});
            var Q76;
            Q76=makeQuery(id+"F2.opExtrude","SWEPT_BODY",BODY,{"disambiguationData":[OSD([sQuery(id+"F0.wireOp",EDGE,"E9.2.0.9")])]});
            var Q77;
            Q77=makeQuery(id+"F2.opExtrude","SWEPT_BODY",BODY,{"disambiguationData":[OSD([sQuery(id+"F0.wireOp",EDGE,"E9.2.0.10")])]});
            var Q78;
            Q78=makeQuery(id+"F2.opExtrude","SWEPT_BODY",BODY,{"disambiguationData":[OSD([sQuery(id+"F0.wireOp",EDGE,"E9.2.0.11")])]});
            var Q79;
            Q79=makeQuery(id+"F2.opExtrude","SWEPT_BODY",BODY,{"disambiguationData":[OSD([sQuery(id+"F0.wireOp",EDGE,"E9.2.0.12")])]});
            var Q80;
            Q80=makeQuery(id+"F2.opExtrude","SWEPT_BODY",BODY,{"disambiguationData":[OSD([sQuery(id+"F0.wireOp",EDGE,"E9.2.0.13")])]});
            var Q81;
            Q81=makeQuery(id+"F2.opExtrude","SWEPT_BODY",BODY,{"disambiguationData":[OSD([sQuery(id+"F0.wireOp",EDGE,"E9.2.0.14")])]});
            var Q82;
            Q82=makeQuery(id+"F2.opExtrude","SWEPT_BODY",BODY,{"disambiguationData":[OSD([sQuery(id+"F0.wireOp",EDGE,"E9.2.0.15")])]});
            var Q83;
            Q83=makeQuery(id+"F2.opExtrude","SWEPT_BODY",BODY,{"disambiguationData":[OSD([sQuery(id+"F0.wireOp",EDGE,"E9.2.0.16")])]});
            var Q84;
            Q84=makeQuery(id+"F2.opExtrude","SWEPT_BODY",BODY,{"disambiguationData":[OSD([sQuery(id+"F0.wireOp",EDGE,"E9.2.0.17")])]});
            var Q85;
            Q85=makeQuery(id+"F2.opExtrude","SWEPT_BODY",BODY,{"disambiguationData":[OSD([sQuery(id+"F0.wireOp",EDGE,"E9.2.0.18")])]});
            var Q86;
            Q86=makeQuery(id+"F2.opExtrude","SWEPT_BODY",BODY,{"disambiguationData":[OSD([sQuery(id+"F0.wireOp",EDGE,"E9.2.0.19")])]});
            var Q87;
            Q87=makeQuery(id+"F2.opExtrude","SWEPT_BODY",BODY,{"disambiguationData":[OSD([sQuery(id+"F0.wireOp",EDGE,"E9.2.0.20")])]});
            var Q88;
            Q88=makeQuery(id+"F2.opExtrude","SWEPT_BODY",BODY,{"disambiguationData":[OSD([sQuery(id+"F0.wireOp",EDGE,"E9.2.0.21")])]});
            var Q89;
            Q89=makeQuery(id+"F2.opExtrude","SWEPT_BODY",BODY,{"disambiguationData":[OSD([sQuery(id+"F0.wireOp",EDGE,"E9.2.0.22")])]});
            var Q90;
            Q90=makeQuery(id+"F2.opExtrude","SWEPT_BODY",BODY,{"disambiguationData":[OSD([sQuery(id+"F0.wireOp",EDGE,"E9.2.0.23")])]});
            var Q91;
            Q91=makeQuery(id+"F2.opExtrude","SWEPT_BODY",BODY,{"disambiguationData":[OSD([sQuery(id+"F0.wireOp",EDGE,"E9.3.0.0")])]});
            var Q92;
            Q92=makeQuery(id+"F2.opExtrude","SWEPT_BODY",BODY,{"disambiguationData":[OSD([sQuery(id+"F0.wireOp",EDGE,"E9.3.0.1")])]});
            var Q93;
            Q93=makeQuery(id+"F2.opExtrude","SWEPT_BODY",BODY,{"disambiguationData":[OSD([sQuery(id+"F0.wireOp",EDGE,"E9.3.0.2")])]});
            var Q94;
            Q94=makeQuery(id+"F2.opExtrude","SWEPT_BODY",BODY,{"disambiguationData":[OSD([sQuery(id+"F0.wireOp",EDGE,"E9.3.0.3")])]});
            var Q95;
            Q95=makeQuery(id+"F2.opExtrude","SWEPT_BODY",BODY,{"disambiguationData":[OSD([sQuery(id+"F0.wireOp",EDGE,"E9.3.0.4")])]});
            var Q96;
            Q96=makeQuery(id+"F2.opExtrude","SWEPT_BODY",BODY,{"disambiguationData":[OSD([sQuery(id+"F0.wireOp",EDGE,"E9.3.0.5")])]});
            var Q97;
            Q97=makeQuery(id+"F2.opExtrude","SWEPT_BODY",BODY,{"disambiguationData":[OSD([sQuery(id+"F0.wireOp",EDGE,"E9.3.0.6")])]});
            var Q98;
            Q98=makeQuery(id+"F2.opExtrude","SWEPT_BODY",BODY,{"disambiguationData":[OSD([sQuery(id+"F0.wireOp",EDGE,"E9.3.0.7")])]});
            var Q99;
            Q99=makeQuery(id+"F2.opExtrude","SWEPT_BODY",BODY,{"disambiguationData":[OSD([sQuery(id+"F0.wireOp",EDGE,"E9.3.0.8")])]});
            var Q100;
            Q100=makeQuery(id+"F2.opExtrude","SWEPT_BODY",BODY,{"disambiguationData":[OSD([sQuery(id+"F0.wireOp",EDGE,"E9.3.0.9")])]});
            var Q101;
            Q101=makeQuery(id+"F2.opExtrude","SWEPT_BODY",BODY,{"disambiguationData":[OSD([sQuery(id+"F0.wireOp",EDGE,"E9.3.0.10")])]});
            var Q102;
            Q102=makeQuery(id+"F2.opExtrude","SWEPT_BODY",BODY,{"disambiguationData":[OSD([sQuery(id+"F0.wireOp",EDGE,"E9.3.0.11")])]});
            var Q103;
            Q103=makeQuery(id+"F2.opExtrude","SWEPT_BODY",BODY,{"disambiguationData":[OSD([sQuery(id+"F0.wireOp",EDGE,"E9.3.0.12")])]});
            var Q104;
            Q104=makeQuery(id+"F2.opExtrude","SWEPT_BODY",BODY,{"disambiguationData":[OSD([sQuery(id+"F0.wireOp",EDGE,"E9.3.0.13")])]});
            var Q105;
            Q105=makeQuery(id+"F2.opExtrude","SWEPT_BODY",BODY,{"disambiguationData":[OSD([sQuery(id+"F0.wireOp",EDGE,"E9.3.0.14")])]});
            var Q106;
            Q106=makeQuery(id+"F2.opExtrude","SWEPT_BODY",BODY,{"disambiguationData":[OSD([sQuery(id+"F0.wireOp",EDGE,"E9.3.0.15")])]});
            var Q107;
            Q107=makeQuery(id+"F2.opExtrude","SWEPT_BODY",BODY,{"disambiguationData":[OSD([sQuery(id+"F0.wireOp",EDGE,"E9.3.0.16")])]});
            var Q108;
            Q108=makeQuery(id+"F2.opExtrude","SWEPT_BODY",BODY,{"disambiguationData":[OSD([sQuery(id+"F0.wireOp",EDGE,"E9.3.0.17")])]});
            var Q109;
            Q109=makeQuery(id+"F2.opExtrude","SWEPT_BODY",BODY,{"disambiguationData":[OSD([sQuery(id+"F0.wireOp",EDGE,"E9.3.0.18")])]});
            var Q110;
            Q110=makeQuery(id+"F2.opExtrude","SWEPT_BODY",BODY,{"disambiguationData":[OSD([sQuery(id+"F0.wireOp",EDGE,"E9.3.0.19")])]});
            var Q111;
            Q111=makeQuery(id+"F2.opExtrude","SWEPT_BODY",BODY,{"disambiguationData":[OSD([sQuery(id+"F0.wireOp",EDGE,"E9.3.0.20")])]});
            var Q112;
            Q112=makeQuery(id+"F2.opExtrude","SWEPT_BODY",BODY,{"disambiguationData":[OSD([sQuery(id+"F0.wireOp",EDGE,"E9.3.0.21")])]});
            var Q113;
            Q113=makeQuery(id+"F2.opExtrude","SWEPT_BODY",BODY,{"disambiguationData":[OSD([sQuery(id+"F0.wireOp",EDGE,"E9.3.0.22")])]});
            var Q114;
            Q114=makeQuery(id+"F2.opExtrude","SWEPT_BODY",BODY,{"disambiguationData":[OSD([sQuery(id+"F0.wireOp",EDGE,"E9.3.0.23")])]});
            var Q115;
            Q115=makeQuery(id+"F2.opExtrude","SWEPT_BODY",BODY,{"disambiguationData":[OSD([sQuery(id+"F0.wireOp",EDGE,"E9.4.0.0")])]});
            var Q116;
            Q116=makeQuery(id+"F2.opExtrude","SWEPT_BODY",BODY,{"disambiguationData":[OSD([sQuery(id+"F0.wireOp",EDGE,"E9.4.0.1")])]});
            var Q117;
            Q117=makeQuery(id+"F2.opExtrude","SWEPT_BODY",BODY,{"disambiguationData":[OSD([sQuery(id+"F0.wireOp",EDGE,"E9.4.0.2")])]});
            var Q118;
            Q118=makeQuery(id+"F2.opExtrude","SWEPT_BODY",BODY,{"disambiguationData":[OSD([sQuery(id+"F0.wireOp",EDGE,"E9.4.0.3")])]});
            var Q119;
            Q119=makeQuery(id+"F2.opExtrude","SWEPT_BODY",BODY,{"disambiguationData":[OSD([sQuery(id+"F0.wireOp",EDGE,"E9.4.0.4")])]});
            var Q120;
            Q120=makeQuery(id+"F2.opExtrude","SWEPT_BODY",BODY,{"disambiguationData":[OSD([sQuery(id+"F0.wireOp",EDGE,"E9.4.0.5")])]});
            var Q121;
            Q121=makeQuery(id+"F2.opExtrude","SWEPT_BODY",BODY,{"disambiguationData":[OSD([sQuery(id+"F0.wireOp",EDGE,"E9.4.0.6")])]});
            var Q122;
            Q122=makeQuery(id+"F2.opExtrude","SWEPT_BODY",BODY,{"disambiguationData":[OSD([sQuery(id+"F0.wireOp",EDGE,"E9.4.0.7")])]});
            var Q123;
            Q123=makeQuery(id+"F2.opExtrude","SWEPT_BODY",BODY,{"disambiguationData":[OSD([sQuery(id+"F0.wireOp",EDGE,"E9.4.0.8")])]});
            var Q124;
            Q124=makeQuery(id+"F2.opExtrude","SWEPT_BODY",BODY,{"disambiguationData":[OSD([sQuery(id+"F0.wireOp",EDGE,"E9.4.0.9")])]});
            var Q125;
            Q125=makeQuery(id+"F2.opExtrude","SWEPT_BODY",BODY,{"disambiguationData":[OSD([sQuery(id+"F0.wireOp",EDGE,"E9.4.0.10")])]});
            var Q126;
            Q126=makeQuery(id+"F2.opExtrude","SWEPT_BODY",BODY,{"disambiguationData":[OSD([sQuery(id+"F0.wireOp",EDGE,"E9.4.0.11")])]});
            var Q127;
            Q127=makeQuery(id+"F2.opExtrude","SWEPT_BODY",BODY,{"disambiguationData":[OSD([sQuery(id+"F0.wireOp",EDGE,"E9.4.0.12")])]});
            var Q128;
            Q128=makeQuery(id+"F2.opExtrude","SWEPT_BODY",BODY,{"disambiguationData":[OSD([sQuery(id+"F0.wireOp",EDGE,"E9.4.0.13")])]});
            var Q129;
            Q129=makeQuery(id+"F2.opExtrude","SWEPT_BODY",BODY,{"disambiguationData":[OSD([sQuery(id+"F0.wireOp",EDGE,"E9.4.0.14")])]});
            var Q130;
            Q130=makeQuery(id+"F2.opExtrude","SWEPT_BODY",BODY,{"disambiguationData":[OSD([sQuery(id+"F0.wireOp",EDGE,"E9.4.0.15")])]});
            var Q131;
            Q131=makeQuery(id+"F2.opExtrude","SWEPT_BODY",BODY,{"disambiguationData":[OSD([sQuery(id+"F0.wireOp",EDGE,"E9.4.0.16")])]});
            var Q132;
            Q132=makeQuery(id+"F2.opExtrude","SWEPT_BODY",BODY,{"disambiguationData":[OSD([sQuery(id+"F0.wireOp",EDGE,"E9.4.0.17")])]});
            var Q133;
            Q133=makeQuery(id+"F2.opExtrude","SWEPT_BODY",BODY,{"disambiguationData":[OSD([sQuery(id+"F0.wireOp",EDGE,"E9.4.0.18")])]});
            var Q134;
            Q134=makeQuery(id+"F2.opExtrude","SWEPT_BODY",BODY,{"disambiguationData":[OSD([sQuery(id+"F0.wireOp",EDGE,"E9.4.0.19")])]});
            var Q135;
            Q135=makeQuery(id+"F2.opExtrude","SWEPT_BODY",BODY,{"disambiguationData":[OSD([sQuery(id+"F0.wireOp",EDGE,"E9.4.0.20")])]});
            var Q136;
            Q136=makeQuery(id+"F2.opExtrude","SWEPT_BODY",BODY,{"disambiguationData":[OSD([sQuery(id+"F0.wireOp",EDGE,"E9.4.0.21")])]});
            var Q137;
            Q137=makeQuery(id+"F2.opExtrude","SWEPT_BODY",BODY,{"disambiguationData":[OSD([sQuery(id+"F0.wireOp",EDGE,"E9.4.0.22")])]});
            var Q138;
            Q138=makeQuery(id+"F2.opExtrude","SWEPT_BODY",BODY,{"disambiguationData":[OSD([sQuery(id+"F0.wireOp",EDGE,"E9.4.0.23")])]});
            var Q139;
            Q139=makeQuery(id+"F2.opExtrude","SWEPT_BODY",BODY,{"disambiguationData":[OSD([sQuery(id+"F0.wireOp",EDGE,"E9.5.0.0")])]});
            var Q140;
            Q140=makeQuery(id+"F2.opExtrude","SWEPT_BODY",BODY,{"disambiguationData":[OSD([sQuery(id+"F0.wireOp",EDGE,"E9.5.0.1")])]});
            var Q141;
            Q141=makeQuery(id+"F2.opExtrude","SWEPT_BODY",BODY,{"disambiguationData":[OSD([sQuery(id+"F0.wireOp",EDGE,"E9.5.0.2")])]});
            var Q142;
            Q142=makeQuery(id+"F2.opExtrude","SWEPT_BODY",BODY,{"disambiguationData":[OSD([sQuery(id+"F0.wireOp",EDGE,"E9.5.0.3")])]});
            var Q143;
            Q143=makeQuery(id+"F2.opExtrude","SWEPT_BODY",BODY,{"disambiguationData":[OSD([sQuery(id+"F0.wireOp",EDGE,"E9.5.0.4")])]});
            var Q144;
            Q144=makeQuery(id+"F2.opExtrude","SWEPT_BODY",BODY,{"disambiguationData":[OSD([sQuery(id+"F0.wireOp",EDGE,"E9.5.0.5")])]});
            var Q145;
            Q145=makeQuery(id+"F2.opExtrude","SWEPT_BODY",BODY,{"disambiguationData":[OSD([sQuery(id+"F0.wireOp",EDGE,"E9.5.0.6")])]});
            var Q146;
            Q146=makeQuery(id+"F2.opExtrude","SWEPT_BODY",BODY,{"disambiguationData":[OSD([sQuery(id+"F0.wireOp",EDGE,"E9.5.0.7")])]});
            var Q147;
            Q147=makeQuery(id+"F2.opExtrude","SWEPT_BODY",BODY,{"disambiguationData":[OSD([sQuery(id+"F0.wireOp",EDGE,"E9.5.0.8")])]});
            var Q148;
            Q148=makeQuery(id+"F2.opExtrude","SWEPT_BODY",BODY,{"disambiguationData":[OSD([sQuery(id+"F0.wireOp",EDGE,"E9.5.0.9")])]});
            var Q149;
            Q149=makeQuery(id+"F2.opExtrude","SWEPT_BODY",BODY,{"disambiguationData":[OSD([sQuery(id+"F0.wireOp",EDGE,"E9.5.0.10")])]});
            var Q150;
            Q150=makeQuery(id+"F2.opExtrude","SWEPT_BODY",BODY,{"disambiguationData":[OSD([sQuery(id+"F0.wireOp",EDGE,"E9.5.0.11")])]});
            var Q151;
            Q151=makeQuery(id+"F2.opExtrude","SWEPT_BODY",BODY,{"disambiguationData":[OSD([sQuery(id+"F0.wireOp",EDGE,"E9.5.0.12")])]});
            var Q152;
            Q152=makeQuery(id+"F2.opExtrude","SWEPT_BODY",BODY,{"disambiguationData":[OSD([sQuery(id+"F0.wireOp",EDGE,"E9.5.0.13")])]});
            var Q153;
            Q153=makeQuery(id+"F2.opExtrude","SWEPT_BODY",BODY,{"disambiguationData":[OSD([sQuery(id+"F0.wireOp",EDGE,"E9.5.0.14")])]});
            var Q154;
            Q154=makeQuery(id+"F2.opExtrude","SWEPT_BODY",BODY,{"disambiguationData":[OSD([sQuery(id+"F0.wireOp",EDGE,"E9.5.0.15")])]});
            var Q155;
            Q155=makeQuery(id+"F2.opExtrude","SWEPT_BODY",BODY,{"disambiguationData":[OSD([sQuery(id+"F0.wireOp",EDGE,"E9.5.0.16")])]});
            var Q156;
            Q156=makeQuery(id+"F2.opExtrude","SWEPT_BODY",BODY,{"disambiguationData":[OSD([sQuery(id+"F0.wireOp",EDGE,"E9.5.0.17")])]});
            var Q157;
            Q157=makeQuery(id+"F2.opExtrude","SWEPT_BODY",BODY,{"disambiguationData":[OSD([sQuery(id+"F0.wireOp",EDGE,"E9.5.0.18")])]});
            var Q158;
            Q158=makeQuery(id+"F2.opExtrude","SWEPT_BODY",BODY,{"disambiguationData":[OSD([sQuery(id+"F0.wireOp",EDGE,"E9.5.0.19")])]});
            var Q159;
            Q159=makeQuery(id+"F2.opExtrude","SWEPT_BODY",BODY,{"disambiguationData":[OSD([sQuery(id+"F0.wireOp",EDGE,"E9.5.0.20")])]});
            var Q160;
            Q160=makeQuery(id+"F2.opExtrude","SWEPT_BODY",BODY,{"disambiguationData":[OSD([sQuery(id+"F0.wireOp",EDGE,"E9.5.0.21")])]});
            var Q161;
            Q161=makeQuery(id+"F2.opExtrude","SWEPT_BODY",BODY,{"disambiguationData":[OSD([sQuery(id+"F0.wireOp",EDGE,"E9.5.0.22")])]});
            var Q162;
            Q162=makeQuery(id+"F2.opExtrude","SWEPT_BODY",BODY,{"disambiguationData":[OSD([sQuery(id+"F0.wireOp",EDGE,"E9.5.0.23")])]});
            var Q163;
            Q163=makeQuery(id+"F2.opExtrude","SWEPT_BODY",BODY,{"disambiguationData":[OSD([sQuery(id+"F0.wireOp",EDGE,"E9.6.0.0")])]});
            var Q164;
            Q164=makeQuery(id+"F2.opExtrude","SWEPT_BODY",BODY,{"disambiguationData":[OSD([sQuery(id+"F0.wireOp",EDGE,"E9.6.0.1")])]});
            var Q165;
            Q165=makeQuery(id+"F2.opExtrude","SWEPT_BODY",BODY,{"disambiguationData":[OSD([sQuery(id+"F0.wireOp",EDGE,"E9.6.0.2")])]});
            var Q166;
            Q166=makeQuery(id+"F2.opExtrude","SWEPT_BODY",BODY,{"disambiguationData":[OSD([sQuery(id+"F0.wireOp",EDGE,"E9.6.0.3")])]});
            var Q167;
            Q167=makeQuery(id+"F2.opExtrude","SWEPT_BODY",BODY,{"disambiguationData":[OSD([sQuery(id+"F0.wireOp",EDGE,"E9.6.0.4")])]});
            var Q168;
            Q168=makeQuery(id+"F2.opExtrude","SWEPT_BODY",BODY,{"disambiguationData":[OSD([sQuery(id+"F0.wireOp",EDGE,"E9.6.0.5")])]});
            var Q169;
            Q169=makeQuery(id+"F2.opExtrude","SWEPT_BODY",BODY,{"disambiguationData":[OSD([sQuery(id+"F0.wireOp",EDGE,"E9.6.0.6")])]});
            var Q170;
            Q170=makeQuery(id+"F2.opExtrude","SWEPT_BODY",BODY,{"disambiguationData":[OSD([sQuery(id+"F0.wireOp",EDGE,"E9.6.0.7")])]});
            var Q171;
            Q171=makeQuery(id+"F2.opExtrude","SWEPT_BODY",BODY,{"disambiguationData":[OSD([sQuery(id+"F0.wireOp",EDGE,"E9.6.0.8")])]});
            var Q172;
            Q172=makeQuery(id+"F2.opExtrude","SWEPT_BODY",BODY,{"disambiguationData":[OSD([sQuery(id+"F0.wireOp",EDGE,"E9.6.0.9")])]});
            var Q173;
            Q173=makeQuery(id+"F2.opExtrude","SWEPT_BODY",BODY,{"disambiguationData":[OSD([sQuery(id+"F0.wireOp",EDGE,"E9.6.0.10")])]});
            var Q174;
            Q174=makeQuery(id+"F2.opExtrude","SWEPT_BODY",BODY,{"disambiguationData":[OSD([sQuery(id+"F0.wireOp",EDGE,"E9.6.0.11")])]});
            var Q175;
            Q175=makeQuery(id+"F2.opExtrude","SWEPT_BODY",BODY,{"disambiguationData":[OSD([sQuery(id+"F0.wireOp",EDGE,"E9.6.0.12")])]});
            var Q176;
            Q176=makeQuery(id+"F2.opExtrude","SWEPT_BODY",BODY,{"disambiguationData":[OSD([sQuery(id+"F0.wireOp",EDGE,"E9.6.0.13")])]});
            var Q177;
            Q177=makeQuery(id+"F2.opExtrude","SWEPT_BODY",BODY,{"disambiguationData":[OSD([sQuery(id+"F0.wireOp",EDGE,"E9.6.0.14")])]});
            var Q178;
            Q178=makeQuery(id+"F2.opExtrude","SWEPT_BODY",BODY,{"disambiguationData":[OSD([sQuery(id+"F0.wireOp",EDGE,"E9.6.0.15")])]});
            var Q179;
            Q179=makeQuery(id+"F2.opExtrude","SWEPT_BODY",BODY,{"disambiguationData":[OSD([sQuery(id+"F0.wireOp",EDGE,"E9.6.0.16")])]});
            var Q180;
            Q180=makeQuery(id+"F2.opExtrude","SWEPT_BODY",BODY,{"disambiguationData":[OSD([sQuery(id+"F0.wireOp",EDGE,"E9.6.0.17")])]});
            var Q181;
            Q181=makeQuery(id+"F2.opExtrude","SWEPT_BODY",BODY,{"disambiguationData":[OSD([sQuery(id+"F0.wireOp",EDGE,"E9.6.0.18")])]});
            var Q182;
            Q182=makeQuery(id+"F2.opExtrude","SWEPT_BODY",BODY,{"disambiguationData":[OSD([sQuery(id+"F0.wireOp",EDGE,"E9.6.0.19")])]});
            var Q183;
            Q183=makeQuery(id+"F2.opExtrude","SWEPT_BODY",BODY,{"disambiguationData":[OSD([sQuery(id+"F0.wireOp",EDGE,"E9.6.0.20")])]});
            var Q184;
            Q184=makeQuery(id+"F2.opExtrude","SWEPT_BODY",BODY,{"disambiguationData":[OSD([sQuery(id+"F0.wireOp",EDGE,"E9.6.0.21")])]});
            var Q185;
            Q185=makeQuery(id+"F2.opExtrude","SWEPT_BODY",BODY,{"disambiguationData":[OSD([sQuery(id+"F0.wireOp",EDGE,"E9.6.0.22")])]});
            var Q186;
            Q186=makeQuery(id+"F2.opExtrude","SWEPT_BODY",BODY,{"disambiguationData":[OSD([sQuery(id+"F0.wireOp",EDGE,"E9.6.0.23")])]});
            var Q187;
            Q187=makeQuery(id+"F2.opExtrude","SWEPT_BODY",BODY,{"disambiguationData":[OSD([sQuery(id+"F0.wireOp",EDGE,"E9.7.0.0")])]});
            var Q188;
            Q188=makeQuery(id+"F2.opExtrude","SWEPT_BODY",BODY,{"disambiguationData":[OSD([sQuery(id+"F0.wireOp",EDGE,"E9.7.0.1")])]});
            var Q189;
            Q189=makeQuery(id+"F2.opExtrude","SWEPT_BODY",BODY,{"disambiguationData":[OSD([sQuery(id+"F0.wireOp",EDGE,"E9.7.0.2")])]});
            var Q190;
            Q190=makeQuery(id+"F2.opExtrude","SWEPT_BODY",BODY,{"disambiguationData":[OSD([sQuery(id+"F0.wireOp",EDGE,"E9.7.0.3")])]});
            var Q191;
            Q191=makeQuery(id+"F2.opExtrude","SWEPT_BODY",BODY,{"disambiguationData":[OSD([sQuery(id+"F0.wireOp",EDGE,"E9.7.0.4")])]});
            var Q192;
            Q192=makeQuery(id+"F2.opExtrude","SWEPT_BODY",BODY,{"disambiguationData":[OSD([sQuery(id+"F0.wireOp",EDGE,"E9.7.0.5")])]});
            var Q193;
            Q193=makeQuery(id+"F2.opExtrude","SWEPT_BODY",BODY,{"disambiguationData":[OSD([sQuery(id+"F0.wireOp",EDGE,"E9.7.0.6")])]});
            var Q194;
            Q194=makeQuery(id+"F2.opExtrude","SWEPT_BODY",BODY,{"disambiguationData":[OSD([sQuery(id+"F0.wireOp",EDGE,"E9.7.0.7")])]});
            var Q195;
            Q195=makeQuery(id+"F2.opExtrude","SWEPT_BODY",BODY,{"disambiguationData":[OSD([sQuery(id+"F0.wireOp",EDGE,"E9.7.0.8")])]});
            var Q196;
            Q196=makeQuery(id+"F2.opExtrude","SWEPT_BODY",BODY,{"disambiguationData":[OSD([sQuery(id+"F0.wireOp",EDGE,"E9.7.0.9")])]});
            var Q197;
            Q197=makeQuery(id+"F2.opExtrude","SWEPT_BODY",BODY,{"disambiguationData":[OSD([sQuery(id+"F0.wireOp",EDGE,"E9.7.0.10")])]});
            var Q198;
            Q198=makeQuery(id+"F2.opExtrude","SWEPT_BODY",BODY,{"disambiguationData":[OSD([sQuery(id+"F0.wireOp",EDGE,"E9.7.0.11")])]});
            var Q199;
            Q199=makeQuery(id+"F2.opExtrude","SWEPT_BODY",BODY,{"disambiguationData":[OSD([sQuery(id+"F0.wireOp",EDGE,"E9.7.0.12")])]});
            var Q200;
            Q200=makeQuery(id+"F2.opExtrude","SWEPT_BODY",BODY,{"disambiguationData":[OSD([sQuery(id+"F0.wireOp",EDGE,"E9.7.0.13")])]});
            var Q201;
            Q201=makeQuery(id+"F2.opExtrude","SWEPT_BODY",BODY,{"disambiguationData":[OSD([sQuery(id+"F0.wireOp",EDGE,"E9.7.0.14")])]});
            var Q202;
            Q202=makeQuery(id+"F2.opExtrude","SWEPT_BODY",BODY,{"disambiguationData":[OSD([sQuery(id+"F0.wireOp",EDGE,"E9.7.0.15")])]});
            var Q203;
            Q203=makeQuery(id+"F2.opExtrude","SWEPT_BODY",BODY,{"disambiguationData":[OSD([sQuery(id+"F0.wireOp",EDGE,"E9.7.0.16")])]});
            var Q204;
            Q204=makeQuery(id+"F2.opExtrude","SWEPT_BODY",BODY,{"disambiguationData":[OSD([sQuery(id+"F0.wireOp",EDGE,"E9.7.0.17")])]});
            var Q205;
            Q205=makeQuery(id+"F2.opExtrude","SWEPT_BODY",BODY,{"disambiguationData":[OSD([sQuery(id+"F0.wireOp",EDGE,"E9.7.0.18")])]});
            var Q206;
            Q206=makeQuery(id+"F2.opExtrude","SWEPT_BODY",BODY,{"disambiguationData":[OSD([sQuery(id+"F0.wireOp",EDGE,"E9.7.0.19")])]});
            var Q207;
            Q207=makeQuery(id+"F2.opExtrude","SWEPT_BODY",BODY,{"disambiguationData":[OSD([sQuery(id+"F0.wireOp",EDGE,"E9.7.0.20")])]});
            var Q208;
            Q208=makeQuery(id+"F2.opExtrude","SWEPT_BODY",BODY,{"disambiguationData":[OSD([sQuery(id+"F0.wireOp",EDGE,"E9.7.0.21")])]});
            var Q209;
            Q209=makeQuery(id+"F2.opExtrude","SWEPT_BODY",BODY,{"disambiguationData":[OSD([sQuery(id+"F0.wireOp",EDGE,"E9.7.0.22")])]});
            var Q210;
            Q210=makeQuery(id+"F2.opExtrude","SWEPT_BODY",BODY,{"disambiguationData":[OSD([sQuery(id+"F0.wireOp",EDGE,"E9.7.0.23")])]});
            var Q211;
            Q211=makeQuery(id+"F2.opExtrude","SWEPT_BODY",BODY,{"disambiguationData":[OSD([sQuery(id+"F0.wireOp",EDGE,"E9.8.0.0")])]});
            var Q212;
            Q212=makeQuery(id+"F2.opExtrude","SWEPT_BODY",BODY,{"disambiguationData":[OSD([sQuery(id+"F0.wireOp",EDGE,"E9.8.0.1")])]});
            var Q213;
            Q213=makeQuery(id+"F2.opExtrude","SWEPT_BODY",BODY,{"disambiguationData":[OSD([sQuery(id+"F0.wireOp",EDGE,"E9.8.0.2")])]});
            var Q214;
            Q214=makeQuery(id+"F2.opExtrude","SWEPT_BODY",BODY,{"disambiguationData":[OSD([sQuery(id+"F0.wireOp",EDGE,"E9.8.0.3")])]});
            var Q215;
            Q215=makeQuery(id+"F2.opExtrude","SWEPT_BODY",BODY,{"disambiguationData":[OSD([sQuery(id+"F0.wireOp",EDGE,"E9.8.0.4")])]});
            var Q216;
            Q216=makeQuery(id+"F2.opExtrude","SWEPT_BODY",BODY,{"disambiguationData":[OSD([sQuery(id+"F0.wireOp",EDGE,"E9.8.0.5")])]});
            var Q217;
            Q217=makeQuery(id+"F2.opExtrude","SWEPT_BODY",BODY,{"disambiguationData":[OSD([sQuery(id+"F0.wireOp",EDGE,"E9.8.0.6")])]});
            var Q218;
            Q218=makeQuery(id+"F2.opExtrude","SWEPT_BODY",BODY,{"disambiguationData":[OSD([sQuery(id+"F0.wireOp",EDGE,"E9.8.0.7")])]});
            var Q219;
            Q219=makeQuery(id+"F2.opExtrude","SWEPT_BODY",BODY,{"disambiguationData":[OSD([sQuery(id+"F0.wireOp",EDGE,"E9.8.0.8")])]});
            var Q220;
            Q220=makeQuery(id+"F2.opExtrude","SWEPT_BODY",BODY,{"disambiguationData":[OSD([sQuery(id+"F0.wireOp",EDGE,"E9.8.0.9")])]});
            var Q221;
            Q221=makeQuery(id+"F2.opExtrude","SWEPT_BODY",BODY,{"disambiguationData":[OSD([sQuery(id+"F0.wireOp",EDGE,"E9.8.0.10")])]});
            var Q222;
            Q222=makeQuery(id+"F2.opExtrude","SWEPT_BODY",BODY,{"disambiguationData":[OSD([sQuery(id+"F0.wireOp",EDGE,"E9.8.0.11")])]});
            var Q223;
            Q223=makeQuery(id+"F2.opExtrude","SWEPT_BODY",BODY,{"disambiguationData":[OSD([sQuery(id+"F0.wireOp",EDGE,"E9.8.0.12")])]});
            var Q224;
            Q224=makeQuery(id+"F2.opExtrude","SWEPT_BODY",BODY,{"disambiguationData":[OSD([sQuery(id+"F0.wireOp",EDGE,"E9.8.0.13")])]});
            var Q225;
            Q225=makeQuery(id+"F2.opExtrude","SWEPT_BODY",BODY,{"disambiguationData":[OSD([sQuery(id+"F0.wireOp",EDGE,"E9.8.0.14")])]});
            var Q226;
            Q226=makeQuery(id+"F2.opExtrude","SWEPT_BODY",BODY,{"disambiguationData":[OSD([sQuery(id+"F0.wireOp",EDGE,"E9.8.0.15")])]});
            var Q227;
            Q227=makeQuery(id+"F2.opExtrude","SWEPT_BODY",BODY,{"disambiguationData":[OSD([sQuery(id+"F0.wireOp",EDGE,"E9.8.0.16")])]});
            var Q228;
            Q228=makeQuery(id+"F2.opExtrude","SWEPT_BODY",BODY,{"disambiguationData":[OSD([sQuery(id+"F0.wireOp",EDGE,"E9.8.0.17")])]});
            var Q229;
            Q229=makeQuery(id+"F2.opExtrude","SWEPT_BODY",BODY,{"disambiguationData":[OSD([sQuery(id+"F0.wireOp",EDGE,"E9.8.0.18")])]});
            var Q230;
            Q230=makeQuery(id+"F2.opExtrude","SWEPT_BODY",BODY,{"disambiguationData":[OSD([sQuery(id+"F0.wireOp",EDGE,"E9.8.0.19")])]});
            var Q231;
            Q231=makeQuery(id+"F2.opExtrude","SWEPT_BODY",BODY,{"disambiguationData":[OSD([sQuery(id+"F0.wireOp",EDGE,"E9.8.0.20")])]});
            var Q232;
            Q232=makeQuery(id+"F2.opExtrude","SWEPT_BODY",BODY,{"disambiguationData":[OSD([sQuery(id+"F0.wireOp",EDGE,"E9.8.0.21")])]});
            var Q233;
            Q233=makeQuery(id+"F2.opExtrude","SWEPT_BODY",BODY,{"disambiguationData":[OSD([sQuery(id+"F0.wireOp",EDGE,"E9.8.0.22")])]});
            var Q234;
            Q234=makeQuery(id+"F2.opExtrude","SWEPT_BODY",BODY,{"disambiguationData":[OSD([sQuery(id+"F0.wireOp",EDGE,"E9.8.0.23")])]});
            var Q235;
            Q235=makeQuery(id+"F2.opExtrude","SWEPT_BODY",BODY,{"disambiguationData":[OSD([sQuery(id+"F0.wireOp",EDGE,"E9.9.0.0")])]});
            var Q236;
            Q236=makeQuery(id+"F2.opExtrude","SWEPT_BODY",BODY,{"disambiguationData":[OSD([sQuery(id+"F0.wireOp",EDGE,"E9.9.0.1")])]});
            var Q237;
            Q237=makeQuery(id+"F2.opExtrude","SWEPT_BODY",BODY,{"disambiguationData":[OSD([sQuery(id+"F0.wireOp",EDGE,"E9.9.0.2")])]});
            var Q238;
            Q238=makeQuery(id+"F2.opExtrude","SWEPT_BODY",BODY,{"disambiguationData":[OSD([sQuery(id+"F0.wireOp",EDGE,"E9.9.0.3")])]});
            var Q239;
            Q239=makeQuery(id+"F2.opExtrude","SWEPT_BODY",BODY,{"disambiguationData":[OSD([sQuery(id+"F0.wireOp",EDGE,"E9.9.0.4")])]});
            var Q240;
            Q240=makeQuery(id+"F2.opExtrude","SWEPT_BODY",BODY,{"disambiguationData":[OSD([sQuery(id+"F0.wireOp",EDGE,"E9.9.0.5")])]});
            var Q241;
            Q241=makeQuery(id+"F2.opExtrude","SWEPT_BODY",BODY,{"disambiguationData":[OSD([sQuery(id+"F0.wireOp",EDGE,"E9.9.0.6")])]});
            var Q242;
            Q242=makeQuery(id+"F2.opExtrude","SWEPT_BODY",BODY,{"disambiguationData":[OSD([sQuery(id+"F0.wireOp",EDGE,"E9.9.0.7")])]});
            var Q243;
            Q243=makeQuery(id+"F2.opExtrude","SWEPT_BODY",BODY,{"disambiguationData":[OSD([sQuery(id+"F0.wireOp",EDGE,"E9.9.0.8")])]});
            var Q244;
            Q244=makeQuery(id+"F2.opExtrude","SWEPT_BODY",BODY,{"disambiguationData":[OSD([sQuery(id+"F0.wireOp",EDGE,"E9.9.0.9")])]});
            var Q245;
            Q245=makeQuery(id+"F2.opExtrude","SWEPT_BODY",BODY,{"disambiguationData":[OSD([sQuery(id+"F0.wireOp",EDGE,"E9.9.0.10")])]});
            var Q246;
            Q246=makeQuery(id+"F2.opExtrude","SWEPT_BODY",BODY,{"disambiguationData":[OSD([sQuery(id+"F0.wireOp",EDGE,"E9.9.0.11")])]});
            var Q247;
            Q247=makeQuery(id+"F2.opExtrude","SWEPT_BODY",BODY,{"disambiguationData":[OSD([sQuery(id+"F0.wireOp",EDGE,"E9.9.0.12")])]});
            var Q248;
            Q248=makeQuery(id+"F2.opExtrude","SWEPT_BODY",BODY,{"disambiguationData":[OSD([sQuery(id+"F0.wireOp",EDGE,"E9.9.0.13")])]});
            var Q249;
            Q249=makeQuery(id+"F2.opExtrude","SWEPT_BODY",BODY,{"disambiguationData":[OSD([sQuery(id+"F0.wireOp",EDGE,"E9.9.0.14")])]});
            var Q250;
            Q250=makeQuery(id+"F2.opExtrude","SWEPT_BODY",BODY,{"disambiguationData":[OSD([sQuery(id+"F0.wireOp",EDGE,"E9.9.0.15")])]});
            var Q251;
            Q251=makeQuery(id+"F2.opExtrude","SWEPT_BODY",BODY,{"disambiguationData":[OSD([sQuery(id+"F0.wireOp",EDGE,"E9.9.0.16")])]});
            var Q252;
            Q252=makeQuery(id+"F2.opExtrude","SWEPT_BODY",BODY,{"disambiguationData":[OSD([sQuery(id+"F0.wireOp",EDGE,"E9.9.0.17")])]});
            var Q253;
            Q253=makeQuery(id+"F2.opExtrude","SWEPT_BODY",BODY,{"disambiguationData":[OSD([sQuery(id+"F0.wireOp",EDGE,"E9.9.0.18")])]});
            var Q254;
            Q254=makeQuery(id+"F2.opExtrude","SWEPT_BODY",BODY,{"disambiguationData":[OSD([sQuery(id+"F0.wireOp",EDGE,"E9.9.0.19")])]});
            var Q255;
            Q255=makeQuery(id+"F2.opExtrude","SWEPT_BODY",BODY,{"disambiguationData":[OSD([sQuery(id+"F0.wireOp",EDGE,"E9.9.0.20")])]});
            var Q256;
            Q256=makeQuery(id+"F2.opExtrude","SWEPT_BODY",BODY,{"disambiguationData":[OSD([sQuery(id+"F0.wireOp",EDGE,"E9.9.0.21")])]});
            var Q257;
            Q257=makeQuery(id+"F2.opExtrude","SWEPT_BODY",BODY,{"disambiguationData":[OSD([sQuery(id+"F0.wireOp",EDGE,"E9.9.0.22")])]});
            var Q258;
            Q258=makeQuery(id+"F2.opExtrude","SWEPT_BODY",BODY,{"disambiguationData":[OSD([sQuery(id+"F0.wireOp",EDGE,"E9.9.0.23")])]});
            var Q259;
            Q259=makeQuery(id+"F2.opExtrude","SWEPT_BODY",BODY,{"disambiguationData":[OSD([sQuery(id+"F0.wireOp",EDGE,"E9.10.0.0")])]});
            var Q260;
            Q260=makeQuery(id+"F2.opExtrude","SWEPT_BODY",BODY,{"disambiguationData":[OSD([sQuery(id+"F0.wireOp",EDGE,"E9.10.0.1")])]});
            var Q261;
            Q261=makeQuery(id+"F2.opExtrude","SWEPT_BODY",BODY,{"disambiguationData":[OSD([sQuery(id+"F0.wireOp",EDGE,"E9.10.0.2")])]});
            var Q262;
            Q262=makeQuery(id+"F2.opExtrude","SWEPT_BODY",BODY,{"disambiguationData":[OSD([sQuery(id+"F0.wireOp",EDGE,"E9.10.0.3")])]});
            var Q263;
            Q263=makeQuery(id+"F2.opExtrude","SWEPT_BODY",BODY,{"disambiguationData":[OSD([sQuery(id+"F0.wireOp",EDGE,"E9.10.0.4")])]});
            var Q264;
            Q264=makeQuery(id+"F2.opExtrude","SWEPT_BODY",BODY,{"disambiguationData":[OSD([sQuery(id+"F0.wireOp",EDGE,"E9.10.0.5")])]});
            var Q265;
            Q265=makeQuery(id+"F2.opExtrude","SWEPT_BODY",BODY,{"disambiguationData":[OSD([sQuery(id+"F0.wireOp",EDGE,"E9.10.0.6")])]});
            var Q266;
            Q266=makeQuery(id+"F2.opExtrude","SWEPT_BODY",BODY,{"disambiguationData":[OSD([sQuery(id+"F0.wireOp",EDGE,"E9.10.0.7")])]});
            var Q267;
            Q267=makeQuery(id+"F2.opExtrude","SWEPT_BODY",BODY,{"disambiguationData":[OSD([sQuery(id+"F0.wireOp",EDGE,"E9.10.0.8")])]});
            var Q268;
            Q268=makeQuery(id+"F2.opExtrude","SWEPT_BODY",BODY,{"disambiguationData":[OSD([sQuery(id+"F0.wireOp",EDGE,"E9.10.0.9")])]});
            var Q269;
            Q269=makeQuery(id+"F2.opExtrude","SWEPT_BODY",BODY,{"disambiguationData":[OSD([sQuery(id+"F0.wireOp",EDGE,"E9.10.0.10")])]});
            var Q270;
            Q270=makeQuery(id+"F2.opExtrude","SWEPT_BODY",BODY,{"disambiguationData":[OSD([sQuery(id+"F0.wireOp",EDGE,"E9.10.0.11")])]});
            var Q271;
            Q271=makeQuery(id+"F2.opExtrude","SWEPT_BODY",BODY,{"disambiguationData":[OSD([sQuery(id+"F0.wireOp",EDGE,"E9.10.0.12")])]});
            var Q272;
            Q272=makeQuery(id+"F2.opExtrude","SWEPT_BODY",BODY,{"disambiguationData":[OSD([sQuery(id+"F0.wireOp",EDGE,"E9.10.0.13")])]});
            var Q273;
            Q273=makeQuery(id+"F2.opExtrude","SWEPT_BODY",BODY,{"disambiguationData":[OSD([sQuery(id+"F0.wireOp",EDGE,"E9.10.0.14")])]});
            var Q274;
            Q274=makeQuery(id+"F2.opExtrude","SWEPT_BODY",BODY,{"disambiguationData":[OSD([sQuery(id+"F0.wireOp",EDGE,"E9.10.0.15")])]});
            var Q275;
            Q275=makeQuery(id+"F2.opExtrude","SWEPT_BODY",BODY,{"disambiguationData":[OSD([sQuery(id+"F0.wireOp",EDGE,"E9.10.0.16")])]});
            var Q276;
            Q276=makeQuery(id+"F2.opExtrude","SWEPT_BODY",BODY,{"disambiguationData":[OSD([sQuery(id+"F0.wireOp",EDGE,"E9.10.0.17")])]});
            var Q277;
            Q277=makeQuery(id+"F2.opExtrude","SWEPT_BODY",BODY,{"disambiguationData":[OSD([sQuery(id+"F0.wireOp",EDGE,"E9.10.0.18")])]});
            var Q278;
            Q278=makeQuery(id+"F2.opExtrude","SWEPT_BODY",BODY,{"disambiguationData":[OSD([sQuery(id+"F0.wireOp",EDGE,"E9.10.0.19")])]});
            var Q279;
            Q279=makeQuery(id+"F2.opExtrude","SWEPT_BODY",BODY,{"disambiguationData":[OSD([sQuery(id+"F0.wireOp",EDGE,"E9.10.0.20")])]});
            var Q280;
            Q280=makeQuery(id+"F2.opExtrude","SWEPT_BODY",BODY,{"disambiguationData":[OSD([sQuery(id+"F0.wireOp",EDGE,"E9.10.0.21")])]});
            var Q281;
            Q281=makeQuery(id+"F2.opExtrude","SWEPT_BODY",BODY,{"disambiguationData":[OSD([sQuery(id+"F0.wireOp",EDGE,"E9.10.0.22")])]});
            var Q282;
            Q282=makeQuery(id+"F2.opExtrude","SWEPT_BODY",BODY,{"disambiguationData":[OSD([sQuery(id+"F0.wireOp",EDGE,"E9.10.0.23")])]});
            var Q283;
            Q283=makeQuery(id+"F2.opExtrude","SWEPT_BODY",BODY,{"disambiguationData":[OSD([sQuery(id+"F0.wireOp",EDGE,"E9.11.0.0")])]});
            var Q284;
            Q284=makeQuery(id+"F2.opExtrude","SWEPT_BODY",BODY,{"disambiguationData":[OSD([sQuery(id+"F0.wireOp",EDGE,"E9.11.0.1")])]});
            var Q285;
            Q285=makeQuery(id+"F2.opExtrude","SWEPT_BODY",BODY,{"disambiguationData":[OSD([sQuery(id+"F0.wireOp",EDGE,"E9.11.0.2")])]});
            var Q286;
            Q286=makeQuery(id+"F2.opExtrude","SWEPT_BODY",BODY,{"disambiguationData":[OSD([sQuery(id+"F0.wireOp",EDGE,"E9.11.0.3")])]});
            var Q287;
            Q287=makeQuery(id+"F2.opExtrude","SWEPT_BODY",BODY,{"disambiguationData":[OSD([sQuery(id+"F0.wireOp",EDGE,"E9.11.0.4")])]});
            var Q288;
            Q288=makeQuery(id+"F2.opExtrude","SWEPT_BODY",BODY,{"disambiguationData":[OSD([sQuery(id+"F0.wireOp",EDGE,"E9.11.0.5")])]});
            var Q289;
            Q289=makeQuery(id+"F2.opExtrude","SWEPT_BODY",BODY,{"disambiguationData":[OSD([sQuery(id+"F0.wireOp",EDGE,"E9.11.0.6")])]});
            var Q290;
            Q290=makeQuery(id+"F2.opExtrude","SWEPT_BODY",BODY,{"disambiguationData":[OSD([sQuery(id+"F0.wireOp",EDGE,"E9.11.0.7")])]});
            var Q291;
            Q291=makeQuery(id+"F2.opExtrude","SWEPT_BODY",BODY,{"disambiguationData":[OSD([sQuery(id+"F0.wireOp",EDGE,"E9.11.0.8")])]});
            var Q292;
            Q292=makeQuery(id+"F2.opExtrude","SWEPT_BODY",BODY,{"disambiguationData":[OSD([sQuery(id+"F0.wireOp",EDGE,"E9.11.0.9")])]});
            var Q293;
            Q293=makeQuery(id+"F2.opExtrude","SWEPT_BODY",BODY,{"disambiguationData":[OSD([sQuery(id+"F0.wireOp",EDGE,"E9.11.0.10")])]});
            var Q294;
            Q294=makeQuery(id+"F2.opExtrude","SWEPT_BODY",BODY,{"disambiguationData":[OSD([sQuery(id+"F0.wireOp",EDGE,"E9.11.0.11")])]});
            var Q295;
            Q295=makeQuery(id+"F2.opExtrude","SWEPT_BODY",BODY,{"disambiguationData":[OSD([sQuery(id+"F0.wireOp",EDGE,"E9.11.0.12")])]});
            var Q296;
            Q296=makeQuery(id+"F2.opExtrude","SWEPT_BODY",BODY,{"disambiguationData":[OSD([sQuery(id+"F0.wireOp",EDGE,"E9.11.0.13")])]});
            var Q297;
            Q297=makeQuery(id+"F2.opExtrude","SWEPT_BODY",BODY,{"disambiguationData":[OSD([sQuery(id+"F0.wireOp",EDGE,"E9.11.0.14")])]});
            var Q298;
            Q298=makeQuery(id+"F2.opExtrude","SWEPT_BODY",BODY,{"disambiguationData":[OSD([sQuery(id+"F0.wireOp",EDGE,"E9.11.0.15")])]});
            var Q299;
            Q299=makeQuery(id+"F2.opExtrude","SWEPT_BODY",BODY,{"disambiguationData":[OSD([sQuery(id+"F0.wireOp",EDGE,"E9.11.0.16")])]});
            var Q300;
            Q300=makeQuery(id+"F2.opExtrude","SWEPT_BODY",BODY,{"disambiguationData":[OSD([sQuery(id+"F0.wireOp",EDGE,"E9.11.0.17")])]});
            var Q301;
            Q301=makeQuery(id+"F2.opExtrude","SWEPT_BODY",BODY,{"disambiguationData":[OSD([sQuery(id+"F0.wireOp",EDGE,"E9.11.0.18")])]});
            var Q302;
            Q302=makeQuery(id+"F2.opExtrude","SWEPT_BODY",BODY,{"disambiguationData":[OSD([sQuery(id+"F0.wireOp",EDGE,"E9.11.0.19")])]});
            var Q303;
            Q303=makeQuery(id+"F2.opExtrude","SWEPT_BODY",BODY,{"disambiguationData":[OSD([sQuery(id+"F0.wireOp",EDGE,"E9.11.0.20")])]});
            var Q304;
            Q304=makeQuery(id+"F2.opExtrude","SWEPT_BODY",BODY,{"disambiguationData":[OSD([sQuery(id+"F0.wireOp",EDGE,"E9.11.0.21")])]});
            var Q305;
            Q305=makeQuery(id+"F2.opExtrude","SWEPT_BODY",BODY,{"disambiguationData":[OSD([sQuery(id+"F0.wireOp",EDGE,"E9.11.0.22")])]});
            var Q306;
            Q306=makeQuery(id+"F2.opExtrude","SWEPT_BODY",BODY,{"disambiguationData":[OSD([sQuery(id+"F0.wireOp",EDGE,"E9.11.0.23")])]});
            var Q307;
            Q307=makeQuery(id+"F2.opExtrude","SWEPT_BODY",BODY,{"disambiguationData":[OSD([sQuery(id+"F0.wireOp",EDGE,"E9.12.0.0")])]});
            var Q308;
            Q308=makeQuery(id+"F2.opExtrude","SWEPT_BODY",BODY,{"disambiguationData":[OSD([sQuery(id+"F0.wireOp",EDGE,"E9.12.0.1")])]});
            var Q309;
            Q309=makeQuery(id+"F2.opExtrude","SWEPT_BODY",BODY,{"disambiguationData":[OSD([sQuery(id+"F0.wireOp",EDGE,"E9.12.0.2")])]});
            var Q310;
            Q310=makeQuery(id+"F2.opExtrude","SWEPT_BODY",BODY,{"disambiguationData":[OSD([sQuery(id+"F0.wireOp",EDGE,"E9.12.0.3")])]});
            var Q311;
            Q311=makeQuery(id+"F2.opExtrude","SWEPT_BODY",BODY,{"disambiguationData":[OSD([sQuery(id+"F0.wireOp",EDGE,"E9.12.0.4")])]});
            var Q312;
            Q312=makeQuery(id+"F2.opExtrude","SWEPT_BODY",BODY,{"disambiguationData":[OSD([sQuery(id+"F0.wireOp",EDGE,"E9.12.0.5")])]});
            var Q313;
            Q313=makeQuery(id+"F2.opExtrude","SWEPT_BODY",BODY,{"disambiguationData":[OSD([sQuery(id+"F0.wireOp",EDGE,"E9.12.0.6")])]});
            var Q314;
            Q314=makeQuery(id+"F2.opExtrude","SWEPT_BODY",BODY,{"disambiguationData":[OSD([sQuery(id+"F0.wireOp",EDGE,"E9.12.0.7")])]});
            var Q315;
            Q315=makeQuery(id+"F2.opExtrude","SWEPT_BODY",BODY,{"disambiguationData":[OSD([sQuery(id+"F0.wireOp",EDGE,"E9.12.0.8")])]});
            var Q316;
            Q316=makeQuery(id+"F2.opExtrude","SWEPT_BODY",BODY,{"disambiguationData":[OSD([sQuery(id+"F0.wireOp",EDGE,"E9.12.0.9")])]});
            var Q317;
            Q317=makeQuery(id+"F2.opExtrude","SWEPT_BODY",BODY,{"disambiguationData":[OSD([sQuery(id+"F0.wireOp",EDGE,"E9.12.0.10")])]});
            var Q318;
            Q318=makeQuery(id+"F2.opExtrude","SWEPT_BODY",BODY,{"disambiguationData":[OSD([sQuery(id+"F0.wireOp",EDGE,"E9.12.0.11")])]});
            var Q319;
            Q319=makeQuery(id+"F2.opExtrude","SWEPT_BODY",BODY,{"disambiguationData":[OSD([sQuery(id+"F0.wireOp",EDGE,"E9.12.0.12")])]});
            var Q320;
            Q320=makeQuery(id+"F2.opExtrude","SWEPT_BODY",BODY,{"disambiguationData":[OSD([sQuery(id+"F0.wireOp",EDGE,"E9.12.0.13")])]});
            var Q321;
            Q321=makeQuery(id+"F2.opExtrude","SWEPT_BODY",BODY,{"disambiguationData":[OSD([sQuery(id+"F0.wireOp",EDGE,"E9.12.0.14")])]});
            var Q322;
            Q322=makeQuery(id+"F2.opExtrude","SWEPT_BODY",BODY,{"disambiguationData":[OSD([sQuery(id+"F0.wireOp",EDGE,"E9.12.0.15")])]});
            var Q323;
            Q323=makeQuery(id+"F2.opExtrude","SWEPT_BODY",BODY,{"disambiguationData":[OSD([sQuery(id+"F0.wireOp",EDGE,"E9.12.0.16")])]});
            var Q324;
            Q324=makeQuery(id+"F2.opExtrude","SWEPT_BODY",BODY,{"disambiguationData":[OSD([sQuery(id+"F0.wireOp",EDGE,"E9.12.0.17")])]});
            var Q325;
            Q325=makeQuery(id+"F2.opExtrude","SWEPT_BODY",BODY,{"disambiguationData":[OSD([sQuery(id+"F0.wireOp",EDGE,"E9.12.0.18")])]});
            var Q326;
            Q326=makeQuery(id+"F2.opExtrude","SWEPT_BODY",BODY,{"disambiguationData":[OSD([sQuery(id+"F0.wireOp",EDGE,"E9.12.0.19")])]});
            var Q327;
            Q327=makeQuery(id+"F2.opExtrude","SWEPT_BODY",BODY,{"disambiguationData":[OSD([sQuery(id+"F0.wireOp",EDGE,"E9.12.0.20")])]});
            var Q328;
            Q328=makeQuery(id+"F2.opExtrude","SWEPT_BODY",BODY,{"disambiguationData":[OSD([sQuery(id+"F0.wireOp",EDGE,"E9.12.0.21")])]});
            var Q329;
            Q329=makeQuery(id+"F2.opExtrude","SWEPT_BODY",BODY,{"disambiguationData":[OSD([sQuery(id+"F0.wireOp",EDGE,"E9.12.0.22")])]});
            var Q330;
            Q330=makeQuery(id+"F2.opExtrude","SWEPT_BODY",BODY,{"disambiguationData":[OSD([sQuery(id+"F0.wireOp",EDGE,"E9.12.0.23")])]});
            var Q331;
            Q331=makeQuery(id+"F2.opExtrude","SWEPT_BODY",BODY,{"disambiguationData":[OSD([sQuery(id+"F0.wireOp",EDGE,"E9.13.0.0")])]});
            var Q332;
            Q332=makeQuery(id+"F2.opExtrude","SWEPT_BODY",BODY,{"disambiguationData":[OSD([sQuery(id+"F0.wireOp",EDGE,"E9.13.0.1")])]});
            var Q333;
            Q333=makeQuery(id+"F2.opExtrude","SWEPT_BODY",BODY,{"disambiguationData":[OSD([sQuery(id+"F0.wireOp",EDGE,"E9.13.0.2")])]});
            var Q334;
            Q334=makeQuery(id+"F2.opExtrude","SWEPT_BODY",BODY,{"disambiguationData":[OSD([sQuery(id+"F0.wireOp",EDGE,"E9.13.0.3")])]});
            var Q335;
            Q335=makeQuery(id+"F2.opExtrude","SWEPT_BODY",BODY,{"disambiguationData":[OSD([sQuery(id+"F0.wireOp",EDGE,"E9.13.0.4")])]});
            var Q336;
            Q336=makeQuery(id+"F2.opExtrude","SWEPT_BODY",BODY,{"disambiguationData":[OSD([sQuery(id+"F0.wireOp",EDGE,"E9.13.0.5")])]});
            var Q337;
            Q337=makeQuery(id+"F2.opExtrude","SWEPT_BODY",BODY,{"disambiguationData":[OSD([sQuery(id+"F0.wireOp",EDGE,"E9.13.0.6")])]});
            var Q338;
            Q338=makeQuery(id+"F2.opExtrude","SWEPT_BODY",BODY,{"disambiguationData":[OSD([sQuery(id+"F0.wireOp",EDGE,"E9.13.0.7")])]});
            var Q339;
            Q339=makeQuery(id+"F2.opExtrude","SWEPT_BODY",BODY,{"disambiguationData":[OSD([sQuery(id+"F0.wireOp",EDGE,"E9.13.0.8")])]});
            var Q340;
            Q340=makeQuery(id+"F2.opExtrude","SWEPT_BODY",BODY,{"disambiguationData":[OSD([sQuery(id+"F0.wireOp",EDGE,"E9.13.0.9")])]});
            var Q341;
            Q341=makeQuery(id+"F2.opExtrude","SWEPT_BODY",BODY,{"disambiguationData":[OSD([sQuery(id+"F0.wireOp",EDGE,"E9.13.0.10")])]});
            var Q342;
            Q342=makeQuery(id+"F2.opExtrude","SWEPT_BODY",BODY,{"disambiguationData":[OSD([sQuery(id+"F0.wireOp",EDGE,"E9.13.0.11")])]});
            var Q343;
            Q343=makeQuery(id+"F2.opExtrude","SWEPT_BODY",BODY,{"disambiguationData":[OSD([sQuery(id+"F0.wireOp",EDGE,"E9.13.0.12")])]});
            var Q344;
            Q344=makeQuery(id+"F2.opExtrude","SWEPT_BODY",BODY,{"disambiguationData":[OSD([sQuery(id+"F0.wireOp",EDGE,"E9.13.0.13")])]});
            var Q345;
            Q345=makeQuery(id+"F2.opExtrude","SWEPT_BODY",BODY,{"disambiguationData":[OSD([sQuery(id+"F0.wireOp",EDGE,"E9.13.0.14")])]});
            var Q346;
            Q346=makeQuery(id+"F2.opExtrude","SWEPT_BODY",BODY,{"disambiguationData":[OSD([sQuery(id+"F0.wireOp",EDGE,"E9.13.0.15")])]});
            var Q347;
            Q347=makeQuery(id+"F2.opExtrude","SWEPT_BODY",BODY,{"disambiguationData":[OSD([sQuery(id+"F0.wireOp",EDGE,"E9.13.0.16")])]});
            var Q348;
            Q348=makeQuery(id+"F2.opExtrude","SWEPT_BODY",BODY,{"disambiguationData":[OSD([sQuery(id+"F0.wireOp",EDGE,"E9.13.0.17")])]});
            var Q349;
            Q349=makeQuery(id+"F2.opExtrude","SWEPT_BODY",BODY,{"disambiguationData":[OSD([sQuery(id+"F0.wireOp",EDGE,"E9.13.0.18")])]});
            var Q350;
            Q350=makeQuery(id+"F2.opExtrude","SWEPT_BODY",BODY,{"disambiguationData":[OSD([sQuery(id+"F0.wireOp",EDGE,"E9.13.0.19")])]});
            var Q351;
            Q351=makeQuery(id+"F2.opExtrude","SWEPT_BODY",BODY,{"disambiguationData":[OSD([sQuery(id+"F0.wireOp",EDGE,"E9.13.0.20")])]});
            var Q352;
            Q352=makeQuery(id+"F2.opExtrude","SWEPT_BODY",BODY,{"disambiguationData":[OSD([sQuery(id+"F0.wireOp",EDGE,"E9.13.0.21")])]});
            var Q353;
            Q353=makeQuery(id+"F2.opExtrude","SWEPT_BODY",BODY,{"disambiguationData":[OSD([sQuery(id+"F0.wireOp",EDGE,"E9.13.0.22")])]});
            var Q354;
            Q354=makeQuery(id+"F2.opExtrude","SWEPT_BODY",BODY,{"disambiguationData":[OSD([sQuery(id+"F0.wireOp",EDGE,"E9.13.0.23")])]});
            var Q355;
            Q355=makeQuery(id+"F2.opExtrude","SWEPT_BODY",BODY,{"disambiguationData":[OSD([sQuery(id+"F0.wireOp",EDGE,"E9.14.0.0")])]});
            var Q356;
            Q356=makeQuery(id+"F2.opExtrude","SWEPT_BODY",BODY,{"disambiguationData":[OSD([sQuery(id+"F0.wireOp",EDGE,"E9.14.0.1")])]});
            var Q357;
            Q357=makeQuery(id+"F2.opExtrude","SWEPT_BODY",BODY,{"disambiguationData":[OSD([sQuery(id+"F0.wireOp",EDGE,"E9.14.0.2")])]});
            var Q358;
            Q358=makeQuery(id+"F2.opExtrude","SWEPT_BODY",BODY,{"disambiguationData":[OSD([sQuery(id+"F0.wireOp",EDGE,"E9.14.0.3")])]});
            var Q359;
            Q359=makeQuery(id+"F2.opExtrude","SWEPT_BODY",BODY,{"disambiguationData":[OSD([sQuery(id+"F0.wireOp",EDGE,"E9.14.0.4")])]});
            var Q360;
            Q360=makeQuery(id+"F2.opExtrude","SWEPT_BODY",BODY,{"disambiguationData":[OSD([sQuery(id+"F0.wireOp",EDGE,"E9.14.0.5")])]});
            var Q361;
            Q361=makeQuery(id+"F2.opExtrude","SWEPT_BODY",BODY,{"disambiguationData":[OSD([sQuery(id+"F0.wireOp",EDGE,"E9.14.0.6")])]});
            var Q362;
            Q362=makeQuery(id+"F2.opExtrude","SWEPT_BODY",BODY,{"disambiguationData":[OSD([sQuery(id+"F0.wireOp",EDGE,"E9.14.0.7")])]});
            var Q363;
            Q363=makeQuery(id+"F2.opExtrude","SWEPT_BODY",BODY,{"disambiguationData":[OSD([sQuery(id+"F0.wireOp",EDGE,"E9.14.0.8")])]});
            var Q364;
            Q364=makeQuery(id+"F2.opExtrude","SWEPT_BODY",BODY,{"disambiguationData":[OSD([sQuery(id+"F0.wireOp",EDGE,"E9.14.0.9")])]});
            var Q365;
            Q365=makeQuery(id+"F2.opExtrude","SWEPT_BODY",BODY,{"disambiguationData":[OSD([sQuery(id+"F0.wireOp",EDGE,"E9.14.0.10")])]});
            var Q366;
            Q366=makeQuery(id+"F2.opExtrude","SWEPT_BODY",BODY,{"disambiguationData":[OSD([sQuery(id+"F0.wireOp",EDGE,"E9.14.0.11")])]});
            var Q367;
            Q367=makeQuery(id+"F2.opExtrude","SWEPT_BODY",BODY,{"disambiguationData":[OSD([sQuery(id+"F0.wireOp",EDGE,"E9.14.0.12")])]});
            var Q368;
            Q368=makeQuery(id+"F2.opExtrude","SWEPT_BODY",BODY,{"disambiguationData":[OSD([sQuery(id+"F0.wireOp",EDGE,"E9.14.0.13")])]});
            var Q369;
            Q369=makeQuery(id+"F2.opExtrude","SWEPT_BODY",BODY,{"disambiguationData":[OSD([sQuery(id+"F0.wireOp",EDGE,"E9.14.0.14")])]});
            var Q370;
            Q370=makeQuery(id+"F2.opExtrude","SWEPT_BODY",BODY,{"disambiguationData":[OSD([sQuery(id+"F0.wireOp",EDGE,"E9.14.0.15")])]});
            var Q371;
            Q371=makeQuery(id+"F2.opExtrude","SWEPT_BODY",BODY,{"disambiguationData":[OSD([sQuery(id+"F0.wireOp",EDGE,"E9.14.0.16")])]});
            var Q372;
            Q372=makeQuery(id+"F2.opExtrude","SWEPT_BODY",BODY,{"disambiguationData":[OSD([sQuery(id+"F0.wireOp",EDGE,"E9.14.0.17")])]});
            var Q373;
            Q373=makeQuery(id+"F2.opExtrude","SWEPT_BODY",BODY,{"disambiguationData":[OSD([sQuery(id+"F0.wireOp",EDGE,"E9.14.0.18")])]});
            var Q374;
            Q374=makeQuery(id+"F2.opExtrude","SWEPT_BODY",BODY,{"disambiguationData":[OSD([sQuery(id+"F0.wireOp",EDGE,"E9.14.0.19")])]});
            var Q375;
            Q375=makeQuery(id+"F2.opExtrude","SWEPT_BODY",BODY,{"disambiguationData":[OSD([sQuery(id+"F0.wireOp",EDGE,"E9.14.0.20")])]});
            var Q376;
            Q376=makeQuery(id+"F2.opExtrude","SWEPT_BODY",BODY,{"disambiguationData":[OSD([sQuery(id+"F0.wireOp",EDGE,"E9.14.0.21")])]});
            var Q377;
            Q377=makeQuery(id+"F2.opExtrude","SWEPT_BODY",BODY,{"disambiguationData":[OSD([sQuery(id+"F0.wireOp",EDGE,"E9.14.0.22")])]});
            var Q378;
            Q378=makeQuery(id+"F2.opExtrude","SWEPT_BODY",BODY,{"disambiguationData":[OSD([sQuery(id+"F0.wireOp",EDGE,"E9.14.0.23")])]});
            var Q379;
            Q379=makeQuery(id+"F4.opExtrude","SWEPT_BODY",BODY,{"disambiguationData":[OSD([sQuery(id+"F1.wireOp",EDGE,"E10.bottom"),sQuery(id+"F1.wireOp",EDGE,"E10.top"),sQuery(id+"F1.wireOp",EDGE,"E10.left"),sQuery(id+"F1.wireOp",EDGE,"E10.right")])]});
            booleanBodies(context, id + "F5", {"operationType" : BooleanOperationType.SUBTRACTION, "tools" : qUnion([Q0, Q1, Q2, Q3, Q4, Q5, Q6, Q7, Q8, Q9, Q10, Q11, Q12, Q13, Q14, Q15, Q16, Q17, Q18, Q19, Q20, Q21, Q22, Q23, Q24, Q25, Q26, Q27, Q28, Q29, Q30, Q31, Q32, Q33, Q34, Q35, Q36, Q37, Q38, Q39, Q40, Q41, Q42, Q43, Q44, Q45, Q46, Q47, Q48, Q49, Q50, Q51, Q52, Q53, Q54, Q55, Q56, Q57, Q58, Q59, Q60, Q61, Q62, Q63, Q64, Q65, Q66, Q67, Q68, Q69, Q70, Q71, Q72, Q73, Q74, Q75, Q76, Q77, Q78, Q79, Q80, Q81, Q82, Q83, Q84, Q85, Q86, Q87, Q88, Q89, Q90, Q91, Q92, Q93, Q94, Q95, Q96, Q97, Q98, Q99, Q100, Q101, Q102, Q103, Q104, Q105, Q106, Q107, Q108, Q109, Q110, Q111, Q112, Q113, Q114, Q115, Q116, Q117, Q118, Q119, Q120, Q121, Q122, Q123, Q124, Q125, Q126, Q127, Q128, Q129, Q130, Q131, Q132, Q133, Q134, Q135, Q136, Q137, Q138, Q139, Q140, Q141, Q142, Q143, Q144, Q145, Q146, Q147, Q148, Q149, Q150, Q151, Q152, Q153, Q154, Q155, Q156, Q157, Q158, Q159, Q160, Q161, Q162, Q163, Q164, Q165, Q166, Q167, Q168, Q169, Q170, Q171, Q172, Q173, Q174, Q175, Q176, Q177, Q178, Q179, Q180, Q181, Q182, Q183, Q184, Q185, Q186, Q187, Q188, Q189, Q190, Q191, Q192, Q193, Q194, Q195, Q196, Q197, Q198, Q199, Q200, Q201, Q202, Q203, Q204, Q205, Q206, Q207, Q208, Q209, Q210, Q211, Q212, Q213, Q214, Q215, Q216, Q217, Q218, Q219, Q220, Q221, Q222, Q223, Q224, Q225, Q226, Q227, Q228, Q229, Q230, Q231, Q232, Q233, Q234, Q235, Q236, Q237, Q238, Q239, Q240, Q241, Q242, Q243, Q244, Q245, Q246, Q247, Q248, Q249, Q250, Q251, Q252, Q253, Q254, Q255, Q256, Q257, Q258, Q259, Q260, Q261, Q262, Q263, Q264, Q265, Q266, Q267, Q268, Q269, Q270, Q271, Q272, Q273, Q274, Q275, Q276, Q277, Q278, Q279, Q280, Q281, Q282, Q283, Q284, Q285, Q286, Q287, Q288, Q289, Q290, Q291, Q292, Q293, Q294, Q295, Q296, Q297, Q298, Q299, Q300, Q301, Q302, Q303, Q304, Q305, Q306, Q307, Q308, Q309, Q310, Q311, Q312, Q313, Q314, Q315, Q316, Q317, Q318, Q319, Q320, Q321, Q322, Q323, Q324, Q325, Q326, Q327, Q328, Q329, Q330, Q331, Q332, Q333, Q334, Q335, Q336, Q337, Q338, Q339, Q340, Q341, Q342, Q343, Q344, Q345, Q346, Q347, Q348, Q349, Q350, Q351, Q352, Q353, Q354, Q355, Q356, Q357, Q358, Q359, Q360, Q361, Q362, Q363, Q364, Q365, Q366, Q367, Q368, Q369, Q370, Q371, Q372, Q373, Q374, Q375, Q376, Q377, Q378]), "targets" : qUnion([Q379])});
        }
    });
